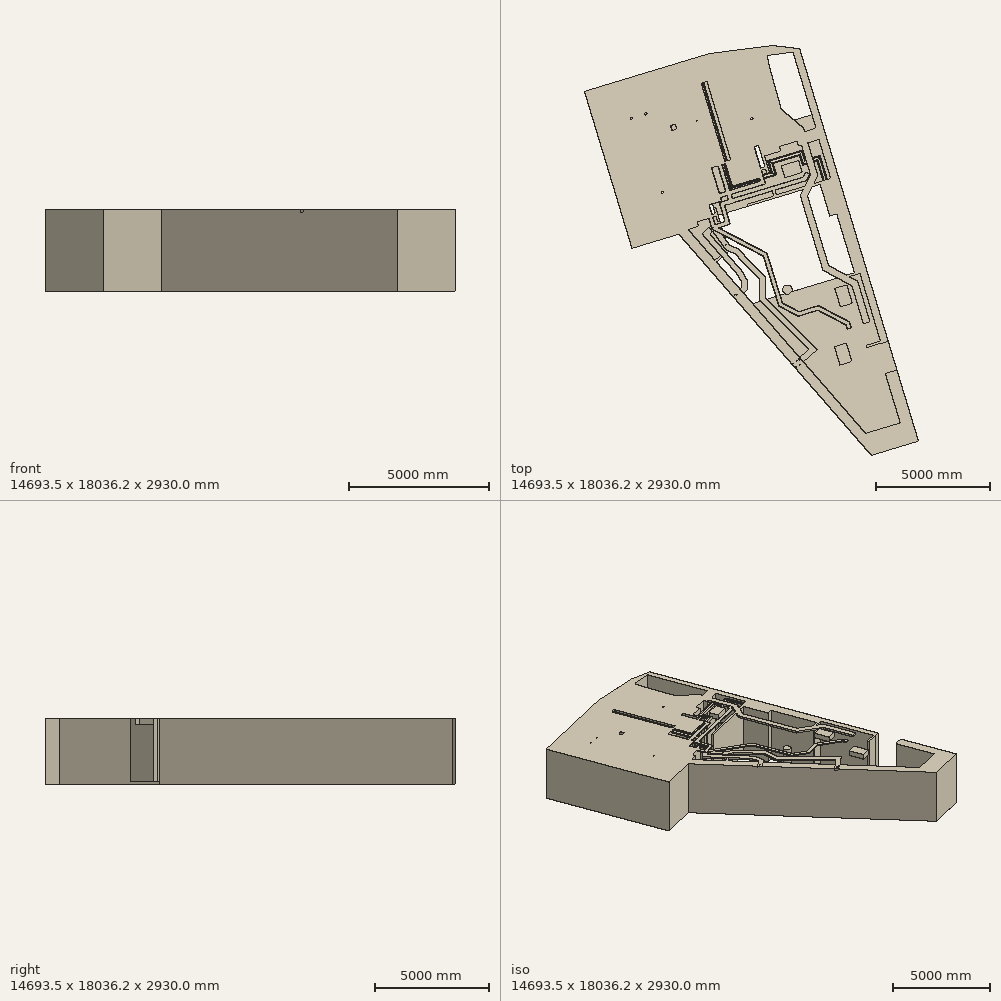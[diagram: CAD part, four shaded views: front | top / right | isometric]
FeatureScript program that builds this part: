
annotation { "Feature Type Name" : "Feature", "Feature Type Description" : "" }
export const myFeature = defineFeature(function(context is Context, id is Id, definition is map)
    precondition{}
    {
        {
            var Q0;
            Q0=qCreatedBy(makeId("Top.planeOp"),FACE);
            var sketch = newSketch(context, id + "F0", { "sketchPlane" : qUnion([Q0])});
            skLineSegment(sketch, "E0", {"start": v(688.47, 32038.93) * mm, "end": v(503.96, 32648.57) * mm});
            skLineSegment(sketch, "E1", {"start": v(503.96, 32648.57) * mm, "end": v(1685.98, 33006.34) * mm});
            skLineSegment(sketch, "E2", {"start": v(1685.98, 33006.34) * mm, "end": v(1870.5, 32396.71) * mm});
            skLineSegment(sketch, "E3", {"start": v(1870.5, 32396.71) * mm, "end": v(688.47, 32038.93) * mm});
            skLineSegment(sketch, "E4", {"start": v(975.28, 28670.43) * mm, "end": v(-209.3, 30031.2) * mm});
            skLineSegment(sketch, "E5", {"start": v(-209.3, 30031.2) * mm, "end": v(247, 30169.35) * mm});
            skLineSegment(sketch, "E6", {"start": v(247, 30169.35) * mm, "end": v(187.3, 30366.58) * mm});
            skLineSegment(sketch, "E7", {"start": v(187.3, 30366.58) * mm, "end": v(1017.23, 30617.78) * mm});
            skLineSegment(sketch, "E8", {"start": v(1017.23, 30617.78) * mm, "end": v(1474.96, 29105.4) * mm});
            skLineSegment(sketch, "E9", {"start": v(1474.96, 29105.4) * mm, "end": v(975.28, 28670.43) * mm});
            skLineSegment(sketch, "E10", {"start": v(2976.11, 33751) * mm, "end": v(2796.5, 34344.43) * mm});
            skLineSegment(sketch, "E11", {"start": v(2796.5, 34344.43) * mm, "end": v(5232.35, 35081.71) * mm});
            skLineSegment(sketch, "E12", {"start": v(5232.35, 35081.71) * mm, "end": v(5411.97, 34488.28) * mm});
            skLineSegment(sketch, "E13", {"start": v(5411.97, 34488.28) * mm, "end": v(2976.11, 33751) * mm});
            skLineSegment(sketch, "E14", {"start": v(1038.97, 28597.26) * mm, "end": v(1585.97, 29073.44) * mm});
            skLineSegment(sketch, "E15", {"start": v(1585.97, 29073.44) * mm, "end": v(1107.2, 30655.36) * mm});
            skLineSegment(sketch, "E16", {"start": v(1107.2, 30655.36) * mm, "end": v(5663.61, 32034.54) * mm});
            skLineSegment(sketch, "E17", {"start": v(5663.61, 32034.54) * mm, "end": v(6064.95, 30708.6) * mm});
            skLineSegment(sketch, "E18", {"start": v(6064.95, 30708.6) * mm, "end": v(6370.27, 30801.02) * mm});
            skLineSegment(sketch, "E19", {"start": v(6370.27, 30801.02) * mm, "end": v(7173.28, 28148.02) * mm});
            skLineSegment(sketch, "E20", {"start": v(7173.28, 28148.02) * mm, "end": v(2627.74, 26772.17) * mm});
            skLineSegment(sketch, "E21", {"start": v(2627.74, 26772.17) * mm, "end": v(1038.97, 28597.26) * mm});
            skLineSegment(sketch, "E22", {"start": v(7648.03, 21005.12) * mm, "end": v(9204.22, 21476.13) * mm});
            skLineSegment(sketch, "E23", {"start": v(9204.22, 21476.13) * mm, "end": v(8546.54, 23648.8) * mm});
            skLineSegment(sketch, "E24", {"start": v(8546.54, 23648.8) * mm, "end": v(8680.59, 23689.38) * mm});
            skLineSegment(sketch, "E25", {"start": v(8680.59, 23689.38) * mm, "end": v(8275.24, 25028.58) * mm});
            skLineSegment(sketch, "E26", {"start": v(8275.24, 25028.58) * mm, "end": v(7643.52, 24837.37) * mm});
            skLineSegment(sketch, "E27", {"start": v(7643.52, 24837.37) * mm, "end": v(7615.16, 24931.08) * mm});
            skLineSegment(sketch, "E28", {"start": v(7615.16, 24931.08) * mm, "end": v(8246.85, 25122.28) * mm});
            skLineSegment(sketch, "E29", {"start": v(8246.85, 25122.28) * mm, "end": v(7345.9, 28098.92) * mm});
            skLineSegment(sketch, "E30", {"start": v(7345.9, 28098.92) * mm, "end": v(6714.19, 27907.71) * mm});
            skLineSegment(sketch, "E31", {"start": v(6714.19, 27907.71) * mm, "end": v(6686.09, 28000.55) * mm});
            skLineSegment(sketch, "E32", {"start": v(6686.09, 28000.55) * mm, "end": v(2627.74, 26772.17) * mm});
            skLineSegment(sketch, "E33", {"start": v(2627.74, 26772.17) * mm, "end": v(7648.03, 21005.12) * mm});
            skLineSegment(sketch, "E34", {"start": v(1953.77, 32421.91) * mm, "end": v(484.9, 37274.77) * mm});
            skLineSegment(sketch, "E35", {"start": v(484.9, 37274.77) * mm, "end": v(817.35, 37375.45) * mm});
            skLineSegment(sketch, "E36", {"start": v(817.35, 37375.45) * mm, "end": v(4399.01, 37834.91) * mm});
            skLineSegment(sketch, "E37", {"start": v(4399.01, 37834.91) * mm, "end": v(5232.35, 35081.71) * mm});
            skLineSegment(sketch, "E38", {"start": v(5232.35, 35081.71) * mm, "end": v(2703.65, 34316.33) * mm});
            skLineSegment(sketch, "E39", {"start": v(2703.65, 34316.33) * mm, "end": v(3166, 32788.83) * mm});
            skLineSegment(sketch, "E40", {"start": v(3166, 32788.83) * mm, "end": v(1953.77, 32421.91) * mm});
            skLineSegment(sketch, "E41", {"start": v(-3492.5, 33275.5) * mm, "end": v(592.96, 34511.99) * mm});
            skLineSegment(sketch, "E42", {"start": v(592.96, 34511.99) * mm, "end": v(1074.07, 32922.48) * mm});
            skLineSegment(sketch, "E43", {"start": v(1074.07, 32922.48) * mm, "end": v(383.02, 32713.3) * mm});
            skLineSegment(sketch, "E44", {"start": v(383.02, 32713.3) * mm, "end": v(981.9, 30734.55) * mm});
            skLineSegment(sketch, "E45", {"start": v(981.9, 30734.55) * mm, "end": v(-2157.46, 29784.33) * mm});
            skLineSegment(sketch, "E46", {"start": v(-2157.46, 29784.33) * mm, "end": v(-2347.02, 30410.5) * mm});
            skLineSegment(sketch, "E47", {"start": v(-2347.02, 30410.5) * mm, "end": v(-2601.66, 30332.35) * mm});
            skLineSegment(sketch, "E48", {"start": v(-2601.66, 30332.35) * mm, "end": v(-3492.5, 33275.5) * mm});
            skLineSegment(sketch, "E49", {"start": v(-710, 34438.17) * mm, "end": v(-3559.9, 33575.84) * mm});
            skLineSegment(sketch, "E50", {"start": v(-3559.9, 33575.84) * mm, "end": v(-3973.74, 34943.1) * mm});
            skLineSegment(sketch, "E51", {"start": v(-3973.74, 34943.1) * mm, "end": v(-3685.65, 35030.3) * mm});
            skLineSegment(sketch, "E52", {"start": v(-3685.65, 35030.3) * mm, "end": v(-3957.95, 35930) * mm});
            skLineSegment(sketch, "E53", {"start": v(-3957.95, 35930) * mm, "end": v(-1009.44, 36822.46) * mm});
            skLineSegment(sketch, "E54", {"start": v(-1009.44, 36822.46) * mm, "end": v(-831.43, 36230.92) * mm});
            skLineSegment(sketch, "E55", {"start": v(-831.43, 36230.92) * mm, "end": v(-977.95, 36186.57) * mm});
            skLineSegment(sketch, "E56", {"start": v(-977.95, 36186.57) * mm, "end": v(-622.8, 35013.09) * mm});
            skLineSegment(sketch, "E57", {"start": v(-622.8, 35013.09) * mm, "end": v(-861.8, 34940.5) * mm});
            skLineSegment(sketch, "E58", {"start": v(-861.8, 34940.5) * mm, "end": v(-710, 34438.17) * mm});
            skLineSegment(sketch, "E59", {"start": v(1107.2, 30655.36) * mm, "end": v(2396.47, 31045.6) * mm});
            skLineSegment(sketch, "E60", {"start": v(2396.47, 31045.6) * mm, "end": v(2368.65, 31137.53) * mm});
            skLineSegment(sketch, "E61", {"start": v(2368.65, 31137.53) * mm, "end": v(3556.94, 31497.2) * mm});
            skLineSegment(sketch, "E62", {"start": v(3556.94, 31497.2) * mm, "end": v(3194.1, 32695.99) * mm});
            skLineSegment(sketch, "E63", {"start": v(3194.1, 32695.99) * mm, "end": v(716.57, 31946.1) * mm});
            skLineSegment(sketch, "E64", {"start": v(716.57, 31946.1) * mm, "end": v(1107.2, 30655.36) * mm});
            skLineSegment(sketch, "E65", {"start": v(-828.96, 36106.8) * mm, "end": v(-267.45, 34251.56) * mm});
            skLineSegment(sketch, "E66", {"start": v(-267.45, 34251.56) * mm, "end": v(583.39, 34509.09) * mm});
            skLineSegment(sketch, "E67", {"start": v(583.39, 34509.09) * mm, "end": v(1064.5, 32919.58) * mm});
            skLineSegment(sketch, "E68", {"start": v(1064.5, 32919.58) * mm, "end": v(1657.88, 33099.18) * mm});
            skLineSegment(sketch, "E69", {"start": v(1657.88, 33099.18) * mm, "end": v(615.22, 36543.93) * mm});
            skLineSegment(sketch, "E70", {"start": v(615.22, 36543.93) * mm, "end": v(-828.96, 36106.8) * mm});
            skLineSegment(sketch, "E71", {"start": v(2521, 36867.94) * mm, "end": v(2477.55, 37011.51) * mm});
            skLineSegment(sketch, "E72", {"start": v(2477.55, 37011.51) * mm, "end": v(2621.12, 37054.97) * mm});
            skLineSegment(sketch, "E73", {"start": v(2621.12, 37054.97) * mm, "end": v(2664.57, 36911.4) * mm});
            skLineSegment(sketch, "E74", {"start": v(2664.57, 36911.4) * mm, "end": v(2521, 36867.94) * mm});
            skCircle(sketch, "E75", {"center": v(2571.06, 36961.45) * mm, "radius": 75 * mm});
            skLineSegment(sketch, "E76", {"start": v(6682.01, 27897.97) * mm, "end": v(2720.36, 26698.86) * mm});
            skLineSegment(sketch, "E77", {"start": v(2845.75, 34181.7) * mm, "end": v(5281.61, 34918.98) * mm});
            skLineSegment(sketch, "E78", {"start": v(6128.04, 25871.52) * mm, "end": v(6340.42, 26268.26) * mm});
            skCircle(sketch, "E79", {"center": v(6234.23, 26069.9) * mm, "radius": 225 * mm});
            skCircle(sketch, "E80", {"center": v(-1847.03, 34397.83) * mm, "radius": 70 * mm});
            skCircle(sketch, "E81", {"center": v(-1031.48, 34644.68) * mm, "radius": 70 * mm});
            skCircle(sketch, "E82", {"center": v(-2662.4, 34151.03) * mm, "radius": 70 * mm});
            skCircle(sketch, "E83", {"center": v(-3282.71, 33963.28) * mm, "radius": 70 * mm});
            skCircle(sketch, "E84", {"center": v(1346.97, 36590.95) * mm, "radius": 70 * mm});
            skCircle(sketch, "E85", {"center": v(1919, 34705.78) * mm, "radius": 70 * mm});
            skCircle(sketch, "E86", {"center": v(4106.18, 35367.8) * mm, "radius": 70 * mm});
            skCircle(sketch, "E87", {"center": v(4291.3, 37482.1) * mm, "radius": 24.96 * mm});
            skCircle(sketch, "E88", {"center": v(4291.3, 37482.1) * mm, "radius": 89.6 * mm});
            skCircle(sketch, "E89", {"center": v(3702.85, 29215.68) * mm, "radius": 50 * mm});
            skLineSegment(sketch, "E90", {"start": v(3774.64, 29237.4) * mm, "end": v(3631.07, 29193.95) * mm});
            skLineSegment(sketch, "E91", {"start": v(3681.12, 29287.46) * mm, "end": v(3724.58, 29143.9) * mm});
            skLineSegment(sketch, "E92", {"start": v(4947.02, 28251.96) * mm, "end": v(4903.56, 28395.53) * mm});
            skLineSegment(sketch, "E93", {"start": v(4903.56, 28395.53) * mm, "end": v(5047.13, 28438.98) * mm});
            skLineSegment(sketch, "E94", {"start": v(5047.13, 28438.98) * mm, "end": v(5090.59, 28295.41) * mm});
            skLineSegment(sketch, "E95", {"start": v(5090.59, 28295.41) * mm, "end": v(4947.02, 28251.96) * mm});
            skCircle(sketch, "E96", {"center": v(4997.08, 28345.47) * mm, "radius": 75 * mm});
            skCircle(sketch, "E97", {"center": v(4647.16, 29501.5) * mm, "radius": 50 * mm});
            skCircle(sketch, "E98", {"center": v(4647.16, 29501.5) * mm, "radius": 185.02 * mm});
            skCircle(sketch, "E99", {"center": v(5731.95, 25917.86) * mm, "radius": 50 * mm});
            skCircle(sketch, "E100", {"center": v(5731.95, 25917.86) * mm, "radius": 185.02 * mm});
            skCircle(sketch, "E101", {"center": v(-1220.67, 35372.03) * mm, "radius": 23.22 * mm});
            skCircle(sketch, "E102", {"center": v(-3689, 35802.45) * mm, "radius": 52 * mm});
            skCircle(sketch, "E103", {"center": v(2856.43, 36018.65) * mm, "radius": 50 * mm});
            skLineSegment(sketch, "E104", {"start": v(2928.21, 36040.38) * mm, "end": v(2784.64, 35996.93) * mm});
            skLineSegment(sketch, "E105", {"start": v(2834.7, 36090.44) * mm, "end": v(2878.16, 35946.87) * mm});
            skCircle(sketch, "E106", {"center": v(2789.14, 31831.37) * mm, "radius": 70 * mm});
            skCircle(sketch, "E107", {"center": v(2325.79, 33360.78) * mm, "radius": 70 * mm});
            skCircle(sketch, "E108", {"center": v(-3089.6, 33189.85) * mm, "radius": 24.96 * mm});
            skCircle(sketch, "E109", {"center": v(-3089.61, 33189.85) * mm, "radius": 89.6 * mm});
            skCircle(sketch, "E110", {"center": v(-694.3, 33908.01) * mm, "radius": 24.96 * mm});
            skCircle(sketch, "E111", {"center": v(-694.3, 33908.01) * mm, "radius": 89.6 * mm});
            skCircle(sketch, "E112", {"center": v(5238.28, 31100.14) * mm, "radius": 70 * mm});
            skCircle(sketch, "E113", {"center": v(-2823.66, 32311.65) * mm, "radius": 70 * mm});
            skLineSegment(sketch, "E114", {"start": v(-1847.07, 31588.32) * mm, "end": v(-1803.62, 31444.75) * mm});
            skLineSegment(sketch, "E115", {"start": v(-1803.62, 31444.75) * mm, "end": v(-1947.18, 31401.3) * mm});
            skLineSegment(sketch, "E116", {"start": v(-1947.18, 31401.3) * mm, "end": v(-1990.64, 31544.87) * mm});
            skLineSegment(sketch, "E117", {"start": v(-1990.64, 31544.87) * mm, "end": v(-1847.07, 31588.32) * mm});
            skCircle(sketch, "E118", {"center": v(-1897.13, 31494.81) * mm, "radius": 75 * mm});
            skLineSegment(sketch, "E119", {"start": v(-798.77, 31748.9) * mm, "end": v(-842.22, 31892.47) * mm});
            skLineSegment(sketch, "E120", {"start": v(-842.22, 31892.47) * mm, "end": v(-698.66, 31935.92) * mm});
            skLineSegment(sketch, "E121", {"start": v(-698.66, 31935.92) * mm, "end": v(-655.2, 31792.36) * mm});
            skLineSegment(sketch, "E122", {"start": v(-655.2, 31792.36) * mm, "end": v(-798.77, 31748.9) * mm});
            skCircle(sketch, "E123", {"center": v(-748.71, 31842.41) * mm, "radius": 75 * mm});
            skCircle(sketch, "E124", {"center": v(-1322.96, 31668.6) * mm, "radius": 50 * mm});
            skLineSegment(sketch, "E125", {"start": v(-1251.18, 31690.33) * mm, "end": v(-1394.75, 31646.87) * mm});
            skLineSegment(sketch, "E126", {"start": v(-1344.7, 31740.38) * mm, "end": v(-1301.24, 31596.82) * mm});
            skCircle(sketch, "E127", {"center": v(1916.85, 30094.8) * mm, "radius": 70 * mm});
            skLineSegment(sketch, "E128", {"start": v(5408.3, 27246.02) * mm, "end": v(5451.75, 27102.45) * mm});
            skLineSegment(sketch, "E129", {"start": v(5451.75, 27102.45) * mm, "end": v(5308.19, 27059) * mm});
            skLineSegment(sketch, "E130", {"start": v(5308.19, 27059) * mm, "end": v(5264.73, 27202.57) * mm});
            skLineSegment(sketch, "E131", {"start": v(5264.73, 27202.57) * mm, "end": v(5408.3, 27246.02) * mm});
            skCircle(sketch, "E132", {"center": v(5358.24, 27152.51) * mm, "radius": 75 * mm});
            skCircle(sketch, "E133", {"center": v(7896.13, 22311.4) * mm, "radius": 50 * mm});
            skLineSegment(sketch, "E134", {"start": v(7967.91, 22333.12) * mm, "end": v(7824.34, 22289.67) * mm});
            skLineSegment(sketch, "E135", {"start": v(7874.4, 22383.18) * mm, "end": v(7917.86, 22239.6) * mm});
            skLineSegment(sketch, "E136", {"start": v(7346.13, 23869.61) * mm, "end": v(7302.67, 24013.18) * mm});
            skLineSegment(sketch, "E137", {"start": v(7302.67, 24013.18) * mm, "end": v(7446.24, 24056.63) * mm});
            skLineSegment(sketch, "E138", {"start": v(7446.24, 24056.63) * mm, "end": v(7489.7, 23913.07) * mm});
            skLineSegment(sketch, "E139", {"start": v(7489.7, 23913.07) * mm, "end": v(7346.13, 23869.61) * mm});
            skCircle(sketch, "E140", {"center": v(7396.18, 23963.12) * mm, "radius": 75 * mm});
            skCircle(sketch, "E141", {"center": v(7193.06, 26360.11) * mm, "radius": 50 * mm});
            skLineSegment(sketch, "E142", {"start": v(7240.92, 26374.6) * mm, "end": v(7514.25, 26457.33) * mm});
            skLineSegment(sketch, "E143", {"start": v(7365.6, 26307.86) * mm, "end": v(7240.92, 26374.6) * mm});
            skLineSegment(sketch, "E144", {"start": v(7240.92, 26374.6) * mm, "end": v(7307.66, 26499.27) * mm});
            skLineSegment(sketch, "E145", {"start": v(7307.66, 26499.27) * mm, "end": v(7365.6, 26307.86) * mm});
            skLineSegment(sketch, "E146", {"start": v(575.66, 33236.57) * mm, "end": v(546.8, 33331.8) * mm});
            skLineSegment(sketch, "E147", {"start": v(546.8, 33331.8) * mm, "end": v(655.88, 33364.87) * mm});
            skLineSegment(sketch, "E148", {"start": v(655.88, 33364.87) * mm, "end": v(684.75, 33269.65) * mm});
            skLineSegment(sketch, "E149", {"start": v(684.75, 33269.65) * mm, "end": v(575.66, 33236.57) * mm});
            skLineSegment(sketch, "E150", {"start": v(546.79, 33331.8) * mm, "end": v(517.92, 33427.01) * mm});
            skLineSegment(sketch, "E151", {"start": v(517.92, 33427.01) * mm, "end": v(627.01, 33460.09) * mm});
            skLineSegment(sketch, "E152", {"start": v(627.01, 33460.09) * mm, "end": v(655.88, 33364.87) * mm});
            skLineSegment(sketch, "E153", {"start": v(655.88, 33364.87) * mm, "end": v(546.79, 33331.8) * mm});
            skLineSegment(sketch, "E154", {"start": v(3585.52, 37346.87) * mm, "end": v(3628.97, 37203.3) * mm});
            skLineSegment(sketch, "E155", {"start": v(3628.97, 37203.3) * mm, "end": v(3485.4, 37159.85) * mm});
            skLineSegment(sketch, "E156", {"start": v(3485.4, 37159.85) * mm, "end": v(3441.95, 37303.42) * mm});
            skLineSegment(sketch, "E157", {"start": v(3441.95, 37303.42) * mm, "end": v(3585.52, 37346.87) * mm});
            skCircle(sketch, "E158", {"center": v(3535.46, 37253.36) * mm, "radius": 75 * mm});
            skLineSegment(sketch, "E159", {"start": v(-4301.45, 33405.9) * mm, "end": v(-4393.43, 33709.79) * mm});
            skEllipse(sketch, "E160", {"center": v(-4253.27, 33246.73) * mm, "majorRadius": 182.04 * mm, "minorRadius": 182.04 * mm, "majorAxis": v(0.7, 0.7)});
            skLineSegment(sketch, "E161", {"start": v(-4393.43, 33709.79) * mm, "end": v(-3952.33, 34533.82) * mm});
            skLineSegment(sketch, "E162", {"start": v(-4064.75, 34413.93) * mm, "end": v(-3952.33, 34533.82) * mm});
            skLineSegment(sketch, "E163", {"start": v(-3952.33, 34533.82) * mm, "end": v(-3989.74, 34373.78) * mm});
            skLineSegment(sketch, "E164", {"start": v(-3989.74, 34373.78) * mm, "end": v(-4064.75, 34413.93) * mm});
            skLineSegment(sketch, "E165", {"start": v(-3654.18, 34799.3) * mm, "end": v(-3257.44, 34586.93) * mm});
            skCircle(sketch, "E166", {"center": v(-3455.8, 34693.11) * mm, "radius": 225 * mm});
            skLineSegment(sketch, "E167", {"start": v(-2284.17, 37866.22) * mm, "end": v(-2192.19, 37562.34) * mm});
            skEllipse(sketch, "E168", {"center": v(-2332.35, 38025.4) * mm, "majorRadius": 182.04 * mm, "minorRadius": 182.04 * mm, "majorAxis": v(1, 0)});
            skLineSegment(sketch, "E169", {"start": v(-2192.19, 37562.34) * mm, "end": v(-2055.36, 37110.28) * mm});
            skLineSegment(sketch, "E170", {"start": v(-2060.64, 37274.55) * mm, "end": v(-2055.36, 37110.28) * mm});
            skLineSegment(sketch, "E171", {"start": v(-2055.36, 37110.28) * mm, "end": v(-2142.06, 37249.9) * mm});
            skLineSegment(sketch, "E172", {"start": v(-2142.06, 37249.9) * mm, "end": v(-2060.64, 37274.55) * mm});
            skLineSegment(sketch, "E173", {"start": v(6324.7, 31290.66) * mm, "end": v(6411.61, 31003.53) * mm});
            skLineSegment(sketch, "E174", {"start": v(6411.61, 31003.53) * mm, "end": v(6124.47, 30916.62) * mm});
            skLineSegment(sketch, "E175", {"start": v(6124.47, 30916.62) * mm, "end": v(6037.56, 31203.75) * mm});
            skLineSegment(sketch, "E176", {"start": v(6037.56, 31203.75) * mm, "end": v(6324.7, 31290.66) * mm});
            skLineSegment(sketch, "E177", {"start": v(6324.7, 31290.66) * mm, "end": v(6124.47, 30916.62) * mm});
            skCircle(sketch, "E178", {"center": v(-3095.59, 35982.06) * mm, "radius": 52 * mm});
            skCircle(sketch, "E179", {"center": v(-2502.17, 36161.68) * mm, "radius": 52 * mm});
            skCircle(sketch, "E180", {"center": v(-1908.76, 36341.3) * mm, "radius": 52 * mm});
            skCircle(sketch, "E181", {"center": v(-1315.35, 36520.9) * mm, "radius": 52 * mm});
            skCircle(sketch, "E182", {"center": v(2532.3, 27643.33) * mm, "radius": 70 * mm});
            skCircle(sketch, "E183", {"center": v(1875.7, 28397.58) * mm, "radius": 70 * mm});
            skLineSegment(sketch, "E184", {"start": v(1609.88, 32773.32) * mm, "end": v(1696.79, 32486.2) * mm});
            skLineSegment(sketch, "E185", {"start": v(1696.79, 32486.2) * mm, "end": v(1409.64, 32399.28) * mm});
            skLineSegment(sketch, "E186", {"start": v(1409.64, 32399.28) * mm, "end": v(1322.74, 32686.4) * mm});
            skLineSegment(sketch, "E187", {"start": v(1322.74, 32686.4) * mm, "end": v(1609.88, 32773.32) * mm});
            skLineSegment(sketch, "E188", {"start": v(1609.88, 32773.32) * mm, "end": v(1409.64, 32399.28) * mm});
            skCircle(sketch, "E189", {"center": v(6011.32, 23646.8) * mm, "radius": 70 * mm});
            skCircle(sketch, "E190", {"center": v(3459.78, 26577.88) * mm, "radius": 70 * mm});
            skCircle(sketch, "E191", {"center": v(8590.03, 22521.42) * mm, "radius": 70 * mm});
            skCircle(sketch, "E192", {"center": v(6714.5, 26215.26) * mm, "radius": 70 * mm});
            skCircle(sketch, "E193", {"center": v(7043.04, 25129.83) * mm, "radius": 70 * mm});
            skCircle(sketch, "E194", {"center": v(4413.86, 26866.66) * mm, "radius": 50 * mm});
            skLineSegment(sketch, "E195", {"start": v(4485.64, 26888.4) * mm, "end": v(4342.07, 26844.94) * mm});
            skLineSegment(sketch, "E196", {"start": v(4392.13, 26938.45) * mm, "end": v(4435.58, 26794.88) * mm});
            skCircle(sketch, "E197", {"center": v(5979.71, 28642.9) * mm, "radius": 70 * mm});
            skLineSegment(sketch, "E198", {"start": v(1029.24, 34682.5) * mm, "end": v(1116.14, 34395.38) * mm});
            skLineSegment(sketch, "E199", {"start": v(1116.14, 34395.38) * mm, "end": v(829, 34308.46) * mm});
            skLineSegment(sketch, "E200", {"start": v(829, 34308.46) * mm, "end": v(742.1, 34595.59) * mm});
            skLineSegment(sketch, "E201", {"start": v(742.1, 34595.59) * mm, "end": v(1029.24, 34682.5) * mm});
            skLineSegment(sketch, "E202", {"start": v(1029.24, 34682.5) * mm, "end": v(829, 34308.46) * mm});
            skLineSegment(sketch, "E203", {"start": v(3855.94, 24986.4) * mm, "end": v(3968.37, 25106.3) * mm});
            skLineSegment(sketch, "E204", {"start": v(3968.37, 25106.3) * mm, "end": v(3930.95, 24946.26) * mm});
            skLineSegment(sketch, "E205", {"start": v(3930.95, 24946.26) * mm, "end": v(3855.94, 24986.4) * mm});
            skLineSegment(sketch, "E206", {"start": v(6167.02, 21051.64) * mm, "end": v(6075.04, 21355.52) * mm});
            skEllipse(sketch, "E207", {"center": v(6215.2, 20892.46) * mm, "majorRadius": 182.04 * mm, "minorRadius": 182.04 * mm, "majorAxis": v(0.7, 0.7)});
            skLineSegment(sketch, "E208", {"start": v(6075.04, 21355.52) * mm, "end": v(6516.14, 22179.55) * mm});
            skLineSegment(sketch, "E209", {"start": v(6403.72, 22059.66) * mm, "end": v(6516.14, 22179.55) * mm});
            skLineSegment(sketch, "E210", {"start": v(6516.14, 22179.55) * mm, "end": v(6478.72, 22019.51) * mm});
            skLineSegment(sketch, "E211", {"start": v(6478.72, 22019.51) * mm, "end": v(6403.72, 22059.66) * mm});
            skLineSegment(sketch, "E212", {"start": v(-3715.4, 37697.94) * mm, "end": v(-2680.13, 36361.95) * mm});
            skLineSegment(sketch, "E213", {"start": v(-2743.75, 36513.49) * mm, "end": v(-2680.13, 36361.95) * mm});
            skLineSegment(sketch, "E214", {"start": v(-2680.13, 36361.95) * mm, "end": v(-2811, 36461.38) * mm});
            skLineSegment(sketch, "E215", {"start": v(-2811, 36461.38) * mm, "end": v(-2743.75, 36513.49) * mm});
            skLineSegment(sketch, "E216", {"start": v(6668.7, 25183.66) * mm, "end": v(6456.33, 24786.93) * mm});
            skCircle(sketch, "E217", {"center": v(6562.52, 24985.3) * mm, "radius": 225 * mm});
            skCircle(sketch, "E218", {"center": v(860.2, 30103.67) * mm, "radius": 50 * mm});
            skLineSegment(sketch, "E219", {"start": v(908.05, 30118.16) * mm, "end": v(1181.38, 30200.89) * mm});
            skLineSegment(sketch, "E220", {"start": v(1032.72, 30051.42) * mm, "end": v(908.05, 30118.16) * mm});
            skLineSegment(sketch, "E221", {"start": v(908.05, 30118.16) * mm, "end": v(974.79, 30242.83) * mm});
            skLineSegment(sketch, "E222", {"start": v(974.79, 30242.83) * mm, "end": v(1032.72, 30051.42) * mm});
            skLineSegment(sketch, "E223", {"start": v(3665, 31553.41) * mm, "end": v(3146.69, 33265.8) * mm});
            skLineSegment(sketch, "E224", {"start": v(3146.69, 33265.8) * mm, "end": v(3864.66, 33483.1) * mm});
            skLineSegment(sketch, "E225", {"start": v(3864.66, 33483.1) * mm, "end": v(3803.84, 33684.03) * mm});
            skLineSegment(sketch, "E226", {"start": v(3803.84, 33684.03) * mm, "end": v(4569.53, 33915.8) * mm});
            skLineSegment(sketch, "E227", {"start": v(4569.53, 33915.8) * mm, "end": v(4630.34, 33714.9) * mm});
            skLineSegment(sketch, "E228", {"start": v(4630.34, 33714.9) * mm, "end": v(5539.28, 33990.02) * mm});
            skLineSegment(sketch, "E229", {"start": v(5539.28, 33990.02) * mm, "end": v(6057.79, 32277.66) * mm});
            skLineSegment(sketch, "E230", {"start": v(6057.79, 32277.66) * mm, "end": v(3665, 31553.41) * mm});
            skCircle(sketch, "E231", {"center": v(3988.93, 33314.17) * mm, "radius": 70 * mm});
            skCircle(sketch, "E232", {"center": v(5732.52, 32722.3) * mm, "radius": 52 * mm});
            skCircle(sketch, "E233", {"center": v(5479.1, 33559.56) * mm, "radius": 52 * mm});
            skCircle(sketch, "E234", {"center": v(3586.94, 33192.5) * mm, "radius": 70 * mm});
            skCircle(sketch, "E235", {"center": v(5058.95, 32518.43) * mm, "radius": 50 * mm});
            skLineSegment(sketch, "E236", {"start": v(5035.58, 32474.22) * mm, "end": v(4902.1, 32221.76) * mm});
            skLineSegment(sketch, "E237", {"start": v(4900.44, 32432.56) * mm, "end": v(5035.58, 32474.22) * mm});
            skLineSegment(sketch, "E238", {"start": v(5035.58, 32474.22) * mm, "end": v(5077.24, 32339.09) * mm});
            skLineSegment(sketch, "E239", {"start": v(5077.24, 32339.09) * mm, "end": v(4900.44, 32432.56) * mm});
            skCircle(sketch, "E240", {"center": v(3482.78, 32663.76) * mm, "radius": 23.22 * mm});
            skLineSegment(sketch, "E241", {"start": v(1963.34, 32424.81) * mm, "end": v(494.48, 37277.66) * mm});
            skLineSegment(sketch, "E242", {"start": v(494.48, 37277.66) * mm, "end": v(561.48, 37297.94) * mm});
            skLineSegment(sketch, "E243", {"start": v(561.48, 37297.94) * mm, "end": v(2030.34, 32445.09) * mm});
            skLineSegment(sketch, "E244", {"start": v(2030.34, 32445.09) * mm, "end": v(1963.34, 32424.81) * mm});
            skLineSegment(sketch, "E245", {"start": v(-3492.5, 33275.5) * mm, "end": v(-3425.5, 33295.77) * mm});
            skLineSegment(sketch, "E246", {"start": v(-3425.5, 33295.77) * mm, "end": v(-2534.67, 30352.63) * mm});
            skLineSegment(sketch, "E247", {"start": v(-2534.67, 30352.63) * mm, "end": v(-2601.66, 30332.35) * mm});
            skLineSegment(sketch, "E248", {"start": v(7627.75, 21072.12) * mm, "end": v(9116.94, 21522.85) * mm});
            skLineSegment(sketch, "E249", {"start": v(9116.94, 21522.85) * mm, "end": v(8459.27, 23695.52) * mm});
            skLineSegment(sketch, "E250", {"start": v(8459.27, 23695.52) * mm, "end": v(8660.3, 23756.37) * mm});
            skLineSegment(sketch, "E251", {"start": v(8660.3, 23756.37) * mm, "end": v(8680.59, 23689.38) * mm});
            skLineSegment(sketch, "E252", {"start": v(8680.59, 23689.38) * mm, "end": v(8546.54, 23648.8) * mm});
            skLineSegment(sketch, "E253", {"start": v(8546.54, 23648.8) * mm, "end": v(9204.22, 21476.13) * mm});
            skLineSegment(sketch, "E254", {"start": v(9204.22, 21476.13) * mm, "end": v(7648.03, 21005.12) * mm});
            skLineSegment(sketch, "E255", {"start": v(7648.03, 21005.12) * mm, "end": v(7627.75, 21072.12) * mm});
            skLineSegment(sketch, "E256", {"start": v(7173.28, 28148.02) * mm, "end": v(7106.28, 28127.74) * mm});
            skLineSegment(sketch, "E257", {"start": v(7106.28, 28127.74) * mm, "end": v(6323.55, 30713.74) * mm});
            skLineSegment(sketch, "E258", {"start": v(6323.55, 30713.74) * mm, "end": v(6018.23, 30621.33) * mm});
            skLineSegment(sketch, "E259", {"start": v(6018.23, 30621.33) * mm, "end": v(5596.86, 32013.45) * mm});
            skLineSegment(sketch, "E260", {"start": v(5596.86, 32013.45) * mm, "end": v(5663.86, 32033.73) * mm});
            skLineSegment(sketch, "E261", {"start": v(5663.86, 32033.73) * mm, "end": v(6064.95, 30708.6) * mm});
            skLineSegment(sketch, "E262", {"start": v(-6.74, 35160.65) * mm, "end": v(-35.61, 35255.87) * mm});
            skLineSegment(sketch, "E263", {"start": v(-35.61, 35255.87) * mm, "end": v(73.48, 35288.95) * mm});
            skLineSegment(sketch, "E264", {"start": v(73.48, 35288.95) * mm, "end": v(102.35, 35193.73) * mm});
            skLineSegment(sketch, "E265", {"start": v(102.35, 35193.73) * mm, "end": v(-6.74, 35160.65) * mm});
            skLineSegment(sketch, "E266", {"start": v(-35.61, 35255.87) * mm, "end": v(-64.48, 35351.09) * mm});
            skLineSegment(sketch, "E267", {"start": v(-64.48, 35351.09) * mm, "end": v(44.6, 35384.16) * mm});
            skLineSegment(sketch, "E268", {"start": v(44.6, 35384.16) * mm, "end": v(73.48, 35288.95) * mm});
            skLineSegment(sketch, "E269", {"start": v(73.48, 35288.95) * mm, "end": v(-35.61, 35255.87) * mm});
            skLineSegment(sketch, "E270", {"start": v(-281.93, 34299.42) * mm, "end": v(578.47, 34559.84) * mm});
            skLineSegment(sketch, "E271", {"start": v(8380.43, 21227.85) * mm, "end": v(8462.74, 21252.76) * mm});
            skArc(sketch, "E272", {"start": v(8462.74, 21252.76) * mm, "mid": v(8409.13, 21281.46) * mm, "end": v(8380.43, 21227.85) * mm});
            skLineSegment(sketch, "E273", {"start": v(8421.58, 21240.3) * mm, "end": v(8392.62, 21336.02) * mm});
            skLineSegment(sketch, "E274", {"start": v(8462.74, 21252.76) * mm, "end": v(8380.43, 21227.85) * mm});
            skLineSegment(sketch, "E275", {"start": v(8380.43, 21227.85) * mm, "end": v(8377.53, 21237.42) * mm});
            skLineSegment(sketch, "E276", {"start": v(8377.53, 21237.42) * mm, "end": v(8459.84, 21262.33) * mm});
            skLineSegment(sketch, "E277", {"start": v(8459.84, 21262.33) * mm, "end": v(8462.74, 21252.76) * mm});
            skCircle(sketch, "E278", {"center": v(6340.55, 27450.74) * mm, "radius": 70 * mm});
            skCircle(sketch, "E279", {"center": v(8090.05, 24173.16) * mm, "radius": 70 * mm});
            skCircle(sketch, "E280", {"center": v(4698.2, 25155.24) * mm, "radius": 70 * mm});
            skLineSegment(sketch, "E281", {"start": v(1306.25, 28829.94) * mm, "end": v(1241.38, 28773.47) * mm});
            skArc(sketch, "E282", {"start": v(1241.38, 28773.47) * mm, "mid": v(1302.05, 28769.27) * mm, "end": v(1306.25, 28829.94) * mm});
            skLineSegment(sketch, "E283", {"start": v(1273.82, 28801.7) * mm, "end": v(1339.47, 28726.28) * mm});
            skLineSegment(sketch, "E284", {"start": v(1241.38, 28773.47) * mm, "end": v(1306.25, 28829.94) * mm});
            skLineSegment(sketch, "E285", {"start": v(1306.25, 28829.94) * mm, "end": v(1312.81, 28822.4) * mm});
            skLineSegment(sketch, "E286", {"start": v(1312.81, 28822.4) * mm, "end": v(1247.95, 28765.93) * mm});
            skLineSegment(sketch, "E287", {"start": v(1247.95, 28765.93) * mm, "end": v(1241.38, 28773.47) * mm});
            skCircle(sketch, "E288", {"center": v(5629.8, 29798.92) * mm, "radius": 70 * mm});
            skLineSegment(sketch, "E289", {"start": v(6948.35, 28891.15) * mm, "end": v(6923.43, 28973.47) * mm});
            skArc(sketch, "E290", {"start": v(6923.43, 28973.47) * mm, "mid": v(6894.73, 28919.85) * mm, "end": v(6948.35, 28891.15) * mm});
            skLineSegment(sketch, "E291", {"start": v(6935.9, 28932.31) * mm, "end": v(6840.18, 28903.34) * mm});
            skLineSegment(sketch, "E292", {"start": v(6923.43, 28973.47) * mm, "end": v(6948.35, 28891.15) * mm});
            skLineSegment(sketch, "E293", {"start": v(6948.35, 28891.15) * mm, "end": v(6938.78, 28888.26) * mm});
            skLineSegment(sketch, "E294", {"start": v(6938.78, 28888.26) * mm, "end": v(6913.86, 28970.57) * mm});
            skLineSegment(sketch, "E295", {"start": v(6913.86, 28970.57) * mm, "end": v(6923.43, 28973.47) * mm});
            skCircle(sketch, "E296", {"center": v(1508.54, 31443.79) * mm, "radius": 70 * mm});
            skLineSegment(sketch, "E297", {"start": v(-746.1, 30211.52) * mm, "end": v(-663.8, 30236.44) * mm});
            skArc(sketch, "E298", {"start": v(-663.8, 30236.44) * mm, "mid": v(-717.4, 30265.14) * mm, "end": v(-746.1, 30211.52) * mm});
            skLineSegment(sketch, "E299", {"start": v(-704.95, 30223.98) * mm, "end": v(-733.92, 30319.7) * mm});
            skLineSegment(sketch, "E300", {"start": v(-663.8, 30236.44) * mm, "end": v(-746.1, 30211.52) * mm});
            skLineSegment(sketch, "E301", {"start": v(-746.1, 30211.52) * mm, "end": v(-749, 30221.1) * mm});
            skLineSegment(sketch, "E302", {"start": v(-749, 30221.1) * mm, "end": v(-666.69, 30246) * mm});
            skLineSegment(sketch, "E303", {"start": v(-666.69, 30246) * mm, "end": v(-663.8, 30236.44) * mm});
            skLineSegment(sketch, "E304", {"start": v(-2321.17, 30329.54) * mm, "end": v(-2296.26, 30247.23) * mm});
            skArc(sketch, "E305", {"start": v(-2296.26, 30247.23) * mm, "mid": v(-2267.56, 30300.84) * mm, "end": v(-2321.17, 30329.54) * mm});
            skLineSegment(sketch, "E306", {"start": v(-2308.72, 30288.38) * mm, "end": v(-2213, 30317.35) * mm});
            skLineSegment(sketch, "E307", {"start": v(-2296.26, 30247.23) * mm, "end": v(-2321.17, 30329.54) * mm});
            skLineSegment(sketch, "E308", {"start": v(-2321.17, 30329.54) * mm, "end": v(-2311.6, 30332.44) * mm});
            skLineSegment(sketch, "E309", {"start": v(-2311.6, 30332.44) * mm, "end": v(-2286.69, 30250.12) * mm});
            skLineSegment(sketch, "E310", {"start": v(-2286.69, 30250.12) * mm, "end": v(-2296.26, 30247.23) * mm});
            skCircle(sketch, "E311", {"center": v(-2520.05, 31308.13) * mm, "radius": 70 * mm});
            skCircle(sketch, "E312", {"center": v(174.15, 31038.83) * mm, "radius": 70 * mm});
            skLineSegment(sketch, "E313", {"start": v(-3106, 33392.47) * mm, "end": v(-3188.32, 33367.55) * mm});
            skArc(sketch, "E314", {"start": v(-3188.32, 33367.55) * mm, "mid": v(-3134.7, 33338.85) * mm, "end": v(-3106, 33392.47) * mm});
            skLineSegment(sketch, "E315", {"start": v(-3147.16, 33380) * mm, "end": v(-3118.2, 33284.3) * mm});
            skLineSegment(sketch, "E316", {"start": v(-3188.32, 33367.55) * mm, "end": v(-3106, 33392.47) * mm});
            skLineSegment(sketch, "E317", {"start": v(-3106, 33392.47) * mm, "end": v(-3103.11, 33382.9) * mm});
            skLineSegment(sketch, "E318", {"start": v(-3103.11, 33382.9) * mm, "end": v(-3185.42, 33357.98) * mm});
            skLineSegment(sketch, "E319", {"start": v(-3185.42, 33357.98) * mm, "end": v(-3188.32, 33367.55) * mm});
            skLineSegment(sketch, "E320", {"start": v(-712.6, 34116.9) * mm, "end": v(-794.9, 34092) * mm});
            skArc(sketch, "E321", {"start": v(-794.9, 34092) * mm, "mid": v(-741.29, 34063.3) * mm, "end": v(-712.6, 34116.9) * mm});
            skLineSegment(sketch, "E322", {"start": v(-753.75, 34104.45) * mm, "end": v(-724.78, 34008.74) * mm});
            skLineSegment(sketch, "E323", {"start": v(-794.9, 34092) * mm, "end": v(-712.6, 34116.9) * mm});
            skLineSegment(sketch, "E324", {"start": v(-712.6, 34116.9) * mm, "end": v(-709.7, 34107.33) * mm});
            skLineSegment(sketch, "E325", {"start": v(-709.7, 34107.33) * mm, "end": v(-792, 34082.42) * mm});
            skLineSegment(sketch, "E326", {"start": v(-792, 34082.42) * mm, "end": v(-794.9, 34092) * mm});
            skLineSegment(sketch, "E327", {"start": v(4535.84, 37382.88) * mm, "end": v(4510.92, 37465.2) * mm});
            skArc(sketch, "E328", {"start": v(4510.92, 37465.2) * mm, "mid": v(4482.23, 37411.58) * mm, "end": v(4535.84, 37382.88) * mm});
            skLineSegment(sketch, "E329", {"start": v(4523.38, 37424.04) * mm, "end": v(4427.67, 37395.06) * mm});
            skLineSegment(sketch, "E330", {"start": v(4510.92, 37465.2) * mm, "end": v(4535.84, 37382.88) * mm});
            skLineSegment(sketch, "E331", {"start": v(4535.84, 37382.88) * mm, "end": v(4526.27, 37379.99) * mm});
            skLineSegment(sketch, "E332", {"start": v(4526.27, 37379.99) * mm, "end": v(4501.35, 37462.3) * mm});
            skLineSegment(sketch, "E333", {"start": v(4501.35, 37462.3) * mm, "end": v(4510.92, 37465.2) * mm});
            skLineSegment(sketch, "E334", {"start": v(5039.15, 35719.61) * mm, "end": v(5014.23, 35801.92) * mm});
            skArc(sketch, "E335", {"start": v(5014.23, 35801.92) * mm, "mid": v(4985.53, 35748.3) * mm, "end": v(5039.15, 35719.61) * mm});
            skLineSegment(sketch, "E336", {"start": v(5026.69, 35760.77) * mm, "end": v(4930.98, 35731.8) * mm});
            skLineSegment(sketch, "E337", {"start": v(5014.23, 35801.92) * mm, "end": v(5039.15, 35719.61) * mm});
            skLineSegment(sketch, "E338", {"start": v(5039.15, 35719.61) * mm, "end": v(5029.58, 35716.72) * mm});
            skLineSegment(sketch, "E339", {"start": v(5029.58, 35716.72) * mm, "end": v(5004.66, 35799.03) * mm});
            skLineSegment(sketch, "E340", {"start": v(5004.66, 35799.03) * mm, "end": v(5014.23, 35801.92) * mm});
            skCircle(sketch, "E341", {"center": v(4857.02, 35595.06) * mm, "radius": 24.96 * mm});
            skCircle(sketch, "E342", {"center": v(4857.02, 35595.06) * mm, "radius": 89.6 * mm});
            skLineSegment(sketch, "E343", {"start": v(578.84, 36955.8) * mm, "end": v(603.76, 36873.5) * mm});
            skArc(sketch, "E344", {"start": v(603.76, 36873.5) * mm, "mid": v(632.45, 36927.1) * mm, "end": v(578.84, 36955.8) * mm});
            skLineSegment(sketch, "E345", {"start": v(591.3, 36914.65) * mm, "end": v(687, 36943.62) * mm});
            skLineSegment(sketch, "E346", {"start": v(603.76, 36873.5) * mm, "end": v(578.84, 36955.8) * mm});
            skLineSegment(sketch, "E347", {"start": v(578.84, 36955.8) * mm, "end": v(588.41, 36958.7) * mm});
            skLineSegment(sketch, "E348", {"start": v(588.41, 36958.7) * mm, "end": v(613.33, 36876.4) * mm});
            skLineSegment(sketch, "E349", {"start": v(613.33, 36876.4) * mm, "end": v(603.76, 36873.5) * mm});
            skCircle(sketch, "E350", {"center": v(4620.62, 33505.38) * mm, "radius": 70 * mm});
            skArc(sketch, "E351", {"start": v(4956.81, 34398.56) * mm, "mid": v(4763.36, 34417.74) * mm, "end": v(4640.12, 34568.09) * mm});
            skArc(sketch, "E352", {"start": v(4640.12, 34568.09) * mm, "mid": v(4659.3, 34761.54) * mm, "end": v(4809.65, 34884.78) * mm});
            skArc(sketch, "E353", {"start": v(4809.65, 34884.78) * mm, "mid": v(5003.1, 34865.6) * mm, "end": v(5126.34, 34715.25) * mm});
            skArc(sketch, "E354", {"start": v(5126.34, 34715.25) * mm, "mid": v(5107.16, 34521.8) * mm, "end": v(4956.81, 34398.56) * mm});
            skLineSegment(sketch, "E355", {"start": v(4956.81, 34398.56) * mm, "end": v(4809.65, 34884.78) * mm});
            skArc(sketch, "E356", {"start": v(-1994.08, 35626.89) * mm, "mid": v(-1974.9, 35820.34) * mm, "end": v(-1824.55, 35943.58) * mm});
            skArc(sketch, "E357", {"start": v(4471.25, 25817.53) * mm, "mid": v(4277.8, 25836.7) * mm, "end": v(4154.56, 25987.06) * mm});
            skArc(sketch, "E358", {"start": v(4154.56, 25987.06) * mm, "mid": v(4173.74, 26180.51) * mm, "end": v(4324.09, 26303.75) * mm});
            skArc(sketch, "E359", {"start": v(4324.09, 26303.75) * mm, "mid": v(4517.54, 26284.58) * mm, "end": v(4640.78, 26134.23) * mm});
            skArc(sketch, "E360", {"start": v(4640.78, 26134.23) * mm, "mid": v(4621.6, 25940.77) * mm, "end": v(4471.25, 25817.53) * mm});
            skLineSegment(sketch, "E361", {"start": v(4471.25, 25817.53) * mm, "end": v(4324.09, 26303.75) * mm});
            skArc(sketch, "E362", {"start": v(273.35, 36589.26) * mm, "mid": v(79.9, 36608.44) * mm, "end": v(-43.34, 36758.79) * mm});
            skCircle(sketch, "E363", {"center": v(3141.78, 35075.9) * mm, "radius": 70 * mm});
            skCircle(sketch, "E364", {"center": v(-35072.5, -36736.78) * mm, "radius": 1927.6 * mm});
            skLineSegment(sketch, "E365", {"start": v(-35072.5, -31736.78) * mm, "end": v(-35072.5, -41736.78) * mm});
            skLineSegment(sketch, "E366", {"start": v(-30072.5, -36736.78) * mm, "end": v(-40072.5, -36736.78) * mm});
            skLineSegment(sketch, "E367", {"start": v(9242.48, 21401.51) * mm, "end": v(8565.25, 23638.8) * mm});
            skLineSegment(sketch, "E368", {"start": v(9228.12, 21397.17) * mm, "end": v(8546.54, 23648.8) * mm});
            skLineSegment(sketch, "E369", {"start": v(9256.83, 21405.86) * mm, "end": v(8583.95, 23628.78) * mm});
            skLineSegment(sketch, "E370", {"start": v(9271.19, 21410.2) * mm, "end": v(8602.65, 23618.77) * mm});
            skLineSegment(sketch, "E371", {"start": v(9357.33, 21436.28) * mm, "end": v(8714.87, 23558.7) * mm});
            skLineSegment(sketch, "E372", {"start": v(9288.42, 21415.42) * mm, "end": v(8625.1, 23606.76) * mm});
            skLineSegment(sketch, "E373", {"start": v(9386.04, 21444.97) * mm, "end": v(8752.27, 23538.68) * mm});
            skLineSegment(sketch, "E374", {"start": v(-555.06, 29916.66) * mm, "end": v(7885.74, 20220.31) * mm});
            skLineSegment(sketch, "E375", {"start": v(7885.74, 20220.31) * mm, "end": v(7849.46, 20094.46) * mm});
            skLineSegment(sketch, "E376", {"start": v(7849.46, 20094.46) * mm, "end": v(-620.1, 29823.84) * mm});
            skLineSegment(sketch, "E377", {"start": v(-620.1, 29823.84) * mm, "end": v(-555.06, 29916.66) * mm});
            skLineSegment(sketch, "E378", {"start": v(7849.46, 20094.46) * mm, "end": v(7885.66, 20220.35) * mm});
            skLineSegment(sketch, "E379", {"start": v(-2682.94, 29199.46) * mm, "end": v(-2636.22, 29286.74) * mm});
            skLineSegment(sketch, "E380", {"start": v(-555.06, 29916.66) * mm, "end": v(-620.1, 29823.84) * mm});
            skLineSegment(sketch, "E381", {"start": v(-620.1, 29823.84) * mm, "end": v(-2682.94, 29199.46) * mm});
            skLineSegment(sketch, "E382", {"start": v(3515.53, 38130.64) * mm, "end": v(3524.41, 38061.2) * mm});
            skLineSegment(sketch, "E383", {"start": v(3524.41, 38061.2) * mm, "end": v(743.5, 37705.2) * mm});
            skLineSegment(sketch, "E384", {"start": v(743.5, 37705.2) * mm, "end": v(743.46, 37705.55) * mm});
            skLineSegment(sketch, "E385", {"start": v(743.46, 37705.55) * mm, "end": v(-4686.9, 36060.36) * mm});
            skLineSegment(sketch, "E386", {"start": v(-4686.9, 36060.36) * mm, "end": v(-2636.07, 29286.24) * mm});
            skLineSegment(sketch, "E387", {"start": v(-2636.07, 29286.24) * mm, "end": v(-2682.94, 29199.46) * mm});
            skLineSegment(sketch, "E388", {"start": v(-2682.94, 29199.46) * mm, "end": v(-4757.89, 36053.23) * mm});
            skLineSegment(sketch, "E389", {"start": v(-4757.89, 36053.23) * mm, "end": v(-4774.2, 36107.06) * mm});
            skLineSegment(sketch, "E390", {"start": v(-4774.2, 36107.06) * mm, "end": v(-4774.18, 36107.06) * mm});
            skLineSegment(sketch, "E391", {"start": v(-4774.18, 36107.06) * mm, "end": v(-4774.19, 36107.07) * mm});
            skLineSegment(sketch, "E392", {"start": v(-4774.19, 36107.07) * mm, "end": v(-4750.75, 36114.16) * mm});
            skLineSegment(sketch, "E393", {"start": v(-4750.75, 36114.16) * mm, "end": v(734.23, 37775.9) * mm});
            skLineSegment(sketch, "E394", {"start": v(734.23, 37775.9) * mm, "end": v(734.61, 37774.63) * mm});
            skLineSegment(sketch, "E395", {"start": v(734.61, 37774.63) * mm, "end": v(3515.53, 38130.64) * mm});
            skLineSegment(sketch, "E396", {"start": v(3768.72, 38142.6) * mm, "end": v(3798.48, 38146.42) * mm});
            skLineSegment(sketch, "E397", {"start": v(3606.47, 38071.38) * mm, "end": v(3600.1, 38120.97) * mm});
            skLineSegment(sketch, "E398", {"start": v(3768.72, 38142.6) * mm, "end": v(3741.51, 38118.95) * mm});
            skLineSegment(sketch, "E399", {"start": v(3741.51, 38118.95) * mm, "end": v(3602.65, 38101.14) * mm});
            skLineSegment(sketch, "E400", {"start": v(3804.84, 38096.83) * mm, "end": v(3798.48, 38146.42) * mm});
            skLineSegment(sketch, "E401", {"start": v(3408.1, 38045.93) * mm, "end": v(3404.28, 38075.69) * mm});
            skLineSegment(sketch, "E402", {"start": v(3543.14, 38093.5) * mm, "end": v(3404.28, 38075.69) * mm});
            skLineSegment(sketch, "E403", {"start": v(3570.35, 38117.16) * mm, "end": v(3543.14, 38093.5) * mm});
            skLineSegment(sketch, "E404", {"start": v(3600.1, 38120.97) * mm, "end": v(3570.35, 38117.16) * mm});
            skLineSegment(sketch, "E405", {"start": v(3408.1, 38045.93) * mm, "end": v(4737.2, 38216.43) * mm});
            skLineSegment(sketch, "E406", {"start": v(3801.03, 38126.58) * mm, "end": v(3939.89, 38144.4) * mm});
            skLineSegment(sketch, "E407", {"start": v(3967.1, 38168.05) * mm, "end": v(3939.89, 38144.4) * mm});
            skLineSegment(sketch, "E408", {"start": v(3996.85, 38171.87) * mm, "end": v(3967.1, 38168.05) * mm});
            skLineSegment(sketch, "E409", {"start": v(4003.22, 38122.28) * mm, "end": v(3996.85, 38171.87) * mm});
            skLineSegment(sketch, "E410", {"start": v(4201.6, 38147.72) * mm, "end": v(4195.23, 38197.32) * mm});
            skLineSegment(sketch, "E411", {"start": v(4733.39, 38246.19) * mm, "end": v(4197.77, 38177.48) * mm});
            skLineSegment(sketch, "E412", {"start": v(3348.58, 38038.33) * mm, "end": v(3342.21, 38087.92) * mm});
            skLineSegment(sketch, "E413", {"start": v(3371.97, 38091.74) * mm, "end": v(3342.21, 38087.92) * mm});
            skLineSegment(sketch, "E414", {"start": v(3348.58, 38038.33) * mm, "end": v(3408.1, 38045.93) * mm});
            skLineSegment(sketch, "E415", {"start": v(3404.28, 38075.69) * mm, "end": v(3371.97, 38091.74) * mm});
            skLineSegment(sketch, "E416", {"start": v(4165.47, 38193.5) * mm, "end": v(4138.26, 38169.84) * mm});
            skLineSegment(sketch, "E417", {"start": v(4195.23, 38197.32) * mm, "end": v(4165.47, 38193.5) * mm});
            skLineSegment(sketch, "E418", {"start": v(4138.26, 38169.84) * mm, "end": v(3999.4, 38152.03) * mm});
            skLineSegment(sketch, "E419", {"start": v(4790.35, 38273.7) * mm, "end": v(4796.71, 38224.1) * mm});
            skLineSegment(sketch, "E420", {"start": v(4733.39, 38246.19) * mm, "end": v(4737.2, 38216.43) * mm});
            skLineSegment(sketch, "E421", {"start": v(4760.6, 38269.87) * mm, "end": v(4733.39, 38246.19) * mm});
            skLineSegment(sketch, "E422", {"start": v(4790.35, 38273.7) * mm, "end": v(4760.6, 38269.87) * mm});
            skLineSegment(sketch, "E423", {"start": v(4737.2, 38216.43) * mm, "end": v(4796.71, 38224.1) * mm});
            skLineSegment(sketch, "E424", {"start": v(2753.45, 37961.99) * mm, "end": v(2747.1, 38011.58) * mm});
            skLineSegment(sketch, "E425", {"start": v(2812.97, 37969.6) * mm, "end": v(2753.45, 37961.99) * mm});
            skLineSegment(sketch, "E426", {"start": v(2809.15, 37999.35) * mm, "end": v(2776.85, 38015.4) * mm});
            skLineSegment(sketch, "E427", {"start": v(2776.85, 38015.4) * mm, "end": v(2747.1, 38011.58) * mm});
            skLineSegment(sketch, "E428", {"start": v(2812.97, 37969.6) * mm, "end": v(3348.58, 38038.3) * mm});
            skLineSegment(sketch, "E429", {"start": v(2809.15, 37999.35) * mm, "end": v(2812.97, 37969.6) * mm});
            skLineSegment(sketch, "E430", {"start": v(3344.76, 38068.05) * mm, "end": v(2809.15, 37999.35) * mm});
            skLineSegment(sketch, "E431", {"start": v(3348.58, 38038.3) * mm, "end": v(3344.76, 38068.05) * mm});
            skLineSegment(sketch, "E432", {"start": v(2471.88, 26438.95) * mm, "end": v(2603.24, 26288.13) * mm});
            skLineSegment(sketch, "E433", {"start": v(2603.24, 26288.13) * mm, "end": v(2580.61, 26268.42) * mm});
            skLineSegment(sketch, "E434", {"start": v(2580.61, 26268.42) * mm, "end": v(2488.67, 26374) * mm});
            skLineSegment(sketch, "E435", {"start": v(2488.67, 26374) * mm, "end": v(2423.72, 26357.21) * mm});
            skLineSegment(sketch, "E436", {"start": v(2423.72, 26357.21) * mm, "end": v(2404.02, 26379.84) * mm});
            skLineSegment(sketch, "E437", {"start": v(2404.02, 26379.84) * mm, "end": v(2471.88, 26438.95) * mm});
            skLineSegment(sketch, "E438", {"start": v(2603.24, 26288.13) * mm, "end": v(2734.6, 26137.3) * mm});
            skLineSegment(sketch, "E439", {"start": v(2734.6, 26137.3) * mm, "end": v(2711.97, 26117.6) * mm});
            skLineSegment(sketch, "E440", {"start": v(2711.97, 26117.6) * mm, "end": v(2620.02, 26223.18) * mm});
            skLineSegment(sketch, "E441", {"start": v(2620.02, 26223.18) * mm, "end": v(2555.07, 26206.4) * mm});
            skLineSegment(sketch, "E442", {"start": v(2555.07, 26206.4) * mm, "end": v(2535.37, 26229.02) * mm});
            skLineSegment(sketch, "E443", {"start": v(2535.37, 26229.02) * mm, "end": v(2603.24, 26288.13) * mm});
            skLineSegment(sketch, "E444", {"start": v(2734.6, 26137.3) * mm, "end": v(2865.94, 25986.49) * mm});
            skLineSegment(sketch, "E445", {"start": v(2865.94, 25986.49) * mm, "end": v(2843.32, 25966.79) * mm});
            skLineSegment(sketch, "E446", {"start": v(2843.32, 25966.79) * mm, "end": v(2751.37, 26072.36) * mm});
            skLineSegment(sketch, "E447", {"start": v(2751.37, 26072.36) * mm, "end": v(2686.43, 26055.58) * mm});
            skLineSegment(sketch, "E448", {"start": v(2686.43, 26055.58) * mm, "end": v(2666.72, 26078.2) * mm});
            skLineSegment(sketch, "E449", {"start": v(2666.72, 26078.2) * mm, "end": v(2734.6, 26137.3) * mm});
            skLineSegment(sketch, "E450", {"start": v(2865.94, 25986.49) * mm, "end": v(2997.3, 25835.67) * mm});
            skLineSegment(sketch, "E451", {"start": v(2997.3, 25835.67) * mm, "end": v(2974.67, 25815.97) * mm});
            skLineSegment(sketch, "E452", {"start": v(2974.67, 25815.97) * mm, "end": v(2882.73, 25921.54) * mm});
            skLineSegment(sketch, "E453", {"start": v(2882.73, 25921.54) * mm, "end": v(2817.78, 25904.76) * mm});
            skLineSegment(sketch, "E454", {"start": v(2817.78, 25904.76) * mm, "end": v(2798.08, 25927.38) * mm});
            skLineSegment(sketch, "E455", {"start": v(2798.08, 25927.38) * mm, "end": v(2865.94, 25986.49) * mm});
            skLineSegment(sketch, "E456", {"start": v(2077.55, 26891.72) * mm, "end": v(2116.95, 26846.47) * mm});
            skLineSegment(sketch, "E457", {"start": v(2116.95, 26846.47) * mm, "end": v(2094.33, 26826.77) * mm});
            skLineSegment(sketch, "E458", {"start": v(2094.33, 26826.77) * mm, "end": v(2029.38, 26809.99) * mm});
            skLineSegment(sketch, "E459", {"start": v(2029.38, 26809.99) * mm, "end": v(2009.68, 26832.6) * mm});
            skLineSegment(sketch, "E460", {"start": v(2009.68, 26832.6) * mm, "end": v(2077.55, 26891.72) * mm});
            skLineSegment(sketch, "E461", {"start": v(2471.6, 26439.26) * mm, "end": v(2116.95, 26846.47) * mm});
            skLineSegment(sketch, "E462", {"start": v(2094.33, 26826.77) * mm, "end": v(2448.99, 26419.56) * mm});
            skLineSegment(sketch, "E463", {"start": v(2448.99, 26419.56) * mm, "end": v(2471.6, 26439.26) * mm});
            skLineSegment(sketch, "E464", {"start": v(3036.7, 25790.42) * mm, "end": v(2997.3, 25835.67) * mm});
            skLineSegment(sketch, "E465", {"start": v(2974.67, 25815.97) * mm, "end": v(2949.13, 25753.94) * mm});
            skLineSegment(sketch, "E466", {"start": v(2949.13, 25753.94) * mm, "end": v(2968.83, 25731.32) * mm});
            skLineSegment(sketch, "E467", {"start": v(2968.83, 25731.32) * mm, "end": v(3036.7, 25790.42) * mm});
            skLineSegment(sketch, "E468", {"start": v(3430.76, 25337.97) * mm, "end": v(3391.36, 25383.21) * mm});
            skLineSegment(sketch, "E469", {"start": v(3391.36, 25383.21) * mm, "end": v(3368.73, 25363.51) * mm});
            skLineSegment(sketch, "E470", {"start": v(3368.73, 25363.51) * mm, "end": v(3343.2, 25301.48) * mm});
            skLineSegment(sketch, "E471", {"start": v(3343.2, 25301.48) * mm, "end": v(3362.9, 25278.86) * mm});
            skLineSegment(sketch, "E472", {"start": v(3362.9, 25278.86) * mm, "end": v(3430.76, 25337.97) * mm});
            skLineSegment(sketch, "E473", {"start": v(3014.08, 25770.72) * mm, "end": v(3368.73, 25363.51) * mm});
            skLineSegment(sketch, "E474", {"start": v(3368.73, 25363.51) * mm, "end": v(3391.36, 25383.21) * mm});
            skLineSegment(sketch, "E475", {"start": v(3391.36, 25383.21) * mm, "end": v(3036.7, 25790.42) * mm});
            skLineSegment(sketch, "E476", {"start": v(3036.7, 25790.42) * mm, "end": v(3014.08, 25770.72) * mm});
            skLineSegment(sketch, "E477", {"start": v(-2910.05, 30088.31) * mm, "end": v(-2881.33, 30097) * mm});
            skLineSegment(sketch, "E478", {"start": v(-2881.33, 30097) * mm, "end": v(-2636.22, 29286.74) * mm});
            skLineSegment(sketch, "E479", {"start": v(-2636.22, 29286.74) * mm, "end": v(-2656.24, 29249.34) * mm});
            skLineSegment(sketch, "E480", {"start": v(-2656.24, 29249.34) * mm, "end": v(-2910.05, 30088.31) * mm});
            skLineSegment(sketch, "E481", {"start": v(-2088.4, 29452.6) * mm, "end": v(-2079.7, 29423.88) * mm});
            skLineSegment(sketch, "E482", {"start": v(-2079.7, 29423.88) * mm, "end": v(-2656.24, 29249.34) * mm});
            skLineSegment(sketch, "E483", {"start": v(-2656.24, 29249.34) * mm, "end": v(-2636.22, 29286.74) * mm});
            skLineSegment(sketch, "E484", {"start": v(-2636.22, 29286.74) * mm, "end": v(-2088.4, 29452.6) * mm});
            skLineSegment(sketch, "E485", {"start": v(-2030.96, 29469.96) * mm, "end": v(-2016.46, 29422.11) * mm});
            skLineSegment(sketch, "E486", {"start": v(-2016.46, 29422.11) * mm, "end": v(-2045.17, 29413.41) * mm});
            skLineSegment(sketch, "E487", {"start": v(-2045.17, 29413.41) * mm, "end": v(-2079.7, 29423.88) * mm});
            skLineSegment(sketch, "E488", {"start": v(-2079.7, 29423.88) * mm, "end": v(-2088.4, 29452.6) * mm});
            skLineSegment(sketch, "E489", {"start": v(-2088.4, 29452.6) * mm, "end": v(-2030.96, 29469.96) * mm});
            skLineSegment(sketch, "E490", {"start": v(-2898.85, 30154.38) * mm, "end": v(-2946.71, 30139.92) * mm});
            skLineSegment(sketch, "E491", {"start": v(-2946.71, 30139.92) * mm, "end": v(-2938.04, 30111.2) * mm});
            skLineSegment(sketch, "E492", {"start": v(-2938.04, 30111.2) * mm, "end": v(-2910.18, 30088.28) * mm});
            skLineSegment(sketch, "E493", {"start": v(-2910.18, 30088.28) * mm, "end": v(-2881.47, 30096.96) * mm});
            skLineSegment(sketch, "E494", {"start": v(-2881.47, 30096.96) * mm, "end": v(-2898.85, 30154.38) * mm});
            skLineSegment(sketch, "E495", {"start": v(-4686.52, 36060.6) * mm, "end": v(-4635.85, 35893.73) * mm});
            skLineSegment(sketch, "E496", {"start": v(-4635.85, 35893.73) * mm, "end": v(-4664.56, 35885.04) * mm});
            skLineSegment(sketch, "E497", {"start": v(-4664.56, 35885.04) * mm, "end": v(-4723.92, 36080.62) * mm});
            skLineSegment(sketch, "E498", {"start": v(-4723.92, 36080.62) * mm, "end": v(-4399.26, 36178.88) * mm});
            skLineSegment(sketch, "E499", {"start": v(-4399.26, 36178.88) * mm, "end": v(-4390.57, 36150.17) * mm});
            skLineSegment(sketch, "E500", {"start": v(-4390.57, 36150.17) * mm, "end": v(-4686.52, 36060.6) * mm});
            skLineSegment(sketch, "E501", {"start": v(-3950.3, 36283.42) * mm, "end": v(-4141.72, 36225.48) * mm});
            skLineSegment(sketch, "E502", {"start": v(-4141.72, 36225.48) * mm, "end": v(-4150.4, 36254.2) * mm});
            skLineSegment(sketch, "E503", {"start": v(-4150.4, 36254.2) * mm, "end": v(-4016.41, 36294.75) * mm});
            skLineSegment(sketch, "E504", {"start": v(-4016.41, 36294.75) * mm, "end": v(-3993.49, 36322.58) * mm});
            skLineSegment(sketch, "E505", {"start": v(-3993.49, 36322.58) * mm, "end": v(-3964.78, 36331.27) * mm});
            skLineSegment(sketch, "E506", {"start": v(-3964.78, 36331.27) * mm, "end": v(-3950.3, 36283.42) * mm});
            skLineSegment(sketch, "E507", {"start": v(-4141.72, 36225.48) * mm, "end": v(-4333.14, 36167.55) * mm});
            skLineSegment(sketch, "E508", {"start": v(-4333.14, 36167.55) * mm, "end": v(-4341.83, 36196.26) * mm});
            skLineSegment(sketch, "E509", {"start": v(-4341.83, 36196.26) * mm, "end": v(-4207.84, 36236.81) * mm});
            skLineSegment(sketch, "E510", {"start": v(-4207.84, 36236.81) * mm, "end": v(-4184.91, 36264.65) * mm});
            skLineSegment(sketch, "E511", {"start": v(-4184.91, 36264.65) * mm, "end": v(-4156.2, 36273.34) * mm});
            skLineSegment(sketch, "E512", {"start": v(-4156.2, 36273.34) * mm, "end": v(-4141.72, 36225.48) * mm});
            skLineSegment(sketch, "E513", {"start": v(-3758.87, 36341.35) * mm, "end": v(-3950.3, 36283.42) * mm});
            skLineSegment(sketch, "E514", {"start": v(-3950.3, 36283.42) * mm, "end": v(-3958.98, 36312.13) * mm});
            skLineSegment(sketch, "E515", {"start": v(-3958.98, 36312.13) * mm, "end": v(-3824.98, 36352.68) * mm});
            skLineSegment(sketch, "E516", {"start": v(-3824.98, 36352.68) * mm, "end": v(-3802.06, 36380.52) * mm});
            skLineSegment(sketch, "E517", {"start": v(-3802.06, 36380.52) * mm, "end": v(-3773.35, 36389.2) * mm});
            skLineSegment(sketch, "E518", {"start": v(-3773.35, 36389.2) * mm, "end": v(-3758.87, 36341.35) * mm});
            skLineSegment(sketch, "E519", {"start": v(-3050.6, 36555.7) * mm, "end": v(-3567.44, 36399.28) * mm});
            skLineSegment(sketch, "E520", {"start": v(-3567.44, 36399.28) * mm, "end": v(-3576.13, 36428) * mm});
            skLineSegment(sketch, "E521", {"start": v(-3576.13, 36428) * mm, "end": v(-3059.28, 36584.42) * mm});
            skLineSegment(sketch, "E522", {"start": v(-3059.28, 36584.42) * mm, "end": v(-3050.6, 36555.7) * mm});
            skLineSegment(sketch, "E523", {"start": v(-4405.06, 36198.05) * mm, "end": v(-4376.35, 36206.74) * mm});
            skLineSegment(sketch, "E524", {"start": v(-4376.35, 36206.74) * mm, "end": v(-4341.83, 36196.26) * mm});
            skLineSegment(sketch, "E525", {"start": v(-4341.83, 36196.26) * mm, "end": v(-4333.14, 36167.55) * mm});
            skLineSegment(sketch, "E526", {"start": v(-4333.14, 36167.55) * mm, "end": v(-4390.58, 36150.2) * mm});
            skLineSegment(sketch, "E527", {"start": v(-4390.58, 36150.2) * mm, "end": v(-4405.06, 36198.05) * mm});
            skLineSegment(sketch, "E528", {"start": v(-3567.44, 36399.28) * mm, "end": v(-3758.87, 36341.35) * mm});
            skLineSegment(sketch, "E529", {"start": v(-3758.87, 36341.35) * mm, "end": v(-3767.56, 36370.06) * mm});
            skLineSegment(sketch, "E530", {"start": v(-3767.56, 36370.06) * mm, "end": v(-3633.56, 36410.62) * mm});
            skLineSegment(sketch, "E531", {"start": v(-3633.56, 36410.62) * mm, "end": v(-3610.64, 36438.45) * mm});
            skLineSegment(sketch, "E532", {"start": v(-3610.64, 36438.45) * mm, "end": v(-3581.93, 36447.14) * mm});
            skLineSegment(sketch, "E533", {"start": v(-3581.93, 36447.14) * mm, "end": v(-3567.44, 36399.28) * mm});
            skLineSegment(sketch, "E534", {"start": v(-2993.18, 36573.12) * mm, "end": v(-3050.6, 36555.7) * mm});
            skLineSegment(sketch, "E535", {"start": v(-3050.6, 36555.7) * mm, "end": v(-3059.28, 36584.42) * mm});
            skLineSegment(sketch, "E536", {"start": v(-3059.28, 36584.42) * mm, "end": v(-3036.37, 36612.28) * mm});
            skLineSegment(sketch, "E537", {"start": v(-3036.37, 36612.28) * mm, "end": v(-3007.66, 36620.97) * mm});
            skLineSegment(sketch, "E538", {"start": v(-3007.66, 36620.97) * mm, "end": v(-2993.18, 36573.12) * mm});
            skLineSegment(sketch, "E539", {"start": v(-4619.02, 35836.13) * mm, "end": v(-4636.37, 35893.57) * mm});
            skLineSegment(sketch, "E540", {"start": v(-4636.37, 35893.57) * mm, "end": v(-4665.08, 35884.88) * mm});
            skLineSegment(sketch, "E541", {"start": v(-4665.08, 35884.88) * mm, "end": v(-4675.57, 35850.36) * mm});
            skLineSegment(sketch, "E542", {"start": v(-4675.57, 35850.36) * mm, "end": v(-4666.88, 35821.65) * mm});
            skLineSegment(sketch, "E543", {"start": v(-4666.88, 35821.65) * mm, "end": v(-4619.02, 35836.13) * mm});
            skLineSegment(sketch, "E544", {"start": v(-1686.93, 37020.72) * mm, "end": v(-1666.83, 37026.8) * mm});
            skLineSegment(sketch, "E545", {"start": v(-1718.45, 36990.25) * mm, "end": v(-1686.93, 37020.72) * mm});
            skLineSegment(sketch, "E546", {"start": v(-1709.76, 36961.54) * mm, "end": v(-1718.45, 36990.25) * mm});
            skLineSegment(sketch, "E547", {"start": v(-1652.34, 36978.95) * mm, "end": v(-1709.76, 36961.54) * mm});
            skLineSegment(sketch, "E548", {"start": v(-1666.83, 37026.8) * mm, "end": v(-1652.34, 36978.95) * mm});
            skLineSegment(sketch, "E549", {"start": v(-2452.62, 36788.96) * mm, "end": v(-2432.52, 36795.05) * mm});
            skLineSegment(sketch, "E550", {"start": v(-2484.15, 36758.5) * mm, "end": v(-2452.62, 36788.96) * mm});
            skLineSegment(sketch, "E551", {"start": v(-2475.46, 36729.78) * mm, "end": v(-2484.15, 36758.5) * mm});
            skLineSegment(sketch, "E552", {"start": v(-2418.04, 36747.2) * mm, "end": v(-2475.46, 36729.78) * mm});
            skLineSegment(sketch, "E553", {"start": v(-2432.52, 36795.05) * mm, "end": v(-2418.04, 36747.2) * mm});
            skLineSegment(sketch, "E554", {"start": v(6158.14, 38449.15) * mm, "end": v(6178.97, 38451.82) * mm});
            skLineSegment(sketch, "E555", {"start": v(6122, 38424.32) * mm, "end": v(6158.14, 38449.15) * mm});
            skLineSegment(sketch, "E556", {"start": v(6125.82, 38394.56) * mm, "end": v(6122, 38424.32) * mm});
            skLineSegment(sketch, "E557", {"start": v(6185.33, 38402.23) * mm, "end": v(6125.82, 38394.56) * mm});
            skLineSegment(sketch, "E558", {"start": v(6178.97, 38451.82) * mm, "end": v(6185.33, 38402.23) * mm});
            skLineSegment(sketch, "E559", {"start": v(5364.64, 38347.36) * mm, "end": v(5385.47, 38350.03) * mm});
            skLineSegment(sketch, "E560", {"start": v(5328.5, 38322.53) * mm, "end": v(5364.64, 38347.36) * mm});
            skLineSegment(sketch, "E561", {"start": v(5332.33, 38292.77) * mm, "end": v(5328.5, 38322.53) * mm});
            skLineSegment(sketch, "E562", {"start": v(5391.83, 38300.44) * mm, "end": v(5332.33, 38292.77) * mm});
            skLineSegment(sketch, "E563", {"start": v(5385.47, 38350.03) * mm, "end": v(5391.83, 38300.44) * mm});
            skLineSegment(sketch, "E564", {"start": v(2190.65, 37940.2) * mm, "end": v(2211.48, 37942.87) * mm});
            skLineSegment(sketch, "E565", {"start": v(2154.52, 37915.37) * mm, "end": v(2190.65, 37940.2) * mm});
            skLineSegment(sketch, "E566", {"start": v(2158.33, 37885.61) * mm, "end": v(2154.52, 37915.37) * mm});
            skLineSegment(sketch, "E567", {"start": v(2217.84, 37893.28) * mm, "end": v(2158.33, 37885.61) * mm});
            skLineSegment(sketch, "E568", {"start": v(2211.48, 37942.87) * mm, "end": v(2217.84, 37893.28) * mm});
            skLineSegment(sketch, "E569", {"start": v(1397.15, 37838.41) * mm, "end": v(1417.98, 37841.08) * mm});
            skLineSegment(sketch, "E570", {"start": v(1361.02, 37813.58) * mm, "end": v(1397.15, 37838.41) * mm});
            skLineSegment(sketch, "E571", {"start": v(1364.84, 37783.82) * mm, "end": v(1361.02, 37813.58) * mm});
            skLineSegment(sketch, "E572", {"start": v(1424.35, 37791.49) * mm, "end": v(1364.84, 37783.82) * mm});
            skLineSegment(sketch, "E573", {"start": v(1417.98, 37841.08) * mm, "end": v(1424.35, 37791.49) * mm});
            skLineSegment(sketch, "E574", {"start": v(-3807.12, 32982.54) * mm, "end": v(-3815.8, 33011.25) * mm});
            skLineSegment(sketch, "E575", {"start": v(-3710.01, 32834.31) * mm, "end": v(-3757.87, 32819.83) * mm});
            skLineSegment(sketch, "E576", {"start": v(-3807.12, 32982.54) * mm, "end": v(-3779.28, 32959.62) * mm});
            skLineSegment(sketch, "E577", {"start": v(-3779.28, 32959.62) * mm, "end": v(-3738.72, 32825.62) * mm});
            skLineSegment(sketch, "E578", {"start": v(-3767.95, 33025.74) * mm, "end": v(-3815.8, 33011.25) * mm});
            skLineSegment(sketch, "E579", {"start": v(-3652.07, 32642.9) * mm, "end": v(-3680.78, 32634.2) * mm});
            skLineSegment(sketch, "E580", {"start": v(-3721.34, 32768.2) * mm, "end": v(-3680.78, 32634.2) * mm});
            skLineSegment(sketch, "E581", {"start": v(-3749.18, 32791.12) * mm, "end": v(-3721.34, 32768.2) * mm});
            skLineSegment(sketch, "E582", {"start": v(-3757.87, 32819.83) * mm, "end": v(-3749.18, 32791.12) * mm});
            skLineSegment(sketch, "E583", {"start": v(-3652.07, 32642.9) * mm, "end": v(-4040.27, 33925.43) * mm});
            skLineSegment(sketch, "E584", {"start": v(-3796.66, 33017.05) * mm, "end": v(-3837.22, 33151.04) * mm});
            skLineSegment(sketch, "E585", {"start": v(-3865.06, 33173.96) * mm, "end": v(-3837.22, 33151.04) * mm});
            skLineSegment(sketch, "E586", {"start": v(-3873.75, 33202.68) * mm, "end": v(-3865.06, 33173.96) * mm});
            skLineSegment(sketch, "E587", {"start": v(-3825.9, 33217.16) * mm, "end": v(-3873.75, 33202.68) * mm});
            skLineSegment(sketch, "E588", {"start": v(-3883.83, 33408.58) * mm, "end": v(-3931.69, 33394.1) * mm});
            skLineSegment(sketch, "E589", {"start": v(-4068.98, 33916.74) * mm, "end": v(-3912.54, 33399.9) * mm});
            skLineSegment(sketch, "E590", {"start": v(-3634.72, 32585.45) * mm, "end": v(-3682.58, 32570.97) * mm});
            skLineSegment(sketch, "E591", {"start": v(-3691.27, 32599.68) * mm, "end": v(-3682.58, 32570.97) * mm});
            skLineSegment(sketch, "E592", {"start": v(-3634.72, 32585.45) * mm, "end": v(-3652.07, 32642.9) * mm});
            skLineSegment(sketch, "E593", {"start": v(-3680.78, 32634.2) * mm, "end": v(-3691.27, 32599.68) * mm});
            skLineSegment(sketch, "E594", {"start": v(-3923, 33365.39) * mm, "end": v(-3895.16, 33342.47) * mm});
            skLineSegment(sketch, "E595", {"start": v(-3931.69, 33394.1) * mm, "end": v(-3923, 33365.39) * mm});
            skLineSegment(sketch, "E596", {"start": v(-3895.16, 33342.47) * mm, "end": v(-3854.6, 33208.47) * mm});
            skLineSegment(sketch, "E597", {"start": v(-4105.54, 33968.36) * mm, "end": v(-4057.68, 33982.85) * mm});
            skLineSegment(sketch, "E598", {"start": v(-4068.98, 33916.74) * mm, "end": v(-4040.27, 33925.43) * mm});
            skLineSegment(sketch, "E599", {"start": v(-4096.85, 33939.65) * mm, "end": v(-4068.98, 33916.74) * mm});
            skLineSegment(sketch, "E600", {"start": v(-4105.54, 33968.36) * mm, "end": v(-4096.85, 33939.65) * mm});
            skLineSegment(sketch, "E601", {"start": v(-4040.27, 33925.43) * mm, "end": v(-4057.68, 33982.85) * mm});
            skLineSegment(sketch, "E602", {"start": v(-3460.9, 32011.18) * mm, "end": v(-3508.76, 31996.7) * mm});
            skLineSegment(sketch, "E603", {"start": v(-3478.25, 32068.62) * mm, "end": v(-3460.9, 32011.18) * mm});
            skLineSegment(sketch, "E604", {"start": v(-3506.96, 32059.93) * mm, "end": v(-3517.45, 32025.41) * mm});
            skLineSegment(sketch, "E605", {"start": v(-3517.45, 32025.41) * mm, "end": v(-3508.76, 31996.7) * mm});
            skLineSegment(sketch, "E606", {"start": v(-3478.25, 32068.62) * mm, "end": v(-3634.69, 32585.46) * mm});
            skLineSegment(sketch, "E607", {"start": v(-3506.96, 32059.93) * mm, "end": v(-3478.25, 32068.62) * mm});
            skLineSegment(sketch, "E608", {"start": v(-3663.4, 32576.77) * mm, "end": v(-3506.96, 32059.93) * mm});
            skLineSegment(sketch, "E609", {"start": v(-3634.69, 32585.46) * mm, "end": v(-3663.4, 32576.77) * mm});
            skLineSegment(sketch, "E610", {"start": v(-3460.87, 32011.2) * mm, "end": v(-3304.43, 31494.35) * mm});
            skLineSegment(sketch, "E611", {"start": v(-3304.43, 31494.35) * mm, "end": v(-3333.14, 31485.66) * mm});
            skLineSegment(sketch, "E612", {"start": v(-3333.14, 31485.66) * mm, "end": v(-3489.58, 32002.5) * mm});
            skLineSegment(sketch, "E613", {"start": v(-3489.58, 32002.5) * mm, "end": v(-3460.87, 32011.2) * mm});
            skLineSegment(sketch, "E614", {"start": v(-3120.56, 30714.16) * mm, "end": v(-3114.47, 30694.06) * mm});
            skLineSegment(sketch, "E615", {"start": v(-3114.47, 30694.06) * mm, "end": v(-3084, 30662.54) * mm});
            skLineSegment(sketch, "E616", {"start": v(-3084, 30662.54) * mm, "end": v(-3055.29, 30671.23) * mm});
            skLineSegment(sketch, "E617", {"start": v(-3055.29, 30671.23) * mm, "end": v(-3072.7, 30728.65) * mm});
            skLineSegment(sketch, "E618", {"start": v(-3072.7, 30728.65) * mm, "end": v(-3120.56, 30714.16) * mm});
            skLineSegment(sketch, "E619", {"start": v(-3055.29, 30671.23) * mm, "end": v(-2898.85, 30154.38) * mm});
            skLineSegment(sketch, "E620", {"start": v(-2898.85, 30154.38) * mm, "end": v(-2927.56, 30145.7) * mm});
            skLineSegment(sketch, "E621", {"start": v(-2927.56, 30145.7) * mm, "end": v(-3084, 30662.54) * mm});
            skLineSegment(sketch, "E622", {"start": v(-3334.94, 31422.43) * mm, "end": v(-3341.02, 31442.53) * mm});
            skLineSegment(sketch, "E623", {"start": v(-3341.02, 31442.53) * mm, "end": v(-3333.14, 31485.66) * mm});
            skLineSegment(sketch, "E624", {"start": v(-3333.14, 31485.66) * mm, "end": v(-3304.43, 31494.35) * mm});
            skLineSegment(sketch, "E625", {"start": v(-3304.43, 31494.35) * mm, "end": v(-3287.08, 31436.91) * mm});
            skLineSegment(sketch, "E626", {"start": v(-3287.08, 31436.91) * mm, "end": v(-3334.94, 31422.43) * mm});
            skLineSegment(sketch, "E627", {"start": v(-3287.05, 31436.92) * mm, "end": v(-3072.67, 30728.66) * mm});
            skLineSegment(sketch, "E628", {"start": v(-3072.67, 30728.66) * mm, "end": v(-3101.38, 30719.96) * mm});
            skLineSegment(sketch, "E629", {"start": v(-3101.38, 30719.96) * mm, "end": v(-3315.76, 31428.23) * mm});
            skLineSegment(sketch, "E630", {"start": v(-3315.76, 31428.23) * mm, "end": v(-3287.05, 31436.92) * mm});
            skLineSegment(sketch, "E631", {"start": v(-4619.67, 35839.66) * mm, "end": v(-4463.23, 35322.82) * mm});
            skLineSegment(sketch, "E632", {"start": v(-4463.23, 35322.82) * mm, "end": v(-4491.94, 35314.13) * mm});
            skLineSegment(sketch, "E633", {"start": v(-4491.94, 35314.13) * mm, "end": v(-4648.38, 35830.97) * mm});
            skLineSegment(sketch, "E634", {"start": v(-4648.38, 35830.97) * mm, "end": v(-4619.67, 35839.66) * mm});
            skLineSegment(sketch, "E635", {"start": v(-4279.36, 34542.63) * mm, "end": v(-4273.27, 34522.53) * mm});
            skLineSegment(sketch, "E636", {"start": v(-4273.27, 34522.53) * mm, "end": v(-4242.8, 34491) * mm});
            skLineSegment(sketch, "E637", {"start": v(-4242.8, 34491) * mm, "end": v(-4214.09, 34499.7) * mm});
            skLineSegment(sketch, "E638", {"start": v(-4214.09, 34499.7) * mm, "end": v(-4231.5, 34557.12) * mm});
            skLineSegment(sketch, "E639", {"start": v(-4231.5, 34557.12) * mm, "end": v(-4279.36, 34542.63) * mm});
            skLineSegment(sketch, "E640", {"start": v(-4214.09, 34499.7) * mm, "end": v(-4057.65, 33982.85) * mm});
            skLineSegment(sketch, "E641", {"start": v(-4057.65, 33982.85) * mm, "end": v(-4086.36, 33974.16) * mm});
            skLineSegment(sketch, "E642", {"start": v(-4086.36, 33974.16) * mm, "end": v(-4242.8, 34491) * mm});
            skLineSegment(sketch, "E643", {"start": v(-4493.74, 35250.9) * mm, "end": v(-4499.82, 35271) * mm});
            skLineSegment(sketch, "E644", {"start": v(-4499.82, 35271) * mm, "end": v(-4491.94, 35314.13) * mm});
            skLineSegment(sketch, "E645", {"start": v(-4491.94, 35314.13) * mm, "end": v(-4463.23, 35322.82) * mm});
            skLineSegment(sketch, "E646", {"start": v(-4463.23, 35322.82) * mm, "end": v(-4445.88, 35265.38) * mm});
            skLineSegment(sketch, "E647", {"start": v(-4445.88, 35265.38) * mm, "end": v(-4493.74, 35250.9) * mm});
            skLineSegment(sketch, "E648", {"start": v(-4445.85, 35265.4) * mm, "end": v(-4231.47, 34557.13) * mm});
            skLineSegment(sketch, "E649", {"start": v(-4231.47, 34557.13) * mm, "end": v(-4260.18, 34548.43) * mm});
            skLineSegment(sketch, "E650", {"start": v(-4260.18, 34548.43) * mm, "end": v(-4474.56, 35256.7) * mm});
            skLineSegment(sketch, "E651", {"start": v(-4474.56, 35256.7) * mm, "end": v(-4445.85, 35265.4) * mm});
            skLineSegment(sketch, "E652", {"start": v(-153.2, 29455.34) * mm, "end": v(-21.85, 29304.52) * mm});
            skLineSegment(sketch, "E653", {"start": v(-21.85, 29304.52) * mm, "end": v(-44.47, 29284.82) * mm});
            skLineSegment(sketch, "E654", {"start": v(-44.47, 29284.82) * mm, "end": v(-136.42, 29390.4) * mm});
            skLineSegment(sketch, "E655", {"start": v(-136.42, 29390.4) * mm, "end": v(-201.37, 29373.61) * mm});
            skLineSegment(sketch, "E656", {"start": v(-201.37, 29373.61) * mm, "end": v(-221.07, 29396.23) * mm});
            skLineSegment(sketch, "E657", {"start": v(-221.07, 29396.23) * mm, "end": v(-153.2, 29455.34) * mm});
            skLineSegment(sketch, "E658", {"start": v(-21.85, 29304.52) * mm, "end": v(109.5, 29153.7) * mm});
            skLineSegment(sketch, "E659", {"start": v(109.5, 29153.7) * mm, "end": v(86.88, 29134) * mm});
            skLineSegment(sketch, "E660", {"start": v(86.88, 29134) * mm, "end": v(-5.06, 29239.58) * mm});
            skLineSegment(sketch, "E661", {"start": v(-5.06, 29239.58) * mm, "end": v(-70.01, 29222.8) * mm});
            skLineSegment(sketch, "E662", {"start": v(-70.01, 29222.8) * mm, "end": v(-89.72, 29245.41) * mm});
            skLineSegment(sketch, "E663", {"start": v(-89.72, 29245.41) * mm, "end": v(-21.85, 29304.52) * mm});
            skLineSegment(sketch, "E664", {"start": v(109.5, 29153.7) * mm, "end": v(240.86, 29002.89) * mm});
            skLineSegment(sketch, "E665", {"start": v(240.86, 29002.89) * mm, "end": v(218.24, 28983.18) * mm});
            skLineSegment(sketch, "E666", {"start": v(218.24, 28983.18) * mm, "end": v(126.29, 29088.76) * mm});
            skLineSegment(sketch, "E667", {"start": v(126.29, 29088.76) * mm, "end": v(61.34, 29071.97) * mm});
            skLineSegment(sketch, "E668", {"start": v(61.34, 29071.97) * mm, "end": v(41.64, 29094.6) * mm});
            skLineSegment(sketch, "E669", {"start": v(41.64, 29094.6) * mm, "end": v(109.5, 29153.7) * mm});
            skLineSegment(sketch, "E670", {"start": v(240.86, 29002.89) * mm, "end": v(372.21, 28852.07) * mm});
            skLineSegment(sketch, "E671", {"start": v(372.21, 28852.07) * mm, "end": v(349.6, 28832.36) * mm});
            skLineSegment(sketch, "E672", {"start": v(349.6, 28832.36) * mm, "end": v(257.64, 28937.94) * mm});
            skLineSegment(sketch, "E673", {"start": v(257.64, 28937.94) * mm, "end": v(192.7, 28921.15) * mm});
            skLineSegment(sketch, "E674", {"start": v(192.7, 28921.15) * mm, "end": v(173, 28943.78) * mm});
            skLineSegment(sketch, "E675", {"start": v(173, 28943.78) * mm, "end": v(240.86, 29002.89) * mm});
            skLineSegment(sketch, "E676", {"start": v(805.68, 28354.37) * mm, "end": v(766.27, 28399.61) * mm});
            skLineSegment(sketch, "E677", {"start": v(766.27, 28399.61) * mm, "end": v(743.65, 28379.9) * mm});
            skLineSegment(sketch, "E678", {"start": v(743.65, 28379.9) * mm, "end": v(718.1, 28317.88) * mm});
            skLineSegment(sketch, "E679", {"start": v(718.1, 28317.88) * mm, "end": v(737.81, 28295.26) * mm});
            skLineSegment(sketch, "E680", {"start": v(737.81, 28295.26) * mm, "end": v(805.68, 28354.37) * mm});
            skLineSegment(sketch, "E681", {"start": v(-746.88, 29857.19) * mm, "end": v(-689.47, 29874.62) * mm});
            skLineSegment(sketch, "E682", {"start": v(-689.47, 29874.62) * mm, "end": v(-680.75, 29845.92) * mm});
            skLineSegment(sketch, "E683", {"start": v(-680.75, 29845.92) * mm, "end": v(-703.64, 29818.06) * mm});
            skLineSegment(sketch, "E684", {"start": v(-703.64, 29818.06) * mm, "end": v(-732.35, 29809.35) * mm});
            skLineSegment(sketch, "E685", {"start": v(-732.35, 29809.35) * mm, "end": v(-746.88, 29857.19) * mm});
            skLineSegment(sketch, "E686", {"start": v(-553.53, 29915.74) * mm, "end": v(-153.14, 29455.4) * mm});
            skLineSegment(sketch, "E687", {"start": v(-153.14, 29455.4) * mm, "end": v(-175.77, 29435.7) * mm});
            skLineSegment(sketch, "E688", {"start": v(-175.77, 29435.7) * mm, "end": v(-563.4, 29881.4) * mm});
            skLineSegment(sketch, "E689", {"start": v(-563.4, 29881.4) * mm, "end": v(-553.53, 29915.74) * mm});
            skLineSegment(sketch, "E690", {"start": v(411.62, 28806.82) * mm, "end": v(766.27, 28399.61) * mm});
            skLineSegment(sketch, "E691", {"start": v(743.65, 28379.9) * mm, "end": v(389, 28787.12) * mm});
            skLineSegment(sketch, "E692", {"start": v(389, 28787.12) * mm, "end": v(411.62, 28806.82) * mm});
            skLineSegment(sketch, "E693", {"start": v(411.62, 28806.82) * mm, "end": v(372.21, 28852.07) * mm});
            skLineSegment(sketch, "E694", {"start": v(349.6, 28832.36) * mm, "end": v(324.05, 28770.34) * mm});
            skLineSegment(sketch, "E695", {"start": v(324.05, 28770.34) * mm, "end": v(343.75, 28747.71) * mm});
            skLineSegment(sketch, "E696", {"start": v(343.75, 28747.71) * mm, "end": v(411.62, 28806.82) * mm});
            skLineSegment(sketch, "E697", {"start": v(-563.49, 29881.36) * mm, "end": v(-680.75, 29845.92) * mm});
            skLineSegment(sketch, "E698", {"start": v(-680.75, 29845.92) * mm, "end": v(-689.47, 29874.62) * mm});
            skLineSegment(sketch, "E699", {"start": v(-689.47, 29874.62) * mm, "end": v(-553.62, 29915.71) * mm});
            skLineSegment(sketch, "E700", {"start": v(-553.62, 29915.71) * mm, "end": v(-563.49, 29881.36) * mm});
            skLineSegment(sketch, "E701", {"start": v(-1512.57, 29625.43) * mm, "end": v(-1455.16, 29642.86) * mm});
            skLineSegment(sketch, "E702", {"start": v(-1455.16, 29642.86) * mm, "end": v(-1446.44, 29614.16) * mm});
            skLineSegment(sketch, "E703", {"start": v(-1446.44, 29614.16) * mm, "end": v(-1469.34, 29586.3) * mm});
            skLineSegment(sketch, "E704", {"start": v(-1469.34, 29586.3) * mm, "end": v(-1498.04, 29577.59) * mm});
            skLineSegment(sketch, "E705", {"start": v(-1498.04, 29577.59) * mm, "end": v(-1512.57, 29625.43) * mm});
            skLineSegment(sketch, "E706", {"start": v(7764.12, 20360.02) * mm, "end": v(7885.67, 20220.4) * mm});
            skLineSegment(sketch, "E707", {"start": v(7885.67, 20220.4) * mm, "end": v(7875.8, 20186.04) * mm});
            skLineSegment(sketch, "E708", {"start": v(7875.8, 20186.04) * mm, "end": v(7741.5, 20340.33) * mm});
            skLineSegment(sketch, "E709", {"start": v(7741.5, 20340.33) * mm, "end": v(7764.12, 20360.02) * mm});
            skLineSegment(sketch, "E710", {"start": v(8010.52, 20226.75) * mm, "end": v(7875.85, 20185.9) * mm});
            skLineSegment(sketch, "E711", {"start": v(7875.85, 20185.9) * mm, "end": v(7885.74, 20220.31) * mm});
            skLineSegment(sketch, "E712", {"start": v(7885.74, 20220.31) * mm, "end": v(8001.8, 20255.46) * mm});
            skLineSegment(sketch, "E713", {"start": v(8001.8, 20255.46) * mm, "end": v(8010.52, 20226.75) * mm});
            skLineSegment(sketch, "E714", {"start": v(7330.78, 20857.83) * mm, "end": v(7370.16, 20812.57) * mm});
            skLineSegment(sketch, "E715", {"start": v(7370.16, 20812.57) * mm, "end": v(7347.53, 20792.88) * mm});
            skLineSegment(sketch, "E716", {"start": v(7347.53, 20792.88) * mm, "end": v(7282.58, 20776.12) * mm});
            skLineSegment(sketch, "E717", {"start": v(7282.58, 20776.12) * mm, "end": v(7262.88, 20798.76) * mm});
            skLineSegment(sketch, "E718", {"start": v(7262.88, 20798.76) * mm, "end": v(7330.78, 20857.83) * mm});
            skLineSegment(sketch, "E719", {"start": v(7702, 20385.5) * mm, "end": v(7347.53, 20792.88) * mm});
            skLineSegment(sketch, "E720", {"start": v(7347.53, 20792.88) * mm, "end": v(7370.16, 20812.57) * mm});
            skLineSegment(sketch, "E721", {"start": v(7370.16, 20812.57) * mm, "end": v(7724.62, 20405.19) * mm});
            skLineSegment(sketch, "E722", {"start": v(7724.62, 20405.19) * mm, "end": v(7702, 20385.5) * mm});
            skLineSegment(sketch, "E723", {"start": v(7724.62, 20405.19) * mm, "end": v(7764, 20359.92) * mm});
            skLineSegment(sketch, "E724", {"start": v(7764, 20359.92) * mm, "end": v(7741.38, 20340.23) * mm});
            skLineSegment(sketch, "E725", {"start": v(7741.38, 20340.23) * mm, "end": v(7676.42, 20323.48) * mm});
            skLineSegment(sketch, "E726", {"start": v(7676.42, 20323.48) * mm, "end": v(7656.73, 20346.11) * mm});
            skLineSegment(sketch, "E727", {"start": v(7656.73, 20346.11) * mm, "end": v(7724.62, 20405.19) * mm});
            skLineSegment(sketch, "E728", {"start": v(9002.11, 20506.02) * mm, "end": v(8973.4, 20497.33) * mm});
            skLineSegment(sketch, "E729", {"start": v(9150.34, 20603.13) * mm, "end": v(9164.82, 20555.27) * mm});
            skLineSegment(sketch, "E730", {"start": v(9002.11, 20506.02) * mm, "end": v(9025.03, 20533.86) * mm});
            skLineSegment(sketch, "E731", {"start": v(9025.03, 20533.86) * mm, "end": v(9159.03, 20574.42) * mm});
            skLineSegment(sketch, "E732", {"start": v(8958.91, 20545.19) * mm, "end": v(8973.4, 20497.33) * mm});
            skLineSegment(sketch, "E733", {"start": v(9341.76, 20661.07) * mm, "end": v(9350.45, 20632.36) * mm});
            skLineSegment(sketch, "E734", {"start": v(9216.45, 20591.8) * mm, "end": v(9350.45, 20632.36) * mm});
            skLineSegment(sketch, "E735", {"start": v(9193.54, 20563.96) * mm, "end": v(9216.45, 20591.8) * mm});
            skLineSegment(sketch, "E736", {"start": v(9164.82, 20555.27) * mm, "end": v(9193.54, 20563.96) * mm});
            skLineSegment(sketch, "E737", {"start": v(9341.76, 20661.07) * mm, "end": v(8059.22, 20272.87) * mm});
            skLineSegment(sketch, "E738", {"start": v(8967.6, 20516.48) * mm, "end": v(8833.6, 20475.92) * mm});
            skLineSegment(sketch, "E739", {"start": v(8810.69, 20448.08) * mm, "end": v(8833.6, 20475.92) * mm});
            skLineSegment(sketch, "E740", {"start": v(8781.97, 20439.4) * mm, "end": v(8810.69, 20448.08) * mm});
            skLineSegment(sketch, "E741", {"start": v(8767.49, 20487.25) * mm, "end": v(8781.97, 20439.4) * mm});
            skLineSegment(sketch, "E742", {"start": v(8576.07, 20429.3) * mm, "end": v(8590.55, 20381.45) * mm});
            skLineSegment(sketch, "E743", {"start": v(8067.91, 20244.16) * mm, "end": v(8584.76, 20400.6) * mm});
            skLineSegment(sketch, "E744", {"start": v(9399.2, 20678.42) * mm, "end": v(9413.68, 20630.56) * mm});
            skLineSegment(sketch, "E745", {"start": v(9384.97, 20621.87) * mm, "end": v(9413.68, 20630.56) * mm});
            skLineSegment(sketch, "E746", {"start": v(9399.2, 20678.42) * mm, "end": v(9341.76, 20661.07) * mm});
            skLineSegment(sketch, "E747", {"start": v(9350.45, 20632.36) * mm, "end": v(9384.97, 20621.87) * mm});
            skLineSegment(sketch, "E748", {"start": v(8619.26, 20390.14) * mm, "end": v(8642.18, 20417.98) * mm});
            skLineSegment(sketch, "E749", {"start": v(8590.55, 20381.45) * mm, "end": v(8619.26, 20390.14) * mm});
            skLineSegment(sketch, "E750", {"start": v(8642.18, 20417.98) * mm, "end": v(8776.18, 20458.54) * mm});
            skLineSegment(sketch, "E751", {"start": v(8016.29, 20207.6) * mm, "end": v(8001.8, 20255.46) * mm});
            skLineSegment(sketch, "E752", {"start": v(8067.91, 20244.16) * mm, "end": v(8059.22, 20272.87) * mm});
            skLineSegment(sketch, "E753", {"start": v(8045, 20216.3) * mm, "end": v(8067.91, 20244.16) * mm});
            skLineSegment(sketch, "E754", {"start": v(8016.29, 20207.6) * mm, "end": v(8045, 20216.3) * mm});
            skLineSegment(sketch, "E755", {"start": v(8059.22, 20272.87) * mm, "end": v(8001.8, 20255.46) * mm});
            skLineSegment(sketch, "E756", {"start": v(9973.47, 20852.24) * mm, "end": v(9987.95, 20804.38) * mm});
            skLineSegment(sketch, "E757", {"start": v(9916.03, 20834.89) * mm, "end": v(9973.47, 20852.24) * mm});
            skLineSegment(sketch, "E758", {"start": v(9924.72, 20806.18) * mm, "end": v(9959.24, 20795.7) * mm});
            skLineSegment(sketch, "E759", {"start": v(9959.24, 20795.7) * mm, "end": v(9987.95, 20804.38) * mm});
            skLineSegment(sketch, "E760", {"start": v(9916.03, 20834.89) * mm, "end": v(9399.19, 20678.45) * mm});
            skLineSegment(sketch, "E761", {"start": v(9924.72, 20806.18) * mm, "end": v(9916.03, 20834.89) * mm});
            skLineSegment(sketch, "E762", {"start": v(9407.88, 20649.74) * mm, "end": v(9924.72, 20806.18) * mm});
            skLineSegment(sketch, "E763", {"start": v(9399.19, 20678.45) * mm, "end": v(9407.88, 20649.74) * mm});
            skLineSegment(sketch, "E764", {"start": v(943.88, 28134.12) * mm, "end": v(907.34, 27823.05) * mm});
            skArc(sketch, "E765", {"start": v(907.34, 27823.05) * mm, "mid": v(891.7, 27809.1) * mm, "end": v(877.38, 27824.4) * mm});
            skLineSegment(sketch, "E766", {"start": v(877.38, 27824.4) * mm, "end": v(884.1, 28138.26) * mm});
            skArc(sketch, "E767", {"start": v(884.1, 28138.26) * mm, "mid": v(916.16, 28167.55) * mm, "end": v(943.88, 28134.12) * mm});
            skLineSegment(sketch, "E768", {"start": v(1318.13, 27704.2) * mm, "end": v(1281.6, 27393.13) * mm});
            skArc(sketch, "E769", {"start": v(1281.6, 27393.13) * mm, "mid": v(1265.96, 27379.18) * mm, "end": v(1251.64, 27394.49) * mm});
            skLineSegment(sketch, "E770", {"start": v(1251.64, 27394.49) * mm, "end": v(1258.34, 27708.34) * mm});
            skArc(sketch, "E771", {"start": v(1258.34, 27708.34) * mm, "mid": v(1290.41, 27737.62) * mm, "end": v(1318.13, 27704.2) * mm});
            skLineSegment(sketch, "E772", {"start": v(1692.39, 27274.27) * mm, "end": v(1655.85, 26963.2) * mm});
            skArc(sketch, "E773", {"start": v(1655.85, 26963.2) * mm, "mid": v(1640.2, 26949.26) * mm, "end": v(1625.9, 26964.56) * mm});
            skLineSegment(sketch, "E774", {"start": v(1625.9, 26964.56) * mm, "end": v(1632.6, 27278.41) * mm});
            skArc(sketch, "E775", {"start": v(1632.6, 27278.41) * mm, "mid": v(1664.66, 27307.7) * mm, "end": v(1692.39, 27274.27) * mm});
            skLineSegment(sketch, "E776", {"start": v(3570.31, 25115.21) * mm, "end": v(3533.78, 24804.15) * mm});
            skArc(sketch, "E777", {"start": v(3533.78, 24804.15) * mm, "mid": v(3518.13, 24790.2) * mm, "end": v(3503.82, 24805.5) * mm});
            skLineSegment(sketch, "E778", {"start": v(3503.82, 24805.5) * mm, "end": v(3510.52, 25119.35) * mm});
            skArc(sketch, "E779", {"start": v(3510.52, 25119.35) * mm, "mid": v(3542.59, 25148.64) * mm, "end": v(3570.31, 25115.21) * mm});
            skLineSegment(sketch, "E780", {"start": v(3944.57, 24685.3) * mm, "end": v(3908.03, 24374.23) * mm});
            skArc(sketch, "E781", {"start": v(3908.03, 24374.23) * mm, "mid": v(3892.39, 24360.28) * mm, "end": v(3878.07, 24375.58) * mm});
            skLineSegment(sketch, "E782", {"start": v(3878.07, 24375.58) * mm, "end": v(3884.78, 24689.43) * mm});
            skArc(sketch, "E783", {"start": v(3884.78, 24689.43) * mm, "mid": v(3916.84, 24718.72) * mm, "end": v(3944.57, 24685.3) * mm});
            skLineSegment(sketch, "E784", {"start": v(4318.82, 24255.37) * mm, "end": v(4282.28, 23944.3) * mm});
            skArc(sketch, "E785", {"start": v(4282.28, 23944.3) * mm, "mid": v(4266.64, 23930.35) * mm, "end": v(4252.32, 23945.66) * mm});
            skLineSegment(sketch, "E786", {"start": v(4252.32, 23945.66) * mm, "end": v(4259.03, 24259.5) * mm});
            skArc(sketch, "E787", {"start": v(4259.03, 24259.5) * mm, "mid": v(4291.1, 24288.8) * mm, "end": v(4318.82, 24255.37) * mm});
            skLineSegment(sketch, "E788", {"start": v(6197.68, 22098.83) * mm, "end": v(6161.14, 21787.76) * mm});
            skArc(sketch, "E789", {"start": v(6161.14, 21787.76) * mm, "mid": v(6145.5, 21773.81) * mm, "end": v(6131.18, 21789.12) * mm});
            skLineSegment(sketch, "E790", {"start": v(6131.18, 21789.12) * mm, "end": v(6137.9, 22102.97) * mm});
            skArc(sketch, "E791", {"start": v(6137.9, 22102.97) * mm, "mid": v(6169.96, 22132.25) * mm, "end": v(6197.68, 22098.83) * mm});
            skLineSegment(sketch, "E792", {"start": v(6571.93, 21668.9) * mm, "end": v(6535.4, 21357.84) * mm});
            skArc(sketch, "E793", {"start": v(6535.4, 21357.84) * mm, "mid": v(6519.76, 21343.89) * mm, "end": v(6505.44, 21359.2) * mm});
            skLineSegment(sketch, "E794", {"start": v(6505.44, 21359.2) * mm, "end": v(6512.15, 21673.04) * mm});
            skArc(sketch, "E795", {"start": v(6512.15, 21673.04) * mm, "mid": v(6544.21, 21702.33) * mm, "end": v(6571.93, 21668.9) * mm});
            skLineSegment(sketch, "E796", {"start": v(6946.19, 21238.98) * mm, "end": v(6909.65, 20927.92) * mm});
            skArc(sketch, "E797", {"start": v(6909.65, 20927.92) * mm, "mid": v(6894.01, 20913.97) * mm, "end": v(6879.7, 20929.27) * mm});
            skLineSegment(sketch, "E798", {"start": v(6879.7, 20929.27) * mm, "end": v(6886.4, 21243.12) * mm});
            skArc(sketch, "E799", {"start": v(6886.4, 21243.12) * mm, "mid": v(6918.47, 21272.4) * mm, "end": v(6946.19, 21238.98) * mm});
            skLineSegment(sketch, "E800", {"start": v(-1121.68, 37191.78) * mm, "end": v(-1087.16, 37181.3) * mm});
            skLineSegment(sketch, "E801", {"start": v(-1121.68, 37191.78) * mm, "end": v(-1150.4, 37183.08) * mm});
            skLineSegment(sketch, "E802", {"start": v(-1135.9, 37135.23) * mm, "end": v(-1078.47, 37152.58) * mm});
            skLineSegment(sketch, "E803", {"start": v(-1150.4, 37183.08) * mm, "end": v(-1135.9, 37135.23) * mm});
            skLineSegment(sketch, "E804", {"start": v(195.39, 37569.46) * mm, "end": v(61.39, 37528.9) * mm});
            skLineSegment(sketch, "E805", {"start": v(218.3, 37597.29) * mm, "end": v(195.39, 37569.46) * mm});
            skLineSegment(sketch, "E806", {"start": v(247.02, 37605.98) * mm, "end": v(218.3, 37597.29) * mm});
            skLineSegment(sketch, "E807", {"start": v(61.39, 37528.9) * mm, "end": v(70.08, 37500.19) * mm});
            skLineSegment(sketch, "E808", {"start": v(-512.89, 37355.1) * mm, "end": v(-504.2, 37326.38) * mm});
            skLineSegment(sketch, "E809", {"start": v(-378.89, 37395.65) * mm, "end": v(-512.89, 37355.1) * mm});
            skLineSegment(sketch, "E810", {"start": v(-355.97, 37423.48) * mm, "end": v(-378.89, 37395.65) * mm});
            skLineSegment(sketch, "E811", {"start": v(-327.25, 37432.17) * mm, "end": v(-355.97, 37423.48) * mm});
            skLineSegment(sketch, "E812", {"start": v(-312.77, 37384.32) * mm, "end": v(-327.25, 37432.17) * mm});
            skLineSegment(sketch, "E813", {"start": v(-187.46, 37453.58) * mm, "end": v(-164.54, 37481.42) * mm});
            skLineSegment(sketch, "E814", {"start": v(-187.46, 37453.58) * mm, "end": v(-321.46, 37413.03) * mm});
            skLineSegment(sketch, "E815", {"start": v(-135.83, 37490.1) * mm, "end": v(-164.54, 37481.42) * mm});
            skLineSegment(sketch, "E816", {"start": v(-121.35, 37442.25) * mm, "end": v(-135.83, 37490.1) * mm});
            skLineSegment(sketch, "E817", {"start": v(-504.2, 37326.38) * mm, "end": v(70.08, 37500.19) * mm});
            skLineSegment(sketch, "E818", {"start": v(3.96, 37511.52) * mm, "end": v(-130.04, 37470.96) * mm});
            skLineSegment(sketch, "E819", {"start": v(26.88, 37539.35) * mm, "end": v(3.96, 37511.52) * mm});
            skLineSegment(sketch, "E820", {"start": v(55.6, 37548.04) * mm, "end": v(26.88, 37539.35) * mm});
            skLineSegment(sketch, "E821", {"start": v(70.08, 37500.19) * mm, "end": v(55.6, 37548.04) * mm});
            skLineSegment(sketch, "E822", {"start": v(70.08, 37500.19) * mm, "end": v(778.35, 37714.56) * mm});
            skLineSegment(sketch, "E823", {"start": v(247.02, 37605.98) * mm, "end": v(261.5, 37558.13) * mm});
            skLineSegment(sketch, "E824", {"start": v(769.66, 37743.28) * mm, "end": v(252.81, 37586.84) * mm});
            skLineSegment(sketch, "E825", {"start": v(778.35, 37714.56) * mm, "end": v(769.66, 37743.28) * mm});
            skLineSegment(sketch, "E826", {"start": v(-512.89, 37355.1) * mm, "end": v(-547.4, 37365.58) * mm});
            skLineSegment(sketch, "E827", {"start": v(-547.4, 37365.58) * mm, "end": v(-576.12, 37356.89) * mm});
            skLineSegment(sketch, "E828", {"start": v(-561.63, 37309.03) * mm, "end": v(-504.2, 37326.38) * mm});
            skLineSegment(sketch, "E829", {"start": v(-576.12, 37356.89) * mm, "end": v(-561.62, 37309) * mm});
            skLineSegment(sketch, "E830", {"start": v(822.42, 37764.68) * mm, "end": v(828.78, 37715.1) * mm});
            skLineSegment(sketch, "E831", {"start": v(769.27, 37707.42) * mm, "end": v(765.45, 37737.18) * mm});
            skLineSegment(sketch, "E832", {"start": v(792.66, 37760.87) * mm, "end": v(765.45, 37737.18) * mm});
            skLineSegment(sketch, "E833", {"start": v(822.42, 37764.68) * mm, "end": v(792.66, 37760.87) * mm});
            skLineSegment(sketch, "E834", {"start": v(769.27, 37707.42) * mm, "end": v(828.78, 37715.1) * mm});
            skLineSegment(sketch, "E835", {"start": v(-561.62, 37309) * mm, "end": v(-1078.47, 37152.58) * mm});
            skLineSegment(sketch, "E836", {"start": v(-570.31, 37337.72) * mm, "end": v(-1087.16, 37181.3) * mm});
            skLineSegment(sketch, "E837", {"start": v(-1087.16, 37181.3) * mm, "end": v(-1078.47, 37152.58) * mm});
            skLineSegment(sketch, "E838", {"start": v(5098.23, 23421.94) * mm, "end": v(5229.58, 23271.12) * mm});
            skLineSegment(sketch, "E839", {"start": v(5229.58, 23271.12) * mm, "end": v(5206.96, 23251.42) * mm});
            skLineSegment(sketch, "E840", {"start": v(5206.96, 23251.42) * mm, "end": v(5115, 23357) * mm});
            skLineSegment(sketch, "E841", {"start": v(5115, 23357) * mm, "end": v(5050.06, 23340.2) * mm});
            skLineSegment(sketch, "E842", {"start": v(5050.06, 23340.2) * mm, "end": v(5030.36, 23362.83) * mm});
            skLineSegment(sketch, "E843", {"start": v(5030.36, 23362.83) * mm, "end": v(5098.23, 23421.94) * mm});
            skLineSegment(sketch, "E844", {"start": v(5229.58, 23271.12) * mm, "end": v(5360.93, 23120.3) * mm});
            skLineSegment(sketch, "E845", {"start": v(5360.93, 23120.3) * mm, "end": v(5338.31, 23100.6) * mm});
            skLineSegment(sketch, "E846", {"start": v(5338.31, 23100.6) * mm, "end": v(5246.36, 23206.17) * mm});
            skLineSegment(sketch, "E847", {"start": v(5246.36, 23206.17) * mm, "end": v(5181.41, 23189.39) * mm});
            skLineSegment(sketch, "E848", {"start": v(5181.41, 23189.39) * mm, "end": v(5161.71, 23212.01) * mm});
            skLineSegment(sketch, "E849", {"start": v(5161.71, 23212.01) * mm, "end": v(5229.58, 23271.12) * mm});
            skLineSegment(sketch, "E850", {"start": v(5360.93, 23120.3) * mm, "end": v(5492.29, 22969.48) * mm});
            skLineSegment(sketch, "E851", {"start": v(5492.29, 22969.48) * mm, "end": v(5469.66, 22949.78) * mm});
            skLineSegment(sketch, "E852", {"start": v(5469.66, 22949.78) * mm, "end": v(5377.72, 23055.35) * mm});
            skLineSegment(sketch, "E853", {"start": v(5377.72, 23055.35) * mm, "end": v(5312.77, 23038.57) * mm});
            skLineSegment(sketch, "E854", {"start": v(5312.77, 23038.57) * mm, "end": v(5293.07, 23061.2) * mm});
            skLineSegment(sketch, "E855", {"start": v(5293.07, 23061.2) * mm, "end": v(5360.93, 23120.3) * mm});
            skLineSegment(sketch, "E856", {"start": v(5492.29, 22969.48) * mm, "end": v(5623.64, 22818.66) * mm});
            skLineSegment(sketch, "E857", {"start": v(5623.64, 22818.66) * mm, "end": v(5601.02, 22798.96) * mm});
            skLineSegment(sketch, "E858", {"start": v(5601.02, 22798.96) * mm, "end": v(5509.07, 22904.53) * mm});
            skLineSegment(sketch, "E859", {"start": v(5509.07, 22904.53) * mm, "end": v(5444.12, 22887.75) * mm});
            skLineSegment(sketch, "E860", {"start": v(5444.12, 22887.75) * mm, "end": v(5424.42, 22910.37) * mm});
            skLineSegment(sketch, "E861", {"start": v(5424.42, 22910.37) * mm, "end": v(5492.29, 22969.48) * mm});
            skLineSegment(sketch, "E862", {"start": v(4703.9, 23874.71) * mm, "end": v(4743.3, 23829.47) * mm});
            skLineSegment(sketch, "E863", {"start": v(4743.3, 23829.47) * mm, "end": v(4720.67, 23809.76) * mm});
            skLineSegment(sketch, "E864", {"start": v(4720.67, 23809.76) * mm, "end": v(4655.73, 23792.98) * mm});
            skLineSegment(sketch, "E865", {"start": v(4655.73, 23792.98) * mm, "end": v(4636.02, 23815.6) * mm});
            skLineSegment(sketch, "E866", {"start": v(4636.02, 23815.6) * mm, "end": v(4703.9, 23874.71) * mm});
            skLineSegment(sketch, "E867", {"start": v(5097.95, 23422.26) * mm, "end": v(4743.3, 23829.47) * mm});
            skLineSegment(sketch, "E868", {"start": v(4720.67, 23809.76) * mm, "end": v(5075.33, 23402.55) * mm});
            skLineSegment(sketch, "E869", {"start": v(5075.33, 23402.55) * mm, "end": v(5097.95, 23422.26) * mm});
            skLineSegment(sketch, "E870", {"start": v(5663.05, 22773.42) * mm, "end": v(5623.64, 22818.66) * mm});
            skLineSegment(sketch, "E871", {"start": v(5601.02, 22798.96) * mm, "end": v(5575.48, 22736.93) * mm});
            skLineSegment(sketch, "E872", {"start": v(5575.48, 22736.93) * mm, "end": v(5595.18, 22714.31) * mm});
            skLineSegment(sketch, "E873", {"start": v(5595.18, 22714.31) * mm, "end": v(5663.05, 22773.42) * mm});
            skLineSegment(sketch, "E874", {"start": v(6057.1, 22320.96) * mm, "end": v(6017.7, 22366.2) * mm});
            skLineSegment(sketch, "E875", {"start": v(6017.7, 22366.2) * mm, "end": v(5995.08, 22346.5) * mm});
            skLineSegment(sketch, "E876", {"start": v(5995.08, 22346.5) * mm, "end": v(5969.54, 22284.48) * mm});
            skLineSegment(sketch, "E877", {"start": v(5969.54, 22284.48) * mm, "end": v(5989.24, 22261.85) * mm});
            skLineSegment(sketch, "E878", {"start": v(5989.24, 22261.85) * mm, "end": v(6057.1, 22320.96) * mm});
            skLineSegment(sketch, "E879", {"start": v(5640.42, 22753.72) * mm, "end": v(5995.08, 22346.5) * mm});
            skLineSegment(sketch, "E880", {"start": v(5995.08, 22346.5) * mm, "end": v(6017.7, 22366.2) * mm});
            skLineSegment(sketch, "E881", {"start": v(6017.7, 22366.2) * mm, "end": v(5663.05, 22773.42) * mm});
            skLineSegment(sketch, "E882", {"start": v(5663.05, 22773.42) * mm, "end": v(5640.42, 22753.72) * mm});
            skLineSegment(sketch, "E883", {"start": v(734.23, 37775.9) * mm, "end": v(-5053.62, 37031.65) * mm});
            skLineSegment(sketch, "E884", {"start": v(-5053.62, 37031.65) * mm, "end": v(-4774.2, 36107.06) * mm});
            skLineSegment(sketch, "E885", {"start": v(7601.46, 21020.54) * mm, "end": v(7988.18, 20576.3) * mm});
            skLineSegment(sketch, "E886", {"start": v(7610.89, 21028.75) * mm, "end": v(7992.3, 20590.6) * mm});
            skLineSegment(sketch, "E887", {"start": v(7588.64, 21009.38) * mm, "end": v(7982.58, 20556.84) * mm});
            skLineSegment(sketch, "E888", {"start": v(7513.21, 20943.72) * mm, "end": v(7949.63, 20442.39) * mm});
            skLineSegment(sketch, "E889", {"start": v(7501.9, 20933.87) * mm, "end": v(7944.69, 20425.22) * mm});
            skLineSegment(sketch, "E890", {"start": v(7426.47, 20868.21) * mm, "end": v(7911.74, 20310.77) * mm});
            skLineSegment(sketch, "E891", {"start": v(7366.89, 20816.34) * mm, "end": v(7885.71, 20220.35) * mm});
            skLineSegment(sketch, "E892", {"start": v(7620.32, 21036.96) * mm, "end": v(7996.42, 20604.91) * mm});
            skLineSegment(sketch, "E893", {"start": v(4984.65, 24045.64) * mm, "end": v(6264.89, 22574.96) * mm});
            skLineSegment(sketch, "E894", {"start": v(4994.07, 24053.84) * mm, "end": v(6274.31, 22583.17) * mm});
            skLineSegment(sketch, "E895", {"start": v(4975.22, 24037.43) * mm, "end": v(6255.46, 22566.76) * mm});
            skLineSegment(sketch, "E896", {"start": v(4962.4, 24026.27) * mm, "end": v(6242.64, 22555.6) * mm});
            skLineSegment(sketch, "E897", {"start": v(4886.97, 23960.6) * mm, "end": v(6167.21, 22489.94) * mm});
            skLineSegment(sketch, "E898", {"start": v(4875.66, 23950.76) * mm, "end": v(6155.9, 22480.09) * mm});
            skLineSegment(sketch, "E899", {"start": v(4800.23, 23885.1) * mm, "end": v(6080.47, 22414.43) * mm});
            skLineSegment(sketch, "E900", {"start": v(4740.65, 23833.23) * mm, "end": v(6020.89, 22362.56) * mm});
            skLineSegment(sketch, "E901", {"start": v(6020.89, 22362.56) * mm, "end": v(6274.31, 22583.17) * mm});
            skLineSegment(sketch, "E902", {"start": v(7366.89, 20816.34) * mm, "end": v(7620.32, 21036.96) * mm});
            skLineSegment(sketch, "E903", {"start": v(2359.12, 27061.7) * mm, "end": v(3638.65, 25591.85) * mm});
            skLineSegment(sketch, "E904", {"start": v(2368.55, 27069.9) * mm, "end": v(3648.07, 25600.06) * mm});
            skLineSegment(sketch, "E905", {"start": v(2349.7, 27053.5) * mm, "end": v(3629.22, 25583.65) * mm});
            skLineSegment(sketch, "E906", {"start": v(2336.87, 27042.33) * mm, "end": v(3616.4, 25572.48) * mm});
            skLineSegment(sketch, "E907", {"start": v(2261.45, 26976.67) * mm, "end": v(3540.97, 25506.83) * mm});
            skLineSegment(sketch, "E908", {"start": v(2250.14, 26966.82) * mm, "end": v(3529.66, 25496.98) * mm});
            skLineSegment(sketch, "E909", {"start": v(2174.71, 26901.16) * mm, "end": v(3454.23, 25431.32) * mm});
            skLineSegment(sketch, "E910", {"start": v(2115.12, 26849.3) * mm, "end": v(3394.65, 25379.45) * mm});
            skLineSegment(sketch, "E911", {"start": v(3394.65, 25379.45) * mm, "end": v(3648.07, 25600.06) * mm});
            skLineSegment(sketch, "E912", {"start": v(4740.65, 23833.23) * mm, "end": v(4994.07, 24053.84) * mm});
            skLineSegment(sketch, "E913", {"start": v(-448.47, 30286.92) * mm, "end": v(1013.12, 28607.92) * mm});
            skLineSegment(sketch, "E914", {"start": v(-444.35, 30301.23) * mm, "end": v(1022.55, 28616.12) * mm});
            skLineSegment(sketch, "E915", {"start": v(-452.6, 30272.61) * mm, "end": v(1003.7, 28599.7) * mm});
            skLineSegment(sketch, "E916", {"start": v(-458.2, 30253.16) * mm, "end": v(990.87, 28588.55) * mm});
            skLineSegment(sketch, "E917", {"start": v(-491.14, 30138.7) * mm, "end": v(915.45, 28522.89) * mm});
            skLineSegment(sketch, "E918", {"start": v(-496.08, 30121.54) * mm, "end": v(904.13, 28513.04) * mm});
            skLineSegment(sketch, "E919", {"start": v(-529.03, 30007.08) * mm, "end": v(828.7, 28447.38) * mm});
            skLineSegment(sketch, "E920", {"start": v(-555.06, 29916.66) * mm, "end": v(769.12, 28395.5) * mm});
            skLineSegment(sketch, "E921", {"start": v(769.12, 28395.5) * mm, "end": v(1022.55, 28616.12) * mm});
            skLineSegment(sketch, "E922", {"start": v(2115.12, 26849.3) * mm, "end": v(2368.55, 27069.9) * mm});
            skLineSegment(sketch, "E923", {"start": v(7083.78, 21255.34) * mm, "end": v(7335.9, 20965.7) * mm});
            skLineSegment(sketch, "E924", {"start": v(7335.9, 20965.7) * mm, "end": v(7313.28, 20946) * mm});
            skLineSegment(sketch, "E925", {"start": v(7313.28, 20946) * mm, "end": v(7061.15, 21235.64) * mm});
            skLineSegment(sketch, "E926", {"start": v(7061.15, 21235.64) * mm, "end": v(7083.78, 21255.34) * mm});
            skLineSegment(sketch, "E927", {"start": v(6100.48, 22365.56) * mm, "end": v(6986.87, 21347.32) * mm});
            skLineSegment(sketch, "E928", {"start": v(6986.87, 21347.32) * mm, "end": v(6964.24, 21327.62) * mm});
            skLineSegment(sketch, "E929", {"start": v(6964.24, 21327.62) * mm, "end": v(6077.85, 22345.86) * mm});
            skLineSegment(sketch, "E930", {"start": v(6077.85, 22345.86) * mm, "end": v(6100.48, 22365.56) * mm});
            skLineSegment(sketch, "E931", {"start": v(7402.9, 20957.74) * mm, "end": v(7236.23, 21424.78) * mm});
            skLineSegment(sketch, "E932", {"start": v(7116.22, 21459.92) * mm, "end": v(7149.05, 21422.2) * mm});
            skLineSegment(sketch, "E933", {"start": v(7149.05, 21422.2) * mm, "end": v(6997.07, 21289.9) * mm});
            skLineSegment(sketch, "E934", {"start": v(6997.07, 21289.9) * mm, "end": v(6964.24, 21327.62) * mm});
            skLineSegment(sketch, "E935", {"start": v(6964.24, 21327.62) * mm, "end": v(7116.22, 21459.92) * mm});
            skLineSegment(sketch, "E936", {"start": v(7083.8, 21324.3) * mm, "end": v(7079.27, 21320.36) * mm});
            skLineSegment(sketch, "E937", {"start": v(7079.27, 21320.36) * mm, "end": v(7058.92, 21343.75) * mm});
            skLineSegment(sketch, "E938", {"start": v(7058.92, 21343.75) * mm, "end": v(6997.07, 21289.9) * mm});
            skLineSegment(sketch, "E939", {"start": v(6997.07, 21289.9) * mm, "end": v(7051.57, 21227.3) * mm});
            skLineSegment(sketch, "E940", {"start": v(7051.57, 21227.3) * mm, "end": v(7117.94, 21285.08) * mm});
            skLineSegment(sketch, "E941", {"start": v(7117.94, 21285.08) * mm, "end": v(7083.8, 21324.3) * mm});
            skLineSegment(sketch, "E942", {"start": v(6964.24, 21327.62) * mm, "end": v(6997.07, 21289.9) * mm});
            skLineSegment(sketch, "E943", {"start": v(6997.07, 21289.9) * mm, "end": v(6972.94, 21268.9) * mm});
            skLineSegment(sketch, "E944", {"start": v(6972.94, 21268.9) * mm, "end": v(6940.1, 21306.6) * mm});
            skLineSegment(sketch, "E945", {"start": v(6940.1, 21306.6) * mm, "end": v(6964.24, 21327.62) * mm});
            skLineSegment(sketch, "E946", {"start": v(7420.04, 20928.9) * mm, "end": v(7398.38, 20953.8) * mm});
            skLineSegment(sketch, "E947", {"start": v(7398.38, 20953.8) * mm, "end": v(7402.9, 20957.74) * mm});
            skLineSegment(sketch, "E948", {"start": v(7402.9, 20957.74) * mm, "end": v(7370.07, 20995.45) * mm});
            skLineSegment(sketch, "E949", {"start": v(7370.07, 20995.45) * mm, "end": v(7303.7, 20937.67) * mm});
            skLineSegment(sketch, "E950", {"start": v(7303.7, 20937.67) * mm, "end": v(7358.2, 20875.07) * mm});
            skLineSegment(sketch, "E951", {"start": v(7358.2, 20875.07) * mm, "end": v(7420.04, 20928.9) * mm});
            skLineSegment(sketch, "E952", {"start": v(7510.18, 21007.37) * mm, "end": v(7543, 20969.66) * mm});
            skLineSegment(sketch, "E953", {"start": v(7543, 20969.66) * mm, "end": v(7391.02, 20837.35) * mm});
            skLineSegment(sketch, "E954", {"start": v(7391.02, 20837.35) * mm, "end": v(7358.2, 20875.07) * mm});
            skLineSegment(sketch, "E955", {"start": v(7358.2, 20875.07) * mm, "end": v(7510.18, 21007.37) * mm});
            skLineSegment(sketch, "E956", {"start": v(7358.2, 20875.07) * mm, "end": v(7391.02, 20837.35) * mm});
            skLineSegment(sketch, "E957", {"start": v(7391.02, 20837.35) * mm, "end": v(7366.89, 20816.34) * mm});
            skLineSegment(sketch, "E958", {"start": v(7366.89, 20816.34) * mm, "end": v(7334.06, 20854.06) * mm});
            skLineSegment(sketch, "E959", {"start": v(7334.06, 20854.06) * mm, "end": v(7358.2, 20875.07) * mm});
            skLineSegment(sketch, "E960", {"start": v(6197, 22515.87) * mm, "end": v(6229.83, 22478.16) * mm});
            skLineSegment(sketch, "E961", {"start": v(6229.83, 22478.16) * mm, "end": v(6077.85, 22345.86) * mm});
            skLineSegment(sketch, "E962", {"start": v(6077.85, 22345.86) * mm, "end": v(6045.02, 22383.57) * mm});
            skLineSegment(sketch, "E963", {"start": v(6045.02, 22383.57) * mm, "end": v(6197, 22515.87) * mm});
            skLineSegment(sketch, "E964", {"start": v(6045.02, 22383.57) * mm, "end": v(6077.85, 22345.86) * mm});
            skLineSegment(sketch, "E965", {"start": v(6077.85, 22345.86) * mm, "end": v(6053.72, 22324.85) * mm});
            skLineSegment(sketch, "E966", {"start": v(6053.72, 22324.85) * mm, "end": v(6020.89, 22362.56) * mm});
            skLineSegment(sketch, "E967", {"start": v(6020.89, 22362.56) * mm, "end": v(6045.02, 22383.57) * mm});
            skArc(sketch, "E968", {"start": v(7236.23, 21424.78) * mm, "mid": v(7156.66, 21379.64) * mm, "end": v(7083.8, 21324.3) * mm});
            skLineSegment(sketch, "E969", {"start": v(6273.1, 22565.54) * mm, "end": v(6205.21, 22506.44) * mm});
            skLineSegment(sketch, "E970", {"start": v(6290.73, 22564.32) * mm, "end": v(6213.42, 22497.02) * mm});
            skLineSegment(sketch, "E971", {"start": v(6274.31, 22583.17) * mm, "end": v(6197, 22515.87) * mm});
            skLineSegment(sketch, "E972", {"start": v(6273.1, 22565.54) * mm, "end": v(6264.89, 22574.96) * mm});
            skLineSegment(sketch, "E973", {"start": v(6274.31, 22583.17) * mm, "end": v(6290.73, 22564.32) * mm});
            skLineSegment(sketch, "E974", {"start": v(7534.8, 20979.09) * mm, "end": v(7602.68, 21038.18) * mm});
            skLineSegment(sketch, "E975", {"start": v(7526.6, 20988.51) * mm, "end": v(7603.9, 21055.81) * mm});
            skLineSegment(sketch, "E976", {"start": v(7543, 20969.66) * mm, "end": v(7620.32, 21036.96) * mm});
            skLineSegment(sketch, "E977", {"start": v(7602.68, 21038.18) * mm, "end": v(7610.89, 21028.75) * mm});
            skLineSegment(sketch, "E978", {"start": v(7620.32, 21036.96) * mm, "end": v(7603.9, 21055.81) * mm});
            skLineSegment(sketch, "E979", {"start": v(6229.83, 22478.16) * mm, "end": v(7510.18, 21007.37) * mm});
            skLineSegment(sketch, "E980", {"start": v(7334.17, 20854.15) * mm, "end": v(6053.82, 22324.94) * mm});
            skLineSegment(sketch, "E981", {"start": v(4457.53, 24272.23) * mm, "end": v(4709.66, 23982.6) * mm});
            skLineSegment(sketch, "E982", {"start": v(4709.66, 23982.6) * mm, "end": v(4687.04, 23962.9) * mm});
            skLineSegment(sketch, "E983", {"start": v(4687.04, 23962.9) * mm, "end": v(4434.9, 24252.53) * mm});
            skLineSegment(sketch, "E984", {"start": v(4434.9, 24252.53) * mm, "end": v(4457.53, 24272.23) * mm});
            skLineSegment(sketch, "E985", {"start": v(3474.24, 25382.44) * mm, "end": v(4360.63, 24364.2) * mm});
            skLineSegment(sketch, "E986", {"start": v(4360.63, 24364.2) * mm, "end": v(4338, 24344.5) * mm});
            skLineSegment(sketch, "E987", {"start": v(4338, 24344.5) * mm, "end": v(3451.61, 25362.75) * mm});
            skLineSegment(sketch, "E988", {"start": v(3451.61, 25362.75) * mm, "end": v(3474.24, 25382.44) * mm});
            skLineSegment(sketch, "E989", {"start": v(4776.66, 23974.63) * mm, "end": v(4609.98, 24441.67) * mm});
            skLineSegment(sketch, "E990", {"start": v(4489.98, 24476.8) * mm, "end": v(4522.81, 24439.1) * mm});
            skLineSegment(sketch, "E991", {"start": v(4522.81, 24439.1) * mm, "end": v(4370.83, 24306.8) * mm});
            skLineSegment(sketch, "E992", {"start": v(4370.83, 24306.8) * mm, "end": v(4338, 24344.5) * mm});
            skLineSegment(sketch, "E993", {"start": v(4338, 24344.5) * mm, "end": v(4489.98, 24476.8) * mm});
            skLineSegment(sketch, "E994", {"start": v(4457.56, 24341.2) * mm, "end": v(4453.03, 24337.25) * mm});
            skLineSegment(sketch, "E995", {"start": v(4453.03, 24337.25) * mm, "end": v(4432.68, 24360.63) * mm});
            skLineSegment(sketch, "E996", {"start": v(4432.68, 24360.63) * mm, "end": v(4370.83, 24306.8) * mm});
            skLineSegment(sketch, "E997", {"start": v(4370.83, 24306.8) * mm, "end": v(4425.33, 24244.2) * mm});
            skLineSegment(sketch, "E998", {"start": v(4425.33, 24244.2) * mm, "end": v(4491.7, 24301.97) * mm});
            skLineSegment(sketch, "E999", {"start": v(4491.7, 24301.97) * mm, "end": v(4457.56, 24341.2) * mm});
            skLineSegment(sketch, "E1000", {"start": v(4338, 24344.5) * mm, "end": v(4370.83, 24306.8) * mm});
            skLineSegment(sketch, "E1001", {"start": v(4370.83, 24306.8) * mm, "end": v(4346.7, 24285.78) * mm});
            skLineSegment(sketch, "E1002", {"start": v(4346.7, 24285.78) * mm, "end": v(4313.87, 24323.5) * mm});
            skLineSegment(sketch, "E1003", {"start": v(4313.87, 24323.5) * mm, "end": v(4338, 24344.5) * mm});
            skLineSegment(sketch, "E1004", {"start": v(4793.8, 23945.8) * mm, "end": v(4772.13, 23970.69) * mm});
            skLineSegment(sketch, "E1005", {"start": v(4772.13, 23970.69) * mm, "end": v(4776.66, 23974.63) * mm});
            skLineSegment(sketch, "E1006", {"start": v(4776.66, 23974.63) * mm, "end": v(4743.83, 24012.34) * mm});
            skLineSegment(sketch, "E1007", {"start": v(4743.83, 24012.34) * mm, "end": v(4677.46, 23954.56) * mm});
            skLineSegment(sketch, "E1008", {"start": v(4677.46, 23954.56) * mm, "end": v(4731.95, 23891.96) * mm});
            skLineSegment(sketch, "E1009", {"start": v(4731.95, 23891.96) * mm, "end": v(4793.8, 23945.8) * mm});
            skLineSegment(sketch, "E1010", {"start": v(4883.94, 24024.26) * mm, "end": v(4916.76, 23986.55) * mm});
            skLineSegment(sketch, "E1011", {"start": v(4916.76, 23986.55) * mm, "end": v(4764.78, 23854.24) * mm});
            skLineSegment(sketch, "E1012", {"start": v(4764.78, 23854.24) * mm, "end": v(4731.95, 23891.96) * mm});
            skLineSegment(sketch, "E1013", {"start": v(4731.95, 23891.96) * mm, "end": v(4883.94, 24024.26) * mm});
            skLineSegment(sketch, "E1014", {"start": v(4731.95, 23891.96) * mm, "end": v(4764.78, 23854.24) * mm});
            skLineSegment(sketch, "E1015", {"start": v(4764.78, 23854.24) * mm, "end": v(4740.65, 23833.23) * mm});
            skLineSegment(sketch, "E1016", {"start": v(4740.65, 23833.23) * mm, "end": v(4707.82, 23870.94) * mm});
            skLineSegment(sketch, "E1017", {"start": v(4707.82, 23870.94) * mm, "end": v(4731.95, 23891.96) * mm});
            skLineSegment(sketch, "E1018", {"start": v(3570.76, 25532.76) * mm, "end": v(3603.6, 25495.05) * mm});
            skLineSegment(sketch, "E1019", {"start": v(3603.6, 25495.05) * mm, "end": v(3451.61, 25362.75) * mm});
            skLineSegment(sketch, "E1020", {"start": v(3451.61, 25362.75) * mm, "end": v(3418.78, 25400.46) * mm});
            skLineSegment(sketch, "E1021", {"start": v(3418.78, 25400.46) * mm, "end": v(3570.76, 25532.76) * mm});
            skLineSegment(sketch, "E1022", {"start": v(3418.78, 25400.46) * mm, "end": v(3451.61, 25362.75) * mm});
            skLineSegment(sketch, "E1023", {"start": v(3451.61, 25362.75) * mm, "end": v(3427.47, 25341.73) * mm});
            skLineSegment(sketch, "E1024", {"start": v(3427.47, 25341.73) * mm, "end": v(3394.65, 25379.45) * mm});
            skLineSegment(sketch, "E1025", {"start": v(3394.65, 25379.45) * mm, "end": v(3418.78, 25400.46) * mm});
            skArc(sketch, "E1026", {"start": v(4609.98, 24441.67) * mm, "mid": v(4530.41, 24396.52) * mm, "end": v(4457.56, 24341.2) * mm});
            skLineSegment(sketch, "E1027", {"start": v(3646.85, 25582.42) * mm, "end": v(3578.97, 25523.33) * mm});
            skLineSegment(sketch, "E1028", {"start": v(3664.49, 25581.2) * mm, "end": v(3587.18, 25513.9) * mm});
            skLineSegment(sketch, "E1029", {"start": v(3648.07, 25600.06) * mm, "end": v(3570.76, 25532.76) * mm});
            skLineSegment(sketch, "E1030", {"start": v(3646.85, 25582.42) * mm, "end": v(3638.65, 25591.85) * mm});
            skLineSegment(sketch, "E1031", {"start": v(3648.07, 25600.06) * mm, "end": v(3664.49, 25581.2) * mm});
            skLineSegment(sketch, "E1032", {"start": v(4908.56, 23995.97) * mm, "end": v(4976.44, 24055.07) * mm});
            skLineSegment(sketch, "E1033", {"start": v(4900.35, 24005.4) * mm, "end": v(4977.66, 24072.7) * mm});
            skLineSegment(sketch, "E1034", {"start": v(4916.76, 23986.55) * mm, "end": v(4994.08, 24053.85) * mm});
            skLineSegment(sketch, "E1035", {"start": v(4976.44, 24055.07) * mm, "end": v(4984.65, 24045.64) * mm});
            skLineSegment(sketch, "E1036", {"start": v(4994.08, 24053.85) * mm, "end": v(4977.66, 24072.7) * mm});
            skLineSegment(sketch, "E1037", {"start": v(3603.6, 25495.05) * mm, "end": v(4883.94, 24024.26) * mm});
            skLineSegment(sketch, "E1038", {"start": v(4707.93, 23871.04) * mm, "end": v(3427.58, 25341.83) * mm});
            skLineSegment(sketch, "E1039", {"start": v(1832.01, 27288.29) * mm, "end": v(2084.14, 26998.66) * mm});
            skLineSegment(sketch, "E1040", {"start": v(2084.14, 26998.66) * mm, "end": v(2061.51, 26978.96) * mm});
            skLineSegment(sketch, "E1041", {"start": v(2061.51, 26978.96) * mm, "end": v(1809.38, 27268.6) * mm});
            skLineSegment(sketch, "E1042", {"start": v(1809.38, 27268.6) * mm, "end": v(1832.01, 27288.29) * mm});
            skLineSegment(sketch, "E1043", {"start": v(848.72, 28398.5) * mm, "end": v(1735.1, 27380.27) * mm});
            skLineSegment(sketch, "E1044", {"start": v(1735.1, 27380.27) * mm, "end": v(1712.48, 27360.57) * mm});
            skLineSegment(sketch, "E1045", {"start": v(1712.48, 27360.57) * mm, "end": v(826.09, 28378.8) * mm});
            skLineSegment(sketch, "E1046", {"start": v(826.09, 28378.8) * mm, "end": v(848.72, 28398.5) * mm});
            skLineSegment(sketch, "E1047", {"start": v(2151.14, 26990.69) * mm, "end": v(1984.46, 27457.73) * mm});
            skLineSegment(sketch, "E1048", {"start": v(1864.46, 27492.87) * mm, "end": v(1897.3, 27455.16) * mm});
            skLineSegment(sketch, "E1049", {"start": v(1897.3, 27455.16) * mm, "end": v(1745.3, 27322.86) * mm});
            skLineSegment(sketch, "E1050", {"start": v(1745.3, 27322.86) * mm, "end": v(1712.48, 27360.57) * mm});
            skLineSegment(sketch, "E1051", {"start": v(1712.48, 27360.57) * mm, "end": v(1864.46, 27492.87) * mm});
            skLineSegment(sketch, "E1052", {"start": v(1832.04, 27357.25) * mm, "end": v(1827.51, 27353.31) * mm});
            skLineSegment(sketch, "E1053", {"start": v(1827.51, 27353.31) * mm, "end": v(1807.16, 27376.7) * mm});
            skLineSegment(sketch, "E1054", {"start": v(1807.16, 27376.7) * mm, "end": v(1745.3, 27322.86) * mm});
            skLineSegment(sketch, "E1055", {"start": v(1745.3, 27322.86) * mm, "end": v(1799.8, 27260.25) * mm});
            skLineSegment(sketch, "E1056", {"start": v(1799.8, 27260.25) * mm, "end": v(1866.18, 27318.03) * mm});
            skLineSegment(sketch, "E1057", {"start": v(1866.18, 27318.03) * mm, "end": v(1832.04, 27357.25) * mm});
            skLineSegment(sketch, "E1058", {"start": v(1712.48, 27360.57) * mm, "end": v(1745.3, 27322.86) * mm});
            skLineSegment(sketch, "E1059", {"start": v(1745.3, 27322.86) * mm, "end": v(1721.17, 27301.85) * mm});
            skLineSegment(sketch, "E1060", {"start": v(1721.17, 27301.85) * mm, "end": v(1688.34, 27339.56) * mm});
            skLineSegment(sketch, "E1061", {"start": v(1688.34, 27339.56) * mm, "end": v(1712.48, 27360.57) * mm});
            skLineSegment(sketch, "E1062", {"start": v(2168.28, 26961.86) * mm, "end": v(2146.61, 26986.75) * mm});
            skLineSegment(sketch, "E1063", {"start": v(2146.61, 26986.75) * mm, "end": v(2151.14, 26990.69) * mm});
            skLineSegment(sketch, "E1064", {"start": v(2151.14, 26990.69) * mm, "end": v(2118.3, 27028.4) * mm});
            skLineSegment(sketch, "E1065", {"start": v(2118.3, 27028.4) * mm, "end": v(2051.93, 26970.62) * mm});
            skLineSegment(sketch, "E1066", {"start": v(2051.93, 26970.62) * mm, "end": v(2106.43, 26908.02) * mm});
            skLineSegment(sketch, "E1067", {"start": v(2106.43, 26908.02) * mm, "end": v(2168.28, 26961.86) * mm});
            skLineSegment(sketch, "E1068", {"start": v(2258.41, 27040.32) * mm, "end": v(2291.24, 27002.6) * mm});
            skLineSegment(sketch, "E1069", {"start": v(2291.24, 27002.6) * mm, "end": v(2139.26, 26870.3) * mm});
            skLineSegment(sketch, "E1070", {"start": v(2139.26, 26870.3) * mm, "end": v(2106.43, 26908.02) * mm});
            skLineSegment(sketch, "E1071", {"start": v(2106.43, 26908.02) * mm, "end": v(2258.41, 27040.32) * mm});
            skLineSegment(sketch, "E1072", {"start": v(2106.43, 26908.02) * mm, "end": v(2139.26, 26870.3) * mm});
            skLineSegment(sketch, "E1073", {"start": v(2139.26, 26870.3) * mm, "end": v(2115.12, 26849.3) * mm});
            skLineSegment(sketch, "E1074", {"start": v(2115.12, 26849.3) * mm, "end": v(2082.3, 26887) * mm});
            skLineSegment(sketch, "E1075", {"start": v(2082.3, 26887) * mm, "end": v(2106.43, 26908.02) * mm});
            skLineSegment(sketch, "E1076", {"start": v(945.24, 28548.82) * mm, "end": v(978.07, 28511.1) * mm});
            skLineSegment(sketch, "E1077", {"start": v(978.07, 28511.1) * mm, "end": v(826.09, 28378.8) * mm});
            skLineSegment(sketch, "E1078", {"start": v(826.09, 28378.8) * mm, "end": v(793.26, 28416.52) * mm});
            skLineSegment(sketch, "E1079", {"start": v(793.26, 28416.52) * mm, "end": v(945.24, 28548.82) * mm});
            skLineSegment(sketch, "E1080", {"start": v(793.26, 28416.52) * mm, "end": v(826.09, 28378.8) * mm});
            skLineSegment(sketch, "E1081", {"start": v(826.09, 28378.8) * mm, "end": v(801.95, 28357.8) * mm});
            skLineSegment(sketch, "E1082", {"start": v(801.95, 28357.8) * mm, "end": v(769.12, 28395.5) * mm});
            skLineSegment(sketch, "E1083", {"start": v(769.12, 28395.5) * mm, "end": v(793.26, 28416.52) * mm});
            skArc(sketch, "E1084", {"start": v(1984.46, 27457.73) * mm, "mid": v(1904.9, 27412.59) * mm, "end": v(1832.04, 27357.25) * mm});
            skLineSegment(sketch, "E1085", {"start": v(1021.33, 28598.49) * mm, "end": v(953.45, 28539.4) * mm});
            skLineSegment(sketch, "E1086", {"start": v(1038.97, 28597.27) * mm, "end": v(961.66, 28529.97) * mm});
            skLineSegment(sketch, "E1087", {"start": v(1022.55, 28616.12) * mm, "end": v(945.24, 28548.82) * mm});
            skLineSegment(sketch, "E1088", {"start": v(1021.33, 28598.49) * mm, "end": v(1013.12, 28607.92) * mm});
            skLineSegment(sketch, "E1089", {"start": v(1022.55, 28616.12) * mm, "end": v(1038.97, 28597.27) * mm});
            skLineSegment(sketch, "E1090", {"start": v(2283.04, 27012.04) * mm, "end": v(2350.92, 27071.13) * mm});
            skLineSegment(sketch, "E1091", {"start": v(2274.83, 27021.46) * mm, "end": v(2352.14, 27088.76) * mm});
            skLineSegment(sketch, "E1092", {"start": v(2291.24, 27002.6) * mm, "end": v(2368.55, 27069.9) * mm});
            skLineSegment(sketch, "E1093", {"start": v(2350.92, 27071.13) * mm, "end": v(2359.13, 27061.7) * mm});
            skLineSegment(sketch, "E1094", {"start": v(2368.55, 27069.9) * mm, "end": v(2352.14, 27088.76) * mm});
            skLineSegment(sketch, "E1095", {"start": v(978.07, 28511.1) * mm, "end": v(2258.41, 27040.32) * mm});
            skLineSegment(sketch, "E1096", {"start": v(2082.4, 26887.1) * mm, "end": v(802.06, 28357.9) * mm});
            skLineSegment(sketch, "E1097", {"start": v(815.83, 37387.25) * mm, "end": v(811.55, 37386.7) * mm});
            skLineSegment(sketch, "E1098", {"start": v(814.24, 37399.64) * mm, "end": v(808.92, 37398.96) * mm});
            skLineSegment(sketch, "E1099", {"start": v(812.08, 37416.5) * mm, "end": v(805.35, 37415.64) * mm});
            skLineSegment(sketch, "E1100", {"start": v(799.36, 37515.7) * mm, "end": v(784.36, 37513.77) * mm});
            skLineSegment(sketch, "E1101", {"start": v(797.45, 37530.57) * mm, "end": v(781.21, 37528.49) * mm});
            skLineSegment(sketch, "E1102", {"start": v(784.72, 37629.76) * mm, "end": v(760.22, 37626.62) * mm});
            skLineSegment(sketch, "E1103", {"start": v(774.67, 37708.12) * mm, "end": v(743.64, 37704.14) * mm});
            skLineSegment(sketch, "E1104", {"start": v(4783.32, 37896.2) * mm, "end": v(2849.17, 37648.08) * mm});
            skLineSegment(sketch, "E1105", {"start": v(4784.91, 37883.8) * mm, "end": v(2850.76, 37635.68) * mm});
            skLineSegment(sketch, "E1106", {"start": v(4781.73, 37908.6) * mm, "end": v(2847.58, 37660.48) * mm});
            skLineSegment(sketch, "E1107", {"start": v(4779.57, 37925.46) * mm, "end": v(2845.42, 37677.34) * mm});
            skLineSegment(sketch, "E1108", {"start": v(4766.85, 38024.64) * mm, "end": v(2832.7, 37776.53) * mm});
            skLineSegment(sketch, "E1109", {"start": v(4764.94, 38039.52) * mm, "end": v(2830.79, 37791.4) * mm});
            skLineSegment(sketch, "E1110", {"start": v(4752.21, 38138.7) * mm, "end": v(2818.06, 37890.6) * mm});
            skLineSegment(sketch, "E1111", {"start": v(4742.16, 38217.07) * mm, "end": v(2808.01, 37968.95) * mm});
            skLineSegment(sketch, "E1112", {"start": v(2808.01, 37968.95) * mm, "end": v(2850.76, 37635.68) * mm});
            skLineSegment(sketch, "E1113", {"start": v(774.67, 37708.12) * mm, "end": v(817.42, 37374.85) * mm});
            skLineSegment(sketch, "E1114", {"start": v(4742.16, 38217.07) * mm, "end": v(4784.91, 37883.8) * mm});
            skLineSegment(sketch, "E1115", {"start": v(2767.58, 37891.18) * mm, "end": v(2222.05, 37821.2) * mm});
            skLineSegment(sketch, "E1116", {"start": v(2222.05, 37821.2) * mm, "end": v(2216.96, 37860.87) * mm});
            skLineSegment(sketch, "E1117", {"start": v(2216.96, 37860.87) * mm, "end": v(2762.49, 37930.85) * mm});
            skLineSegment(sketch, "E1118", {"start": v(2762.49, 37930.85) * mm, "end": v(2767.58, 37891.18) * mm});
            skLineSegment(sketch, "E1119", {"start": v(1467.39, 37676) * mm, "end": v(2132.75, 37509) * mm});
            skLineSegment(sketch, "E1120", {"start": v(2091.75, 37791.68) * mm, "end": v(1512.5, 37717.37) * mm});
            skLineSegment(sketch, "E1121", {"start": v(1512.5, 37717.37) * mm, "end": v(1507.4, 37757.05) * mm});
            skLineSegment(sketch, "E1122", {"start": v(1507.4, 37757.05) * mm, "end": v(2086.66, 37831.35) * mm});
            skLineSegment(sketch, "E1123", {"start": v(2086.66, 37831.35) * mm, "end": v(2091.75, 37791.68) * mm});
            skLineSegment(sketch, "E1124", {"start": v(1378.96, 37713.04) * mm, "end": v(833.43, 37643.06) * mm});
            skLineSegment(sketch, "E1125", {"start": v(833.43, 37643.06) * mm, "end": v(828.34, 37682.74) * mm});
            skLineSegment(sketch, "E1126", {"start": v(828.34, 37682.74) * mm, "end": v(1373.87, 37752.72) * mm});
            skLineSegment(sketch, "E1127", {"start": v(1373.87, 37752.72) * mm, "end": v(1378.96, 37713.04) * mm});
            skLineSegment(sketch, "E1128", {"start": v(2242.6, 37661) * mm, "end": v(2193, 37654.65) * mm});
            skLineSegment(sketch, "E1129", {"start": v(2193, 37654.65) * mm, "end": v(2167.37, 37854.5) * mm});
            skLineSegment(sketch, "E1130", {"start": v(2167.37, 37854.5) * mm, "end": v(2216.96, 37860.87) * mm});
            skLineSegment(sketch, "E1131", {"start": v(2216.96, 37860.87) * mm, "end": v(2242.6, 37661) * mm});
            skLineSegment(sketch, "E1132", {"start": v(853.98, 37482.88) * mm, "end": v(804.38, 37476.51) * mm});
            skLineSegment(sketch, "E1133", {"start": v(804.38, 37476.51) * mm, "end": v(778.74, 37676.38) * mm});
            skLineSegment(sketch, "E1134", {"start": v(778.74, 37676.38) * mm, "end": v(828.34, 37682.74) * mm});
            skLineSegment(sketch, "E1135", {"start": v(828.34, 37682.74) * mm, "end": v(853.98, 37482.88) * mm});
            skLineSegment(sketch, "E1136", {"start": v(2788.13, 37730.99) * mm, "end": v(853.98, 37482.88) * mm});
            skLineSegment(sketch, "E1137", {"start": v(2808.01, 37968.95) * mm, "end": v(774.67, 37708.12) * mm});
            skLineSegment(sketch, "E1138", {"start": v(2147.81, 37763.28) * mm, "end": v(2147.05, 37769.23) * mm});
            skLineSegment(sketch, "E1139", {"start": v(2147.05, 37769.23) * mm, "end": v(2177.8, 37773.18) * mm});
            skLineSegment(sketch, "E1140", {"start": v(2177.8, 37773.18) * mm, "end": v(2167.37, 37854.5) * mm});
            skLineSegment(sketch, "E1141", {"start": v(2167.37, 37854.5) * mm, "end": v(2085.04, 37843.95) * mm});
            skLineSegment(sketch, "E1142", {"start": v(2085.04, 37843.95) * mm, "end": v(2096.24, 37756.66) * mm});
            skLineSegment(sketch, "E1143", {"start": v(2096.24, 37756.66) * mm, "end": v(2147.81, 37763.28) * mm});
            skLineSegment(sketch, "E1144", {"start": v(2216.96, 37860.87) * mm, "end": v(2167.37, 37854.5) * mm});
            skLineSegment(sketch, "E1145", {"start": v(2167.37, 37854.5) * mm, "end": v(2163.3, 37886.25) * mm});
            skLineSegment(sketch, "E1146", {"start": v(2163.3, 37886.25) * mm, "end": v(2212.89, 37892.61) * mm});
            skLineSegment(sketch, "E1147", {"start": v(2212.89, 37892.61) * mm, "end": v(2216.96, 37860.87) * mm});
            skLineSegment(sketch, "E1148", {"start": v(1433.9, 37677.75) * mm, "end": v(1466.63, 37681.95) * mm});
            skLineSegment(sketch, "E1149", {"start": v(1466.63, 37681.95) * mm, "end": v(1467.39, 37676) * mm});
            skLineSegment(sketch, "E1150", {"start": v(1467.39, 37676) * mm, "end": v(1516.98, 37682.36) * mm});
            skLineSegment(sketch, "E1151", {"start": v(1516.98, 37682.36) * mm, "end": v(1505.79, 37769.64) * mm});
            skLineSegment(sketch, "E1152", {"start": v(1505.79, 37769.64) * mm, "end": v(1423.46, 37759.08) * mm});
            skLineSegment(sketch, "E1153", {"start": v(1423.46, 37759.08) * mm, "end": v(1433.9, 37677.75) * mm});
            skLineSegment(sketch, "E1154", {"start": v(1449.1, 37559.22) * mm, "end": v(1399.5, 37552.86) * mm});
            skLineSegment(sketch, "E1155", {"start": v(1399.5, 37552.86) * mm, "end": v(1373.87, 37752.72) * mm});
            skLineSegment(sketch, "E1156", {"start": v(1373.87, 37752.72) * mm, "end": v(1423.46, 37759.08) * mm});
            skLineSegment(sketch, "E1157", {"start": v(1423.46, 37759.08) * mm, "end": v(1449.1, 37559.22) * mm});
            skLineSegment(sketch, "E1158", {"start": v(1423.46, 37759.08) * mm, "end": v(1373.87, 37752.72) * mm});
            skLineSegment(sketch, "E1159", {"start": v(1373.87, 37752.72) * mm, "end": v(1369.8, 37784.46) * mm});
            skLineSegment(sketch, "E1160", {"start": v(1369.8, 37784.46) * mm, "end": v(1419.39, 37790.82) * mm});
            skLineSegment(sketch, "E1161", {"start": v(1419.39, 37790.82) * mm, "end": v(1423.46, 37759.08) * mm});
            skLineSegment(sketch, "E1162", {"start": v(2837.72, 37737.35) * mm, "end": v(2788.13, 37730.99) * mm});
            skLineSegment(sketch, "E1163", {"start": v(2788.13, 37730.99) * mm, "end": v(2762.49, 37930.85) * mm});
            skLineSegment(sketch, "E1164", {"start": v(2762.49, 37930.85) * mm, "end": v(2812.08, 37937.21) * mm});
            skLineSegment(sketch, "E1165", {"start": v(2812.08, 37937.21) * mm, "end": v(2837.72, 37737.35) * mm});
            skLineSegment(sketch, "E1166", {"start": v(828.34, 37682.74) * mm, "end": v(778.74, 37676.38) * mm});
            skLineSegment(sketch, "E1167", {"start": v(778.74, 37676.38) * mm, "end": v(774.67, 37708.12) * mm});
            skLineSegment(sketch, "E1168", {"start": v(774.67, 37708.12) * mm, "end": v(824.27, 37714.48) * mm});
            skLineSegment(sketch, "E1169", {"start": v(824.27, 37714.48) * mm, "end": v(828.34, 37682.74) * mm});
            skLineSegment(sketch, "E1170", {"start": v(2812.08, 37937.21) * mm, "end": v(2762.49, 37930.85) * mm});
            skLineSegment(sketch, "E1171", {"start": v(2762.49, 37930.85) * mm, "end": v(2758.42, 37962.6) * mm});
            skLineSegment(sketch, "E1172", {"start": v(2758.42, 37962.6) * mm, "end": v(2808.01, 37968.95) * mm});
            skLineSegment(sketch, "E1173", {"start": v(2808.01, 37968.95) * mm, "end": v(2812.08, 37937.21) * mm});
            skArc(sketch, "E1174", {"start": v(2132.75, 37509) * mm, "mid": v(2152.19, 37635.43) * mm, "end": v(2147.81, 37763.28) * mm});
            skLineSegment(sketch, "E1175", {"start": v(2836.77, 37646.5) * mm, "end": v(2825.32, 37735.76) * mm});
            skLineSegment(sketch, "E1176", {"start": v(2824.38, 37644.9) * mm, "end": v(2812.92, 37734.17) * mm});
            skLineSegment(sketch, "E1177", {"start": v(2849.17, 37648.08) * mm, "end": v(2837.72, 37737.35) * mm});
            skLineSegment(sketch, "E1178", {"start": v(2836.77, 37646.5) * mm, "end": v(2849.17, 37648.08) * mm});
            skLineSegment(sketch, "E1179", {"start": v(2849.17, 37648.08) * mm, "end": v(2850.76, 37635.68) * mm});
            skLineSegment(sketch, "E1180", {"start": v(2850.76, 37635.68) * mm, "end": v(2825.97, 37632.5) * mm});
            skLineSegment(sketch, "E1181", {"start": v(2825.97, 37632.5) * mm, "end": v(2824.38, 37644.9) * mm});
            skLineSegment(sketch, "E1182", {"start": v(816.78, 37478.1) * mm, "end": v(828.23, 37388.84) * mm});
            skLineSegment(sketch, "E1183", {"start": v(829.18, 37479.7) * mm, "end": v(840.63, 37390.43) * mm});
            skLineSegment(sketch, "E1184", {"start": v(804.38, 37476.51) * mm, "end": v(815.83, 37387.25) * mm});
            skLineSegment(sketch, "E1185", {"start": v(828.23, 37388.84) * mm, "end": v(815.83, 37387.25) * mm});
            skLineSegment(sketch, "E1186", {"start": v(815.83, 37387.25) * mm, "end": v(817.42, 37374.85) * mm});
            skLineSegment(sketch, "E1187", {"start": v(817.42, 37374.85) * mm, "end": v(842.22, 37378.03) * mm});
            skLineSegment(sketch, "E1188", {"start": v(842.22, 37378.03) * mm, "end": v(840.63, 37390.43) * mm});
            skLineSegment(sketch, "E1189", {"start": v(-4283.18, 35844.63) * mm, "end": v(-2420.32, 29690.08) * mm});
            skLineSegment(sketch, "E1190", {"start": v(-4267.6, 35836.28) * mm, "end": v(-2411.98, 29705.67) * mm});
            skLineSegment(sketch, "E1191", {"start": v(-4298.76, 35852.97) * mm, "end": v(-2428.66, 29674.5) * mm});
            skLineSegment(sketch, "E1192", {"start": v(-4319.96, 35864.31) * mm, "end": v(-2440.01, 29653.3) * mm});
            skLineSegment(sketch, "E1193", {"start": v(-4444.64, 35931.06) * mm, "end": v(-2506.75, 29528.62) * mm});
            skLineSegment(sketch, "E1194", {"start": v(-4463.34, 35941.07) * mm, "end": v(-2516.76, 29509.92) * mm});
            skLineSegment(sketch, "E1195", {"start": v(-4588.02, 36007.8) * mm, "end": v(-2583.5, 29385.24) * mm});
            skLineSegment(sketch, "E1196", {"start": v(-4686.52, 36060.54) * mm, "end": v(-2636.23, 29286.74) * mm});
            skLineSegment(sketch, "E1197", {"start": v(-789.5, 30183.7) * mm, "end": v(-448.47, 30286.92) * mm});
            skLineSegment(sketch, "E1198", {"start": v(-793.12, 30195.66) * mm, "end": v(-444.35, 30301.23) * mm});
            skLineSegment(sketch, "E1199", {"start": v(-785.87, 30171.74) * mm, "end": v(-452.6, 30272.61) * mm});
            skLineSegment(sketch, "E1200", {"start": v(-780.95, 30155.47) * mm, "end": v(-458.2, 30253.16) * mm});
            skLineSegment(sketch, "E1201", {"start": v(-751.98, 30059.75) * mm, "end": v(-491.14, 30138.7) * mm});
            skLineSegment(sketch, "E1202", {"start": v(-747.63, 30045.4) * mm, "end": v(-496.08, 30121.54) * mm});
            skLineSegment(sketch, "E1203", {"start": v(-718.66, 29949.68) * mm, "end": v(-529.03, 30007.08) * mm});
            skLineSegment(sketch, "E1204", {"start": v(-695.78, 29874.07) * mm, "end": v(-555.06, 29916.66) * mm});
            skLineSegment(sketch, "E1205", {"start": v(-2420.32, 29690.08) * mm, "end": v(-2177.32, 29763.64) * mm});
            skLineSegment(sketch, "E1206", {"start": v(-2411.98, 29705.67) * mm, "end": v(-2180.94, 29775.6) * mm});
            skLineSegment(sketch, "E1207", {"start": v(-2428.66, 29674.5) * mm, "end": v(-2173.7, 29751.67) * mm});
            skLineSegment(sketch, "E1208", {"start": v(-2440.01, 29653.3) * mm, "end": v(-2168.77, 29735.4) * mm});
            skLineSegment(sketch, "E1209", {"start": v(-2506.75, 29528.62) * mm, "end": v(-2139.8, 29639.69) * mm});
            skLineSegment(sketch, "E1210", {"start": v(-2516.76, 29509.92) * mm, "end": v(-2135.45, 29625.33) * mm});
            skLineSegment(sketch, "E1211", {"start": v(-2583.5, 29385.24) * mm, "end": v(-2106.48, 29529.62) * mm});
            skLineSegment(sketch, "E1212", {"start": v(-2636.23, 29286.74) * mm, "end": v(-2083.6, 29454) * mm});
            skLineSegment(sketch, "E1213", {"start": v(-2083.6, 29454) * mm, "end": v(-2180.94, 29775.6) * mm});
            skLineSegment(sketch, "E1214", {"start": v(-695.78, 29874.07) * mm, "end": v(-793.12, 30195.66) * mm});
            skLineSegment(sketch, "E1215", {"start": v(-2053.7, 29527.83) * mm, "end": v(-1527.29, 29687.17) * mm});
            skLineSegment(sketch, "E1216", {"start": v(-1527.29, 29687.17) * mm, "end": v(-1518.6, 29658.46) * mm});
            skLineSegment(sketch, "E1217", {"start": v(-1518.6, 29658.46) * mm, "end": v(-2045.01, 29499.12) * mm});
            skLineSegment(sketch, "E1218", {"start": v(-2045.01, 29499.12) * mm, "end": v(-2053.7, 29527.83) * mm});
            skLineSegment(sketch, "E1219", {"start": v(-809.98, 29964.88) * mm, "end": v(-1493.81, 30019.42) * mm});
            skLineSegment(sketch, "E1220", {"start": v(-1403.67, 29737.85) * mm, "end": v(-844.71, 29907.04) * mm});
            skLineSegment(sketch, "E1221", {"start": v(-844.71, 29907.04) * mm, "end": v(-836.02, 29878.33) * mm});
            skLineSegment(sketch, "E1222", {"start": v(-836.02, 29878.33) * mm, "end": v(-1394.98, 29709.14) * mm});
            skLineSegment(sketch, "E1223", {"start": v(-1394.98, 29709.14) * mm, "end": v(-1403.67, 29737.85) * mm});
            skLineSegment(sketch, "E1224", {"start": v(-1576.97, 29851.31) * mm, "end": v(-1529.12, 29865.8) * mm});
            skLineSegment(sketch, "E1225", {"start": v(-1529.12, 29865.8) * mm, "end": v(-1470.74, 29672.94) * mm});
            skLineSegment(sketch, "E1226", {"start": v(-1470.74, 29672.94) * mm, "end": v(-1518.6, 29658.46) * mm});
            skLineSegment(sketch, "E1227", {"start": v(-1518.6, 29658.46) * mm, "end": v(-1576.97, 29851.31) * mm});
            skLineSegment(sketch, "E1228", {"start": v(-2103.39, 29691.98) * mm, "end": v(-763.42, 30097.56) * mm});
            skLineSegment(sketch, "E1229", {"start": v(-2083.6, 29454) * mm, "end": v(-695.78, 29874.07) * mm});
            skLineSegment(sketch, "E1230", {"start": v(-1466.56, 29766.15) * mm, "end": v(-1464.83, 29760.4) * mm});
            skLineSegment(sketch, "E1231", {"start": v(-1464.83, 29760.4) * mm, "end": v(-1494.5, 29751.42) * mm});
            skLineSegment(sketch, "E1232", {"start": v(-1494.5, 29751.42) * mm, "end": v(-1470.74, 29672.94) * mm});
            skLineSegment(sketch, "E1233", {"start": v(-1470.74, 29672.94) * mm, "end": v(-1391.3, 29696.99) * mm});
            skLineSegment(sketch, "E1234", {"start": v(-1391.3, 29696.99) * mm, "end": v(-1416.8, 29781.21) * mm});
            skLineSegment(sketch, "E1235", {"start": v(-1416.8, 29781.21) * mm, "end": v(-1466.56, 29766.15) * mm});
            skLineSegment(sketch, "E1236", {"start": v(-1518.6, 29658.46) * mm, "end": v(-1470.74, 29672.94) * mm});
            skLineSegment(sketch, "E1237", {"start": v(-1470.74, 29672.94) * mm, "end": v(-1461.47, 29642.31) * mm});
            skLineSegment(sketch, "E1238", {"start": v(-1461.47, 29642.31) * mm, "end": v(-1509.33, 29627.83) * mm});
            skLineSegment(sketch, "E1239", {"start": v(-1509.33, 29627.83) * mm, "end": v(-1518.6, 29658.46) * mm});
            skLineSegment(sketch, "E1240", {"start": v(-776.66, 29968.7) * mm, "end": v(-808.24, 29959.14) * mm});
            skLineSegment(sketch, "E1241", {"start": v(-808.24, 29959.14) * mm, "end": v(-809.98, 29964.88) * mm});
            skLineSegment(sketch, "E1242", {"start": v(-809.98, 29964.88) * mm, "end": v(-857.84, 29950.4) * mm});
            skLineSegment(sketch, "E1243", {"start": v(-857.84, 29950.4) * mm, "end": v(-832.34, 29866.17) * mm});
            skLineSegment(sketch, "E1244", {"start": v(-832.34, 29866.17) * mm, "end": v(-752.9, 29890.22) * mm});
            skLineSegment(sketch, "E1245", {"start": v(-752.9, 29890.22) * mm, "end": v(-776.66, 29968.7) * mm});
            skLineSegment(sketch, "E1246", {"start": v(-811.28, 30083.07) * mm, "end": v(-763.42, 30097.56) * mm});
            skLineSegment(sketch, "E1247", {"start": v(-763.42, 30097.56) * mm, "end": v(-705.05, 29904.7) * mm});
            skLineSegment(sketch, "E1248", {"start": v(-705.05, 29904.7) * mm, "end": v(-752.9, 29890.22) * mm});
            skLineSegment(sketch, "E1249", {"start": v(-752.9, 29890.22) * mm, "end": v(-811.28, 30083.07) * mm});
            skLineSegment(sketch, "E1250", {"start": v(-752.9, 29890.22) * mm, "end": v(-705.05, 29904.7) * mm});
            skLineSegment(sketch, "E1251", {"start": v(-705.05, 29904.7) * mm, "end": v(-695.78, 29874.07) * mm});
            skLineSegment(sketch, "E1252", {"start": v(-695.78, 29874.07) * mm, "end": v(-743.63, 29859.59) * mm});
            skLineSegment(sketch, "E1253", {"start": v(-743.63, 29859.59) * mm, "end": v(-752.9, 29890.22) * mm});
            skLineSegment(sketch, "E1254", {"start": v(-2151.24, 29677.5) * mm, "end": v(-2103.39, 29691.98) * mm});
            skLineSegment(sketch, "E1255", {"start": v(-2103.39, 29691.98) * mm, "end": v(-2045.01, 29499.12) * mm});
            skLineSegment(sketch, "E1256", {"start": v(-2045.01, 29499.12) * mm, "end": v(-2092.87, 29484.64) * mm});
            skLineSegment(sketch, "E1257", {"start": v(-2092.87, 29484.64) * mm, "end": v(-2151.24, 29677.5) * mm});
            skLineSegment(sketch, "E1258", {"start": v(-2092.87, 29484.64) * mm, "end": v(-2045.01, 29499.12) * mm});
            skLineSegment(sketch, "E1259", {"start": v(-2045.01, 29499.12) * mm, "end": v(-2035.74, 29468.5) * mm});
            skLineSegment(sketch, "E1260", {"start": v(-2035.74, 29468.5) * mm, "end": v(-2083.6, 29454) * mm});
            skLineSegment(sketch, "E1261", {"start": v(-2083.6, 29454) * mm, "end": v(-2092.87, 29484.64) * mm});
            skArc(sketch, "E1262", {"start": v(-1493.81, 30019.42) * mm, "mid": v(-1492.05, 29891.5) * mm, "end": v(-1466.56, 29766.15) * mm});
            skLineSegment(sketch, "E1263", {"start": v(-801.46, 30180.08) * mm, "end": v(-775.39, 30093.94) * mm});
            skLineSegment(sketch, "E1264", {"start": v(-793.12, 30195.66) * mm, "end": v(-763.42, 30097.56) * mm});
            skLineSegment(sketch, "E1265", {"start": v(-817.04, 30188.42) * mm, "end": v(-787.35, 30090.32) * mm});
            skLineSegment(sketch, "E1266", {"start": v(-801.46, 30180.08) * mm, "end": v(-789.5, 30183.7) * mm});
            skLineSegment(sketch, "E1267", {"start": v(-793.12, 30195.66) * mm, "end": v(-817.04, 30188.42) * mm});
            skLineSegment(sketch, "E1268", {"start": v(-789.5, 30183.7) * mm, "end": v(-801.46, 30180.08) * mm});
            skLineSegment(sketch, "E1269", {"start": v(-2139.28, 29681.12) * mm, "end": v(-2165.35, 29767.26) * mm});
            skLineSegment(sketch, "E1270", {"start": v(-2151.24, 29677.5) * mm, "end": v(-2180.94, 29775.6) * mm});
            skLineSegment(sketch, "E1271", {"start": v(-2127.31, 29684.74) * mm, "end": v(-2157, 29782.84) * mm});
            skLineSegment(sketch, "E1272", {"start": v(-2165.35, 29767.26) * mm, "end": v(-2177.32, 29763.64) * mm});
            skLineSegment(sketch, "E1273", {"start": v(-2180.94, 29775.6) * mm, "end": v(-2157, 29782.84) * mm});
            skLineSegment(sketch, "E1274", {"start": v(-2177.32, 29763.64) * mm, "end": v(-2165.35, 29767.26) * mm});
            skLineSegment(sketch, "E1275", {"start": v(-2951.22, 36247.78) * mm, "end": v(-4283.18, 35844.63) * mm});
            skLineSegment(sketch, "E1276", {"start": v(-2947.6, 36235.82) * mm, "end": v(-4267.6, 35836.28) * mm});
            skLineSegment(sketch, "E1277", {"start": v(-2954.85, 36259.75) * mm, "end": v(-4298.76, 35852.97) * mm});
            skLineSegment(sketch, "E1278", {"start": v(-2959.77, 36276.02) * mm, "end": v(-4319.96, 35864.31) * mm});
            skLineSegment(sketch, "E1279", {"start": v(-2988.74, 36371.73) * mm, "end": v(-4444.64, 35931.06) * mm});
            skLineSegment(sketch, "E1280", {"start": v(-2993.09, 36386.08) * mm, "end": v(-4463.34, 35941.07) * mm});
            skLineSegment(sketch, "E1281", {"start": v(-3022.06, 36481.8) * mm, "end": v(-4588.02, 36007.8) * mm});
            skLineSegment(sketch, "E1282", {"start": v(-3044.94, 36557.4) * mm, "end": v(-4686.52, 36060.54) * mm});
            skLineSegment(sketch, "E1283", {"start": v(811.55, 37386.7) * mm, "end": v(-989.13, 36841.67) * mm});
            skLineSegment(sketch, "E1284", {"start": v(814.17, 37374.43) * mm, "end": v(-985.51, 36829.7) * mm});
            skLineSegment(sketch, "E1285", {"start": v(808.92, 37398.96) * mm, "end": v(-992.75, 36853.63) * mm});
            skLineSegment(sketch, "E1286", {"start": v(805.35, 37415.64) * mm, "end": v(-997.68, 36869.9) * mm});
            skLineSegment(sketch, "E1287", {"start": v(784.36, 37513.77) * mm, "end": v(-1026.65, 36965.61) * mm});
            skLineSegment(sketch, "E1288", {"start": v(781.21, 37528.49) * mm, "end": v(-1031, 36979.97) * mm});
            skLineSegment(sketch, "E1289", {"start": v(760.22, 37626.62) * mm, "end": v(-1059.97, 37075.68) * mm});
            skLineSegment(sketch, "E1290", {"start": v(743.64, 37704.14) * mm, "end": v(-1082.85, 37151.3) * mm});
            skLineSegment(sketch, "E1291", {"start": v(-1082.85, 37151.3) * mm, "end": v(-985.51, 36829.7) * mm});
            skLineSegment(sketch, "E1292", {"start": v(-3044.94, 36557.4) * mm, "end": v(-2947.6, 36235.82) * mm});
            skLineSegment(sketch, "E1293", {"start": v(-1109.85, 37067.9) * mm, "end": v(-1636.26, 36908.56) * mm});
            skLineSegment(sketch, "E1294", {"start": v(-1636.26, 36908.56) * mm, "end": v(-1647.85, 36946.85) * mm});
            skLineSegment(sketch, "E1295", {"start": v(-1647.85, 36946.85) * mm, "end": v(-1121.44, 37106.18) * mm});
            skLineSegment(sketch, "E1296", {"start": v(-1121.44, 37106.18) * mm, "end": v(-1109.85, 37067.9) * mm});
            skLineSegment(sketch, "E1297", {"start": v(-2356.47, 36640.42) * mm, "end": v(-1672.64, 36585.88) * mm});
            skLineSegment(sketch, "E1298", {"start": v(-1759.88, 36857.88) * mm, "end": v(-2318.84, 36688.7) * mm});
            skLineSegment(sketch, "E1299", {"start": v(-2318.84, 36688.7) * mm, "end": v(-2330.43, 36726.98) * mm});
            skLineSegment(sketch, "E1300", {"start": v(-2330.43, 36726.98) * mm, "end": v(-1771.47, 36896.16) * mm});
            skLineSegment(sketch, "E1301", {"start": v(-1771.47, 36896.16) * mm, "end": v(-1759.88, 36857.88) * mm});
            skLineSegment(sketch, "E1302", {"start": v(-2449.81, 36662.32) * mm, "end": v(-2976.23, 36502.98) * mm});
            skLineSegment(sketch, "E1303", {"start": v(-2976.23, 36502.98) * mm, "end": v(-2987.82, 36541.27) * mm});
            skLineSegment(sketch, "E1304", {"start": v(-2987.82, 36541.27) * mm, "end": v(-2461.4, 36700.6) * mm});
            skLineSegment(sketch, "E1305", {"start": v(-2461.4, 36700.6) * mm, "end": v(-2449.81, 36662.32) * mm});
            skLineSegment(sketch, "E1306", {"start": v(-1589.48, 36753.99) * mm, "end": v(-1637.33, 36739.5) * mm});
            skLineSegment(sketch, "E1307", {"start": v(-1637.33, 36739.5) * mm, "end": v(-1695.7, 36932.36) * mm});
            skLineSegment(sketch, "E1308", {"start": v(-1695.7, 36932.36) * mm, "end": v(-1647.85, 36946.85) * mm});
            skLineSegment(sketch, "E1309", {"start": v(-1647.85, 36946.85) * mm, "end": v(-1589.48, 36753.99) * mm});
            skLineSegment(sketch, "E1310", {"start": v(-2929.44, 36348.4) * mm, "end": v(-2977.3, 36333.92) * mm});
            skLineSegment(sketch, "E1311", {"start": v(-2977.3, 36333.92) * mm, "end": v(-3035.67, 36526.78) * mm});
            skLineSegment(sketch, "E1312", {"start": v(-3035.67, 36526.78) * mm, "end": v(-2987.82, 36541.27) * mm});
            skLineSegment(sketch, "E1313", {"start": v(-2987.82, 36541.27) * mm, "end": v(-2929.44, 36348.4) * mm});
            skLineSegment(sketch, "E1314", {"start": v(-1063.06, 36913.32) * mm, "end": v(-2929.44, 36348.4) * mm});
            skLineSegment(sketch, "E1315", {"start": v(-1082.85, 37151.3) * mm, "end": v(-3044.94, 36557.4) * mm});
            skLineSegment(sketch, "E1316", {"start": v(-1699.88, 36839.15) * mm, "end": v(-1701.62, 36844.9) * mm});
            skLineSegment(sketch, "E1317", {"start": v(-1701.62, 36844.9) * mm, "end": v(-1671.95, 36853.88) * mm});
            skLineSegment(sketch, "E1318", {"start": v(-1671.95, 36853.88) * mm, "end": v(-1695.7, 36932.36) * mm});
            skLineSegment(sketch, "E1319", {"start": v(-1695.7, 36932.36) * mm, "end": v(-1775.15, 36908.32) * mm});
            skLineSegment(sketch, "E1320", {"start": v(-1775.15, 36908.32) * mm, "end": v(-1749.65, 36824.09) * mm});
            skLineSegment(sketch, "E1321", {"start": v(-1749.65, 36824.09) * mm, "end": v(-1699.88, 36839.15) * mm});
            skLineSegment(sketch, "E1322", {"start": v(-1647.85, 36946.85) * mm, "end": v(-1695.7, 36932.36) * mm});
            skLineSegment(sketch, "E1323", {"start": v(-1695.7, 36932.36) * mm, "end": v(-1704.98, 36962.99) * mm});
            skLineSegment(sketch, "E1324", {"start": v(-1704.98, 36962.99) * mm, "end": v(-1657.12, 36977.47) * mm});
            skLineSegment(sketch, "E1325", {"start": v(-1657.12, 36977.47) * mm, "end": v(-1647.85, 36946.85) * mm});
            skLineSegment(sketch, "E1326", {"start": v(-2389.8, 36636.6) * mm, "end": v(-2358.2, 36646.16) * mm});
            skLineSegment(sketch, "E1327", {"start": v(-2358.2, 36646.16) * mm, "end": v(-2356.47, 36640.42) * mm});
            skLineSegment(sketch, "E1328", {"start": v(-2356.47, 36640.42) * mm, "end": v(-2308.61, 36654.9) * mm});
            skLineSegment(sketch, "E1329", {"start": v(-2308.61, 36654.9) * mm, "end": v(-2334.1, 36739.13) * mm});
            skLineSegment(sketch, "E1330", {"start": v(-2334.1, 36739.13) * mm, "end": v(-2413.55, 36715.09) * mm});
            skLineSegment(sketch, "E1331", {"start": v(-2413.55, 36715.09) * mm, "end": v(-2389.8, 36636.6) * mm});
            skLineSegment(sketch, "E1332", {"start": v(-2355.17, 36522.23) * mm, "end": v(-2403.03, 36507.74) * mm});
            skLineSegment(sketch, "E1333", {"start": v(-2403.03, 36507.74) * mm, "end": v(-2461.4, 36700.6) * mm});
            skLineSegment(sketch, "E1334", {"start": v(-2461.4, 36700.6) * mm, "end": v(-2413.55, 36715.09) * mm});
            skLineSegment(sketch, "E1335", {"start": v(-2413.55, 36715.09) * mm, "end": v(-2355.17, 36522.23) * mm});
            skLineSegment(sketch, "E1336", {"start": v(-2413.55, 36715.09) * mm, "end": v(-2461.4, 36700.6) * mm});
            skLineSegment(sketch, "E1337", {"start": v(-2461.4, 36700.6) * mm, "end": v(-2470.67, 36731.23) * mm});
            skLineSegment(sketch, "E1338", {"start": v(-2470.67, 36731.23) * mm, "end": v(-2422.82, 36745.71) * mm});
            skLineSegment(sketch, "E1339", {"start": v(-2422.82, 36745.71) * mm, "end": v(-2413.55, 36715.09) * mm});
            skLineSegment(sketch, "E1340", {"start": v(-1015.2, 36927.8) * mm, "end": v(-1063.06, 36913.32) * mm});
            skLineSegment(sketch, "E1341", {"start": v(-1063.06, 36913.32) * mm, "end": v(-1121.44, 37106.18) * mm});
            skLineSegment(sketch, "E1342", {"start": v(-1121.44, 37106.18) * mm, "end": v(-1073.58, 37120.67) * mm});
            skLineSegment(sketch, "E1343", {"start": v(-1073.58, 37120.67) * mm, "end": v(-1015.2, 36927.8) * mm});
            skLineSegment(sketch, "E1344", {"start": v(-2987.82, 36541.27) * mm, "end": v(-3035.67, 36526.78) * mm});
            skLineSegment(sketch, "E1345", {"start": v(-3035.67, 36526.78) * mm, "end": v(-3044.94, 36557.4) * mm});
            skLineSegment(sketch, "E1346", {"start": v(-3044.94, 36557.4) * mm, "end": v(-2997.09, 36571.9) * mm});
            skLineSegment(sketch, "E1347", {"start": v(-2997.09, 36571.9) * mm, "end": v(-2987.82, 36541.27) * mm});
            skLineSegment(sketch, "E1348", {"start": v(-1073.58, 37120.67) * mm, "end": v(-1121.44, 37106.18) * mm});
            skLineSegment(sketch, "E1349", {"start": v(-1121.44, 37106.18) * mm, "end": v(-1130.7, 37136.8) * mm});
            skLineSegment(sketch, "E1350", {"start": v(-1130.7, 37136.8) * mm, "end": v(-1082.85, 37151.3) * mm});
            skLineSegment(sketch, "E1351", {"start": v(-1082.85, 37151.3) * mm, "end": v(-1073.58, 37120.67) * mm});
            skArc(sketch, "E1352", {"start": v(-1672.64, 36585.88) * mm, "mid": v(-1674.4, 36713.8) * mm, "end": v(-1699.88, 36839.15) * mm});
            skLineSegment(sketch, "E1353", {"start": v(-1001.1, 36838.05) * mm, "end": v(-1027.17, 36924.19) * mm});
            skLineSegment(sketch, "E1354", {"start": v(-1013.06, 36834.42) * mm, "end": v(-1039.13, 36920.56) * mm});
            skLineSegment(sketch, "E1355", {"start": v(-989.13, 36841.67) * mm, "end": v(-1015.2, 36927.8) * mm});
            skLineSegment(sketch, "E1356", {"start": v(-1001.1, 36838.05) * mm, "end": v(-989.13, 36841.67) * mm});
            skLineSegment(sketch, "E1357", {"start": v(-989.13, 36841.67) * mm, "end": v(-985.51, 36829.7) * mm});
            skLineSegment(sketch, "E1358", {"start": v(-985.51, 36829.7) * mm, "end": v(-1009.44, 36822.46) * mm});
            skLineSegment(sketch, "E1359", {"start": v(-1009.44, 36822.46) * mm, "end": v(-1013.06, 36834.42) * mm});
            skLineSegment(sketch, "E1360", {"start": v(-2965.33, 36337.54) * mm, "end": v(-2939.26, 36251.4) * mm});
            skLineSegment(sketch, "E1361", {"start": v(-2953.37, 36341.16) * mm, "end": v(-2927.3, 36255.02) * mm});
            skLineSegment(sketch, "E1362", {"start": v(-2977.3, 36333.92) * mm, "end": v(-2951.22, 36247.78) * mm});
            skLineSegment(sketch, "E1363", {"start": v(-2939.26, 36251.4) * mm, "end": v(-2951.22, 36247.78) * mm});
            skLineSegment(sketch, "E1364", {"start": v(-2951.22, 36247.78) * mm, "end": v(-2947.6, 36235.82) * mm});
            skLineSegment(sketch, "E1365", {"start": v(-2947.6, 36235.82) * mm, "end": v(-2923.68, 36243.06) * mm});
            skLineSegment(sketch, "E1366", {"start": v(-2923.68, 36243.06) * mm, "end": v(-2927.3, 36255.02) * mm});
            skLineSegment(sketch, "E1367", {"start": v(8303.3, 25022.24) * mm, "end": v(8590.44, 25109.15) * mm});
            skLineSegment(sketch, "E1368", {"start": v(8590.44, 25109.15) * mm, "end": v(9039.33, 23626.12) * mm});
            skLineSegment(sketch, "E1369", {"start": v(9039.33, 23626.12) * mm, "end": v(8752.2, 23539.21) * mm});
            skLineSegment(sketch, "E1370", {"start": v(8752.2, 23539.21) * mm, "end": v(8303.3, 25022.24) * mm});
            skLineSegment(sketch, "E1371", {"start": v(197.13, 30196.02) * mm, "end": v(-281.42, 30051.14) * mm});
            skLineSegment(sketch, "E1372", {"start": v(-281.42, 30051.14) * mm, "end": v(-353.86, 30290.42) * mm});
            skLineSegment(sketch, "E1373", {"start": v(-353.86, 30290.42) * mm, "end": v(124.69, 30435.3) * mm});
            skLineSegment(sketch, "E1374", {"start": v(124.69, 30435.3) * mm, "end": v(197.13, 30196.02) * mm});
            skLineSegment(sketch, "E1375", {"start": v(8948.07, 22978.3) * mm, "end": v(9187.35, 23050.73) * mm});
            skLineSegment(sketch, "E1376", {"start": v(9067.7, 23014.51) * mm, "end": v(9011.18, 23201.26) * mm});
            skLineSegment(sketch, "E1377", {"start": v(9067.7, 23014.51) * mm, "end": v(9049.5, 23009) * mm});
            skCircle(sketch, "E1378", {"center": v(4156.9, 27384.5) * mm, "radius": 200 * mm});
            skLineSegment(sketch, "E1379", {"start": v(8752.39, 23538.73) * mm, "end": v(9409.92, 21366) * mm});
            skLineSegment(sketch, "E1380", {"start": v(-353.88, 30290.43) * mm, "end": v(124.67, 30435.31) * mm});
            skLineSegment(sketch, "E1381", {"start": v(197.11, 30196.04) * mm, "end": v(124.67, 30435.31) * mm});
            skLineSegment(sketch, "E1382", {"start": v(-281.44, 30051.16) * mm, "end": v(197.11, 30196.04) * mm});
            skLineSegment(sketch, "E1383", {"start": v(-281.44, 30051.16) * mm, "end": v(-353.88, 30290.43) * mm});
            skLineSegment(sketch, "E1384", {"start": v(-2472.02, 30328.5) * mm, "end": v(-2327.14, 29849.96) * mm});
            skLineSegment(sketch, "E1385", {"start": v(-2566.42, 29777.52) * mm, "end": v(-2327.14, 29849.96) * mm});
            skLineSegment(sketch, "E1386", {"start": v(-2711.3, 30256.07) * mm, "end": v(-2566.42, 29777.52) * mm});
            skLineSegment(sketch, "E1387", {"start": v(-2711.3, 30256.07) * mm, "end": v(-2472.02, 30328.5) * mm});
            skLineSegment(sketch, "E1388", {"start": v(-4186.63, 35993.38) * mm, "end": v(-4041.78, 35514.82) * mm});
            skLineSegment(sketch, "E1389", {"start": v(-4281.06, 35442.4) * mm, "end": v(-4041.78, 35514.82) * mm});
            skLineSegment(sketch, "E1390", {"start": v(-4425.9, 35920.95) * mm, "end": v(-4281.06, 35442.4) * mm});
            skLineSegment(sketch, "E1391", {"start": v(-4425.9, 35920.95) * mm, "end": v(-4186.63, 35993.38) * mm});
            skLineSegment(sketch, "E1392", {"start": v(-511.89, 37105.65) * mm, "end": v(-33.33, 37250.5) * mm});
            skLineSegment(sketch, "E1393", {"start": v(39.1, 37011.22) * mm, "end": v(-33.33, 37250.5) * mm});
            skLineSegment(sketch, "E1394", {"start": v(-439.46, 36866.37) * mm, "end": v(39.1, 37011.22) * mm});
            skLineSegment(sketch, "E1395", {"start": v(-439.46, 36866.37) * mm, "end": v(-511.89, 37105.65) * mm});
            skLineSegment(sketch, "E1396", {"start": v(4693.12, 37985.2) * mm, "end": v(8590.44, 25109.15) * mm});
            skLineSegment(sketch, "E1397", {"start": v(4405.99, 37898.29) * mm, "end": v(8303.3, 25022.24) * mm});
            skLineSegment(sketch, "E1398", {"start": v(4405.99, 37898.29) * mm, "end": v(4693.12, 37985.2) * mm});
            skLineSegment(sketch, "E1399", {"start": v(8030.58, 19741.8) * mm, "end": v(7885.73, 20220.35) * mm});
            skArc(sketch, "E1400", {"start": v(2269.14, 28633.68) * mm, "mid": v(2276.69, 28709.85) * mm, "end": v(2335.88, 28758.37) * mm});
            skLineSegment(sketch, "E1401", {"start": v(2335.88, 28758.37) * mm, "end": v(2878.3, 28922.55) * mm});
            skArc(sketch, "E1402", {"start": v(2878.3, 28922.55) * mm, "mid": v(2954.46, 28915) * mm, "end": v(3002.98, 28855.8) * mm});
            skLineSegment(sketch, "E1403", {"start": v(3002.98, 28855.8) * mm, "end": v(3296.16, 27887.2) * mm});
            skArc(sketch, "E1404", {"start": v(3296.16, 27887.2) * mm, "mid": v(3288.6, 27811.04) * mm, "end": v(3229.42, 27762.52) * mm});
            skLineSegment(sketch, "E1405", {"start": v(3229.42, 27762.52) * mm, "end": v(2687, 27598.34) * mm});
            skLineSegment(sketch, "E1406", {"start": v(4965.73, 23360.9) * mm, "end": v(4664.93, 23706.28) * mm});
            skLineSegment(sketch, "E1407", {"start": v(4664.93, 23706.28) * mm, "end": v(4755.42, 23785.1) * mm});
            skLineSegment(sketch, "E1408", {"start": v(4755.42, 23785.1) * mm, "end": v(5056.22, 23439.72) * mm});
            skLineSegment(sketch, "E1409", {"start": v(5056.22, 23439.72) * mm, "end": v(4965.73, 23360.9) * mm});
            skLineSegment(sketch, "E1410", {"start": v(4674.44, 23545.8) * mm, "end": v(4815.33, 23533.6) * mm});
            skLineSegment(sketch, "E1411", {"start": v(4815.33, 23533.6) * mm, "end": v(4803.13, 23392.71) * mm});
            skLineSegment(sketch, "E1412", {"start": v(4803.13, 23392.71) * mm, "end": v(4674.44, 23545.8) * mm});
            skLineSegment(sketch, "E1413", {"start": v(-436.04, 36975.35) * mm, "end": v(-370.87, 36760) * mm});
            skLineSegment(sketch, "E1414", {"start": v(-370.87, 36760) * mm, "end": v(-752.76, 36644.43) * mm});
            skLineSegment(sketch, "E1415", {"start": v(-752.76, 36644.43) * mm, "end": v(-817.94, 36859.78) * mm});
            skLineSegment(sketch, "E1416", {"start": v(-817.94, 36859.78) * mm, "end": v(-436.04, 36975.35) * mm});
            skLineSegment(sketch, "E1417", {"start": v(-494.77, 36722.5) * mm, "end": v(-480.29, 36674.65) * mm});
            skLineSegment(sketch, "E1418", {"start": v(-480.29, 36674.65) * mm, "end": v(-622.99, 36631.46) * mm});
            skLineSegment(sketch, "E1419", {"start": v(-622.99, 36631.46) * mm, "end": v(-637.47, 36679.32) * mm});
            skLineSegment(sketch, "E1420", {"start": v(-637.47, 36679.32) * mm, "end": v(-494.77, 36722.5) * mm});
            skLineSegment(sketch, "E1421", {"start": v(-570.8, 37337.8) * mm, "end": v(-1087.66, 37181.4) * mm});
            skLineSegment(sketch, "E1422", {"start": v(-771.24, 37240.58) * mm, "end": v(-866.95, 37211.62) * mm});
            skLineSegment(sketch, "E1423", {"start": v(-866.95, 37211.62) * mm, "end": v(-754.7, 36840.73) * mm});
            skArc(sketch, "E1424", {"start": v(-754.7, 36840.73) * mm, "mid": v(-692.94, 36809.25) * mm, "end": v(-659, 36869.7) * mm});
            skLineSegment(sketch, "E1425", {"start": v(-659, 36869.7) * mm, "end": v(-771.24, 37240.58) * mm});
            skLineSegment(sketch, "E1426", {"start": v(-807.47, 37360.3) * mm, "end": v(-772.69, 37245.37) * mm});
            skLineSegment(sketch, "E1427", {"start": v(-772.69, 37245.37) * mm, "end": v(-868.4, 37216.4) * mm});
            skLineSegment(sketch, "E1428", {"start": v(-868.4, 37216.4) * mm, "end": v(-903.18, 37331.34) * mm});
            skLineSegment(sketch, "E1429", {"start": v(-903.18, 37331.34) * mm, "end": v(-807.47, 37360.3) * mm});
            skLineSegment(sketch, "E1430", {"start": v(-715.26, 37262.75) * mm, "end": v(-713.81, 37257.96) * mm});
            skLineSegment(sketch, "E1431", {"start": v(-713.81, 37257.96) * mm, "end": v(-924.38, 37194.24) * mm});
            skLineSegment(sketch, "E1432", {"start": v(-924.38, 37194.24) * mm, "end": v(-925.83, 37199.02) * mm});
            skLineSegment(sketch, "E1433", {"start": v(-925.83, 37199.02) * mm, "end": v(-715.26, 37262.75) * mm});
            skLineSegment(sketch, "E1434", {"start": v(-661.9, 37086.54) * mm, "end": v(-660.45, 37081.76) * mm});
            skLineSegment(sketch, "E1435", {"start": v(-660.45, 37081.76) * mm, "end": v(-871.01, 37018.03) * mm});
            skLineSegment(sketch, "E1436", {"start": v(-871.01, 37018.03) * mm, "end": v(-872.46, 37022.82) * mm});
            skLineSegment(sketch, "E1437", {"start": v(-872.46, 37022.82) * mm, "end": v(-661.9, 37086.54) * mm});
            skLineSegment(sketch, "E1438", {"start": v(-859.07, 37344.69) * mm, "end": v(-884.06, 37337.19) * mm});
            skLineSegment(sketch, "E1439", {"start": v(-884.06, 37337.19) * mm, "end": v(-901.42, 37394.56) * mm});
            skLineSegment(sketch, "E1440", {"start": v(-901.42, 37394.56) * mm, "end": v(-844, 37411.94) * mm});
            skLineSegment(sketch, "E1441", {"start": v(-844, 37411.94) * mm, "end": v(-826.61, 37354.51) * mm});
            skLineSegment(sketch, "E1442", {"start": v(-826.61, 37354.51) * mm, "end": v(-859.07, 37344.69) * mm});
            skLineSegment(sketch, "E1443", {"start": v(-545.2, 36459.12) * mm, "end": v(-590.75, 36609.63) * mm});
            skLineSegment(sketch, "E1444", {"start": v(-590.75, 36609.63) * mm, "end": v(-495.04, 36638.6) * mm});
            skLineSegment(sketch, "E1445", {"start": v(-495.04, 36638.6) * mm, "end": v(-478.45, 36583.8) * mm});
            skLineSegment(sketch, "E1446", {"start": v(-478.45, 36583.8) * mm, "end": v(263.6, 36808.38) * mm});
            skLineSegment(sketch, "E1447", {"start": v(263.6, 36808.38) * mm, "end": v(1951.6, 31231.48) * mm});
            skLineSegment(sketch, "E1448", {"start": v(1951.6, 31231.48) * mm, "end": v(5860.45, 32414.6) * mm});
            skLineSegment(sketch, "E1449", {"start": v(5860.45, 32414.6) * mm, "end": v(6137.86, 31498.09) * mm});
            skLineSegment(sketch, "E1450", {"start": v(6137.86, 31498.09) * mm, "end": v(6042.15, 31469.12) * mm});
            skLineSegment(sketch, "E1451", {"start": v(6042.15, 31469.12) * mm, "end": v(5793.7, 32289.93) * mm});
            skLineSegment(sketch, "E1452", {"start": v(5793.7, 32289.93) * mm, "end": v(1884.86, 31106.8) * mm});
            skLineSegment(sketch, "E1453", {"start": v(1884.86, 31106.8) * mm, "end": v(196.85, 36683.7) * mm});
            skLineSegment(sketch, "E1454", {"start": v(196.85, 36683.7) * mm, "end": v(-497.34, 36473.6) * mm});
            skLineSegment(sketch, "E1455", {"start": v(-497.34, 36473.6) * mm, "end": v(-545.2, 36459.12) * mm});
            skLineSegment(sketch, "E1456", {"start": v(2834.55, 38123.59) * mm, "end": v(3288.83, 38181.86) * mm});
            skLineSegment(sketch, "E1457", {"start": v(3288.83, 38181.86) * mm, "end": v(3304.1, 38062.84) * mm});
            skLineSegment(sketch, "E1458", {"start": v(3304.1, 38062.84) * mm, "end": v(2849.82, 38004.56) * mm});
            skLineSegment(sketch, "E1459", {"start": v(2849.82, 38004.56) * mm, "end": v(2834.55, 38123.59) * mm});
            skLineSegment(sketch, "E1460", {"start": v(3062.96, 38142.8) * mm, "end": v(2961.17, 38936.3) * mm});
            skLineSegment(sketch, "E1461", {"start": v(2874.71, 38824.4) * mm, "end": v(2961.17, 38936.3) * mm});
            skLineSegment(sketch, "E1462", {"start": v(2961.17, 38936.3) * mm, "end": v(3073.08, 38849.85) * mm});
            skLineSegment(sketch, "E1463", {"start": v(3073.08, 38849.85) * mm, "end": v(2874.71, 38824.4) * mm});
            skLineSegment(sketch, "E1464", {"start": v(2331.57, 26371.66) * mm, "end": v(2030.77, 26717.04) * mm});
            skLineSegment(sketch, "E1465", {"start": v(2030.77, 26717.04) * mm, "end": v(2121.26, 26795.85) * mm});
            skLineSegment(sketch, "E1466", {"start": v(2121.26, 26795.85) * mm, "end": v(2422.06, 26450.48) * mm});
            skLineSegment(sketch, "E1467", {"start": v(2422.06, 26450.48) * mm, "end": v(2331.57, 26371.66) * mm});
            skArc(sketch, "E1468", {"start": v(-703.63, 37502.46) * mm, "mid": v(-730.29, 37505.1) * mm, "end": v(-747.27, 37525.82) * mm});
            skLineSegment(sketch, "E1469", {"start": v(-747.27, 37525.82) * mm, "end": v(-1019.28, 38424.52) * mm});
            skArc(sketch, "E1470", {"start": v(-1019.28, 38424.52) * mm, "mid": v(-1016.64, 38451.17) * mm, "end": v(-995.92, 38468.16) * mm});
            skLineSegment(sketch, "E1471", {"start": v(-995.92, 38468.16) * mm, "end": v(-501.25, 38617.88) * mm});
            skArc(sketch, "E1472", {"start": v(-501.25, 38617.88) * mm, "mid": v(-474.6, 38615.24) * mm, "end": v(-457.61, 38594.52) * mm});
            skLineSegment(sketch, "E1473", {"start": v(-457.61, 38594.52) * mm, "end": v(-185.6, 37695.83) * mm});
            skArc(sketch, "E1474", {"start": v(-185.6, 37695.83) * mm, "mid": v(-188.24, 37669.17) * mm, "end": v(-208.96, 37652.2) * mm});
            skLineSegment(sketch, "E1475", {"start": v(-208.96, 37652.2) * mm, "end": v(-703.63, 37502.46) * mm});
            skArc(sketch, "E1476", {"start": v(2331.2, 38107.6) * mm, "mid": v(2304.55, 38110.25) * mm, "end": v(2287.57, 38130.96) * mm});
            skLineSegment(sketch, "E1477", {"start": v(2287.57, 38130.96) * mm, "end": v(2015.55, 39029.66) * mm});
            skArc(sketch, "E1478", {"start": v(2015.55, 39029.66) * mm, "mid": v(2018.2, 39056.32) * mm, "end": v(2038.9, 39073.3) * mm});
            skLineSegment(sketch, "E1479", {"start": v(2038.9, 39073.3) * mm, "end": v(2533.58, 39223.02) * mm});
            skArc(sketch, "E1480", {"start": v(2533.58, 39223.02) * mm, "mid": v(2560.24, 39220.38) * mm, "end": v(2577.22, 39199.66) * mm});
            skLineSegment(sketch, "E1481", {"start": v(2577.22, 39199.66) * mm, "end": v(2849.23, 38300.97) * mm});
            skArc(sketch, "E1482", {"start": v(2849.23, 38300.97) * mm, "mid": v(2846.6, 38274.31) * mm, "end": v(2825.87, 38257.33) * mm});
            skLineSegment(sketch, "E1483", {"start": v(2825.87, 38257.33) * mm, "end": v(2331.2, 38107.6) * mm});
            skArc(sketch, "E1484", {"start": v(2379.2, 26143.37) * mm, "mid": v(2405.85, 26140.73) * mm, "end": v(2422.83, 26120.01) * mm});
            skArc(sketch, "E1485", {"start": v(5314.63, 22054.47) * mm, "mid": v(5311.99, 22027.81) * mm, "end": v(5291.27, 22010.83) * mm});
            skLineSegment(sketch, "E1486", {"start": v(716.1, 33838.68) * mm, "end": v(970.38, 32998.58) * mm});
            skLineSegment(sketch, "E1487", {"start": v(970.38, 32998.58) * mm, "end": v(700.26, 32916.82) * mm});
            skLineSegment(sketch, "E1488", {"start": v(700.26, 32916.82) * mm, "end": v(445.98, 33756.92) * mm});
            skLineSegment(sketch, "E1489", {"start": v(445.98, 33756.92) * mm, "end": v(716.1, 33838.68) * mm});
            skLineSegment(sketch, "E1490", {"start": v(727.53, 33815.17) * mm, "end": v(966.97, 33024.1) * mm});
            skLineSegment(sketch, "E1491", {"start": v(966.97, 33024.1) * mm, "end": v(717.1, 32948.47) * mm});
            skLineSegment(sketch, "E1492", {"start": v(717.1, 32948.47) * mm, "end": v(477.67, 33739.54) * mm});
            skLineSegment(sketch, "E1493", {"start": v(477.67, 33739.54) * mm, "end": v(727.53, 33815.17) * mm});
            skLineSegment(sketch, "E1494", {"start": v(440.6, 33809.24) * mm, "end": v(724.8, 32870.3) * mm});
            skLineSegment(sketch, "E1495", {"start": v(724.8, 32870.3) * mm, "end": v(705.65, 32864.5) * mm});
            skLineSegment(sketch, "E1496", {"start": v(705.65, 32864.5) * mm, "end": v(421.45, 33803.44) * mm});
            skLineSegment(sketch, "E1497", {"start": v(421.45, 33803.44) * mm, "end": v(440.6, 33809.24) * mm});
            skLineSegment(sketch, "E1498", {"start": v(810.64, 33867.3) * mm, "end": v(1064.92, 33027.2) * mm});
            skLineSegment(sketch, "E1499", {"start": v(1064.92, 33027.2) * mm, "end": v(794.8, 32945.44) * mm});
            skLineSegment(sketch, "E1500", {"start": v(794.8, 32945.44) * mm, "end": v(540.52, 33785.54) * mm});
            skLineSegment(sketch, "E1501", {"start": v(540.52, 33785.54) * mm, "end": v(810.64, 33867.3) * mm});
            skLineSegment(sketch, "E1502", {"start": v(818.12, 33842.59) * mm, "end": v(1057.56, 33051.52) * mm});
            skLineSegment(sketch, "E1503", {"start": v(1057.56, 33051.52) * mm, "end": v(809.68, 32976.49) * mm});
            skLineSegment(sketch, "E1504", {"start": v(809.68, 32976.49) * mm, "end": v(570.23, 33767.56) * mm});
            skLineSegment(sketch, "E1505", {"start": v(570.23, 33767.56) * mm, "end": v(818.12, 33842.59) * mm});
            skLineSegment(sketch, "E1506", {"start": v(535.14, 33837.85) * mm, "end": v(819.33, 32898.92) * mm});
            skLineSegment(sketch, "E1507", {"start": v(819.33, 32898.92) * mm, "end": v(800.2, 32893.13) * mm});
            skLineSegment(sketch, "E1508", {"start": v(800.2, 32893.13) * mm, "end": v(516, 33832.06) * mm});
            skLineSegment(sketch, "E1509", {"start": v(516, 33832.06) * mm, "end": v(535.14, 33837.85) * mm});
            skLineSegment(sketch, "E1510", {"start": v(874.87, 33886.52) * mm, "end": v(1129.15, 33046.43) * mm});
            skLineSegment(sketch, "E1511", {"start": v(1129.15, 33046.43) * mm, "end": v(859.03, 32964.67) * mm});
            skLineSegment(sketch, "E1512", {"start": v(859.03, 32964.67) * mm, "end": v(604.75, 33804.76) * mm});
            skLineSegment(sketch, "E1513", {"start": v(604.75, 33804.76) * mm, "end": v(874.87, 33886.52) * mm});
            skLineSegment(sketch, "E1514", {"start": v(886.3, 33863) * mm, "end": v(1125.73, 33071.94) * mm});
            skLineSegment(sketch, "E1515", {"start": v(1125.73, 33071.94) * mm, "end": v(875.87, 32996.31) * mm});
            skLineSegment(sketch, "E1516", {"start": v(875.87, 32996.31) * mm, "end": v(636.43, 33787.38) * mm});
            skLineSegment(sketch, "E1517", {"start": v(636.43, 33787.38) * mm, "end": v(886.3, 33863) * mm});
            skLineSegment(sketch, "E1518", {"start": v(599.36, 33857.08) * mm, "end": v(883.56, 32918.15) * mm});
            skLineSegment(sketch, "E1519", {"start": v(883.56, 32918.15) * mm, "end": v(864.41, 32912.35) * mm});
            skLineSegment(sketch, "E1520", {"start": v(864.41, 32912.35) * mm, "end": v(580.22, 33851.28) * mm});
            skLineSegment(sketch, "E1521", {"start": v(580.22, 33851.28) * mm, "end": v(599.36, 33857.08) * mm});
            skLineSegment(sketch, "E1522", {"start": v(969.4, 33915.14) * mm, "end": v(1223.69, 33075.04) * mm});
            skLineSegment(sketch, "E1523", {"start": v(1223.69, 33075.04) * mm, "end": v(953.57, 32993.28) * mm});
            skLineSegment(sketch, "E1524", {"start": v(953.57, 32993.28) * mm, "end": v(699.29, 33833.38) * mm});
            skLineSegment(sketch, "E1525", {"start": v(699.29, 33833.38) * mm, "end": v(969.4, 33915.14) * mm});
            skLineSegment(sketch, "E1526", {"start": v(976.89, 33890.43) * mm, "end": v(1216.33, 33099.36) * mm});
            skLineSegment(sketch, "E1527", {"start": v(1216.33, 33099.36) * mm, "end": v(968.44, 33024.33) * mm});
            skLineSegment(sketch, "E1528", {"start": v(968.44, 33024.33) * mm, "end": v(729, 33815.4) * mm});
            skLineSegment(sketch, "E1529", {"start": v(729, 33815.4) * mm, "end": v(976.89, 33890.43) * mm});
            skLineSegment(sketch, "E1530", {"start": v(693.9, 33885.7) * mm, "end": v(978.1, 32946.76) * mm});
            skLineSegment(sketch, "E1531", {"start": v(978.1, 32946.76) * mm, "end": v(958.96, 32940.97) * mm});
            skLineSegment(sketch, "E1532", {"start": v(958.96, 32940.97) * mm, "end": v(674.76, 33879.9) * mm});
            skLineSegment(sketch, "E1533", {"start": v(674.76, 33879.9) * mm, "end": v(693.9, 33885.7) * mm});
            skLineSegment(sketch, "E1534", {"start": v(1643.09, 33148.04) * mm, "end": v(1650.33, 33124.11) * mm});
            skLineSegment(sketch, "E1535", {"start": v(1650.33, 33124.11) * mm, "end": v(1089.45, 32954.35) * mm});
            skLineSegment(sketch, "E1536", {"start": v(1089.45, 32954.35) * mm, "end": v(1082.21, 32978.27) * mm});
            skLineSegment(sketch, "E1537", {"start": v(1082.21, 32978.27) * mm, "end": v(1643.09, 33148.04) * mm});
            skLineSegment(sketch, "E1538", {"start": v(1351.65, 34110.9) * mm, "end": v(1358.9, 34086.97) * mm});
            skLineSegment(sketch, "E1539", {"start": v(1358.9, 34086.97) * mm, "end": v(798.02, 33917.2) * mm});
            skLineSegment(sketch, "E1540", {"start": v(798.02, 33917.2) * mm, "end": v(790.77, 33941.13) * mm});
            skLineSegment(sketch, "E1541", {"start": v(790.77, 33941.13) * mm, "end": v(1351.65, 34110.9) * mm});
            skLineSegment(sketch, "E1542", {"start": v(752.16, 33450.68) * mm, "end": v(785.18, 33914.73) * mm});
            skLineSegment(sketch, "E1543", {"start": v(785.18, 33914.73) * mm, "end": v(769.72, 33921.7) * mm});
            skLineSegment(sketch, "E1544", {"start": v(769.72, 33921.7) * mm, "end": v(736.7, 33457.65) * mm});
            skLineSegment(sketch, "E1545", {"start": v(736.7, 33457.65) * mm, "end": v(752.16, 33450.68) * mm});
            skLineSegment(sketch, "E1546", {"start": v(784.65, 33343.33) * mm, "end": v(1069.47, 32975.49) * mm});
            skLineSegment(sketch, "E1547", {"start": v(1069.47, 32975.49) * mm, "end": v(1060.47, 32961.11) * mm});
            skLineSegment(sketch, "E1548", {"start": v(1060.47, 32961.11) * mm, "end": v(775.65, 33328.96) * mm});
            skLineSegment(sketch, "E1549", {"start": v(775.65, 33328.96) * mm, "end": v(784.65, 33343.33) * mm});
            skLineSegment(sketch, "E1550", {"start": v(917.16, 33440.74) * mm, "end": v(938.21, 33447.11) * mm});
            skLineSegment(sketch, "E1551", {"start": v(938.21, 33447.11) * mm, "end": v(1083.06, 32968.55) * mm});
            skLineSegment(sketch, "E1552", {"start": v(1083.06, 32968.55) * mm, "end": v(1062, 32962.18) * mm});
            skLineSegment(sketch, "E1553", {"start": v(1062, 32962.18) * mm, "end": v(917.16, 33440.74) * mm});
            skLineSegment(sketch, "E1554", {"start": v(771.42, 33922.22) * mm, "end": v(792.48, 33928.6) * mm});
            skLineSegment(sketch, "E1555", {"start": v(792.48, 33928.6) * mm, "end": v(937.33, 33450.03) * mm});
            skLineSegment(sketch, "E1556", {"start": v(937.33, 33450.03) * mm, "end": v(916.27, 33443.66) * mm});
            skLineSegment(sketch, "E1557", {"start": v(916.27, 33443.66) * mm, "end": v(771.42, 33922.22) * mm});
            skLineSegment(sketch, "E1558", {"start": v(1358.89, 34086.97) * mm, "end": v(1643.08, 33148.04) * mm});
            skLineSegment(sketch, "E1559", {"start": v(1643.08, 33148.04) * mm, "end": v(1082.21, 32978.27) * mm});
            skLineSegment(sketch, "E1560", {"start": v(1082.21, 32978.27) * mm, "end": v(798.02, 33917.2) * mm});
            skLineSegment(sketch, "E1561", {"start": v(798.02, 33917.2) * mm, "end": v(1358.89, 34086.97) * mm});
            skLineSegment(sketch, "E1562", {"start": v(1643.08, 33148.04) * mm, "end": v(798.02, 33917.2) * mm});
            skLineSegment(sketch, "E1563", {"start": v(1358.89, 34086.97) * mm, "end": v(1082.21, 32978.27) * mm});
            skLineSegment(sketch, "E1564", {"start": v(1060.21, 35073.76) * mm, "end": v(1067.46, 35049.83) * mm});
            skLineSegment(sketch, "E1565", {"start": v(1067.46, 35049.83) * mm, "end": v(506.58, 34880.07) * mm});
            skLineSegment(sketch, "E1566", {"start": v(506.58, 34880.07) * mm, "end": v(499.34, 34904) * mm});
            skLineSegment(sketch, "E1567", {"start": v(499.34, 34904) * mm, "end": v(1060.21, 35073.76) * mm});
            skLineSegment(sketch, "E1568", {"start": v(460.72, 34413.54) * mm, "end": v(493.75, 34877.6) * mm});
            skLineSegment(sketch, "E1569", {"start": v(493.75, 34877.6) * mm, "end": v(478.28, 34884.56) * mm});
            skLineSegment(sketch, "E1570", {"start": v(478.28, 34884.56) * mm, "end": v(445.26, 34420.51) * mm});
            skLineSegment(sketch, "E1571", {"start": v(445.26, 34420.51) * mm, "end": v(460.72, 34413.54) * mm});
            skLineSegment(sketch, "E1572", {"start": v(493.21, 34306.2) * mm, "end": v(778.04, 33938.35) * mm});
            skLineSegment(sketch, "E1573", {"start": v(778.04, 33938.35) * mm, "end": v(769.03, 33923.97) * mm});
            skLineSegment(sketch, "E1574", {"start": v(769.03, 33923.97) * mm, "end": v(484.21, 34291.82) * mm});
            skLineSegment(sketch, "E1575", {"start": v(484.21, 34291.82) * mm, "end": v(493.21, 34306.2) * mm});
            skLineSegment(sketch, "E1576", {"start": v(625.72, 34403.6) * mm, "end": v(646.78, 34409.97) * mm});
            skLineSegment(sketch, "E1577", {"start": v(646.78, 34409.97) * mm, "end": v(791.63, 33931.42) * mm});
            skLineSegment(sketch, "E1578", {"start": v(791.63, 33931.42) * mm, "end": v(770.57, 33925.04) * mm});
            skLineSegment(sketch, "E1579", {"start": v(770.57, 33925.04) * mm, "end": v(625.72, 34403.6) * mm});
            skLineSegment(sketch, "E1580", {"start": v(479.99, 34885.08) * mm, "end": v(501.05, 34891.45) * mm});
            skLineSegment(sketch, "E1581", {"start": v(501.05, 34891.45) * mm, "end": v(645.9, 34412.9) * mm});
            skLineSegment(sketch, "E1582", {"start": v(645.9, 34412.9) * mm, "end": v(624.84, 34406.52) * mm});
            skLineSegment(sketch, "E1583", {"start": v(624.84, 34406.52) * mm, "end": v(479.99, 34885.08) * mm});
            skLineSegment(sketch, "E1584", {"start": v(1067.45, 35049.83) * mm, "end": v(1351.65, 34110.9) * mm});
            skLineSegment(sketch, "E1585", {"start": v(1351.65, 34110.9) * mm, "end": v(790.78, 33941.14) * mm});
            skLineSegment(sketch, "E1586", {"start": v(790.78, 33941.14) * mm, "end": v(506.58, 34880.07) * mm});
            skLineSegment(sketch, "E1587", {"start": v(506.58, 34880.07) * mm, "end": v(1067.45, 35049.83) * mm});
            skLineSegment(sketch, "E1588", {"start": v(1351.65, 34110.9) * mm, "end": v(506.58, 34880.07) * mm});
            skLineSegment(sketch, "E1589", {"start": v(1067.45, 35049.83) * mm, "end": v(790.78, 33941.14) * mm});
            skLineSegment(sketch, "E1590", {"start": v(630, 36495.08) * mm, "end": v(768.77, 36036.62) * mm});
            skLineSegment(sketch, "E1591", {"start": v(768.77, 36036.62) * mm, "end": v(207.9, 35866.86) * mm});
            skLineSegment(sketch, "E1592", {"start": v(207.9, 35866.86) * mm, "end": v(69.13, 36325.32) * mm});
            skLineSegment(sketch, "E1593", {"start": v(69.13, 36325.32) * mm, "end": v(630, 36495.08) * mm});
            skLineSegment(sketch, "E1594", {"start": v(768.77, 36036.62) * mm, "end": v(69.13, 36325.32) * mm});
            skLineSegment(sketch, "E1595", {"start": v(630, 36495.08) * mm, "end": v(207.9, 35866.86) * mm});
            skLineSegment(sketch, "E1596", {"start": v(798.02, 33917.2) * mm, "end": v(790.78, 33941.14) * mm});
            skLineSegment(sketch, "E1597", {"start": v(790.78, 33941.14) * mm, "end": v(1351.65, 34110.9) * mm});
            skLineSegment(sketch, "E1598", {"start": v(1062.88, 32959.3) * mm, "end": v(1083.93, 32965.68) * mm});
            skLineSegment(sketch, "E1599", {"start": v(1083.93, 32965.68) * mm, "end": v(1095.08, 32928.84) * mm});
            skLineSegment(sketch, "E1600", {"start": v(1095.08, 32928.84) * mm, "end": v(1074.03, 32922.47) * mm});
            skLineSegment(sketch, "E1601", {"start": v(1074.03, 32922.47) * mm, "end": v(1062.88, 32959.3) * mm});
            skLineSegment(sketch, "E1602", {"start": v(776.01, 36012.7) * mm, "end": v(1060.2, 35073.76) * mm});
            skLineSegment(sketch, "E1603", {"start": v(1060.2, 35073.76) * mm, "end": v(499.34, 34904) * mm});
            skLineSegment(sketch, "E1604", {"start": v(499.34, 34904) * mm, "end": v(215.14, 35842.93) * mm});
            skLineSegment(sketch, "E1605", {"start": v(215.14, 35842.93) * mm, "end": v(776.01, 36012.7) * mm});
            skLineSegment(sketch, "E1606", {"start": v(1060.2, 35073.76) * mm, "end": v(215.14, 35842.93) * mm});
            skLineSegment(sketch, "E1607", {"start": v(776.01, 36012.7) * mm, "end": v(499.34, 34904) * mm});
            skLineSegment(sketch, "E1608", {"start": v(768.78, 36036.62) * mm, "end": v(776.02, 36012.7) * mm});
            skLineSegment(sketch, "E1609", {"start": v(776.02, 36012.7) * mm, "end": v(215.14, 35842.93) * mm});
            skLineSegment(sketch, "E1610", {"start": v(215.14, 35842.93) * mm, "end": v(207.9, 35866.86) * mm});
            skLineSegment(sketch, "E1611", {"start": v(207.9, 35866.86) * mm, "end": v(768.78, 36036.62) * mm});
            skLineSegment(sketch, "E1612", {"start": v(622.77, 36519) * mm, "end": v(630, 36495.08) * mm});
            skLineSegment(sketch, "E1613", {"start": v(630, 36495.08) * mm, "end": v(69.13, 36325.32) * mm});
            skLineSegment(sketch, "E1614", {"start": v(69.13, 36325.32) * mm, "end": v(61.9, 36349.24) * mm});
            skLineSegment(sketch, "E1615", {"start": v(61.9, 36349.24) * mm, "end": v(622.77, 36519) * mm});
            skLineSegment(sketch, "E1616", {"start": v(31.38, 36367.22) * mm, "end": v(52.43, 36373.6) * mm});
            skLineSegment(sketch, "E1617", {"start": v(52.43, 36373.6) * mm, "end": v(63, 36338.66) * mm});
            skLineSegment(sketch, "E1618", {"start": v(63, 36338.66) * mm, "end": v(41.95, 36332.3) * mm});
            skLineSegment(sketch, "E1619", {"start": v(41.95, 36332.3) * mm, "end": v(31.38, 36367.22) * mm});
            skLineSegment(sketch, "E1620", {"start": v(169.27, 35376.45) * mm, "end": v(202.3, 35840.5) * mm});
            skLineSegment(sketch, "E1621", {"start": v(202.3, 35840.5) * mm, "end": v(186.83, 35847.47) * mm});
            skLineSegment(sketch, "E1622", {"start": v(186.83, 35847.47) * mm, "end": v(153.8, 35383.42) * mm});
            skLineSegment(sketch, "E1623", {"start": v(153.8, 35383.42) * mm, "end": v(169.27, 35376.45) * mm});
            skLineSegment(sketch, "E1624", {"start": v(201.76, 35269.1) * mm, "end": v(486.58, 34901.26) * mm});
            skLineSegment(sketch, "E1625", {"start": v(486.58, 34901.26) * mm, "end": v(477.58, 34886.88) * mm});
            skLineSegment(sketch, "E1626", {"start": v(477.58, 34886.88) * mm, "end": v(192.76, 35254.73) * mm});
            skLineSegment(sketch, "E1627", {"start": v(192.76, 35254.73) * mm, "end": v(201.76, 35269.1) * mm});
            skLineSegment(sketch, "E1628", {"start": v(334.27, 35366.5) * mm, "end": v(355.33, 35372.88) * mm});
            skLineSegment(sketch, "E1629", {"start": v(355.33, 35372.88) * mm, "end": v(500.18, 34894.32) * mm});
            skLineSegment(sketch, "E1630", {"start": v(500.18, 34894.32) * mm, "end": v(479.12, 34887.95) * mm});
            skLineSegment(sketch, "E1631", {"start": v(479.12, 34887.95) * mm, "end": v(334.27, 35366.5) * mm});
            skLineSegment(sketch, "E1632", {"start": v(188.54, 35847.99) * mm, "end": v(209.6, 35854.36) * mm});
            skLineSegment(sketch, "E1633", {"start": v(209.6, 35854.36) * mm, "end": v(354.44, 35375.8) * mm});
            skLineSegment(sketch, "E1634", {"start": v(354.44, 35375.8) * mm, "end": v(333.39, 35369.43) * mm});
            skLineSegment(sketch, "E1635", {"start": v(333.39, 35369.43) * mm, "end": v(188.54, 35847.99) * mm});
            skLineSegment(sketch, "E1636", {"start": v(23.55, 35857.88) * mm, "end": v(56.58, 36321.93) * mm});
            skLineSegment(sketch, "E1637", {"start": v(56.58, 36321.93) * mm, "end": v(41.11, 36328.9) * mm});
            skLineSegment(sketch, "E1638", {"start": v(41.11, 36328.9) * mm, "end": v(8.09, 35864.85) * mm});
            skLineSegment(sketch, "E1639", {"start": v(8.09, 35864.85) * mm, "end": v(23.55, 35857.88) * mm});
            skLineSegment(sketch, "E1640", {"start": v(42.82, 36329.42) * mm, "end": v(63.87, 36335.8) * mm});
            skLineSegment(sketch, "E1641", {"start": v(63.87, 36335.8) * mm, "end": v(208.72, 35857.23) * mm});
            skLineSegment(sketch, "E1642", {"start": v(208.72, 35857.23) * mm, "end": v(187.67, 35850.86) * mm});
            skLineSegment(sketch, "E1643", {"start": v(187.67, 35850.86) * mm, "end": v(42.82, 36329.42) * mm});
            skLineSegment(sketch, "E1644", {"start": v(4780.4, 34909.38) * mm, "end": v(5193.87, 35034.53) * mm});
            skLineSegment(sketch, "E1645", {"start": v(5193.87, 35034.53) * mm, "end": v(5363.64, 34473.66) * mm});
            skLineSegment(sketch, "E1646", {"start": v(5363.64, 34473.66) * mm, "end": v(4950.17, 34348.5) * mm});
            skLineSegment(sketch, "E1647", {"start": v(4950.17, 34348.5) * mm, "end": v(4780.4, 34909.38) * mm});
            skLineSegment(sketch, "E1648", {"start": v(2815.1, 34640.25) * mm, "end": v(3655.2, 34894.53) * mm});
            skLineSegment(sketch, "E1649", {"start": v(3655.2, 34894.53) * mm, "end": v(3736.97, 34624.41) * mm});
            skLineSegment(sketch, "E1650", {"start": v(3736.97, 34624.41) * mm, "end": v(2896.87, 34370.13) * mm});
            skLineSegment(sketch, "E1651", {"start": v(2896.87, 34370.13) * mm, "end": v(2815.1, 34640.25) * mm});
            skLineSegment(sketch, "E1652", {"start": v(2846.75, 34623.4) * mm, "end": v(3637.82, 34862.85) * mm});
            skLineSegment(sketch, "E1653", {"start": v(3637.82, 34862.85) * mm, "end": v(3713.45, 34612.99) * mm});
            skLineSegment(sketch, "E1654", {"start": v(3713.45, 34612.99) * mm, "end": v(2922.38, 34373.54) * mm});
            skLineSegment(sketch, "E1655", {"start": v(2922.38, 34373.54) * mm, "end": v(2846.75, 34623.4) * mm});
            skLineSegment(sketch, "E1656", {"start": v(2762.8, 34634.86) * mm, "end": v(3701.72, 34919.06) * mm});
            skLineSegment(sketch, "E1657", {"start": v(3701.72, 34919.06) * mm, "end": v(3707.52, 34899.92) * mm});
            skLineSegment(sketch, "E1658", {"start": v(3707.52, 34899.92) * mm, "end": v(2768.59, 34615.72) * mm});
            skLineSegment(sketch, "E1659", {"start": v(2768.59, 34615.72) * mm, "end": v(2762.8, 34634.86) * mm});
            skLineSegment(sketch, "E1660", {"start": v(2843.72, 34545.7) * mm, "end": v(3683.82, 34800) * mm});
            skLineSegment(sketch, "E1661", {"start": v(3683.82, 34800) * mm, "end": v(3765.58, 34529.87) * mm});
            skLineSegment(sketch, "E1662", {"start": v(3765.58, 34529.87) * mm, "end": v(2925.49, 34275.59) * mm});
            skLineSegment(sketch, "E1663", {"start": v(2925.49, 34275.59) * mm, "end": v(2843.72, 34545.7) * mm});
            skLineSegment(sketch, "E1664", {"start": v(2874.77, 34530.83) * mm, "end": v(3665.84, 34770.28) * mm});
            skLineSegment(sketch, "E1665", {"start": v(3665.84, 34770.28) * mm, "end": v(3740.87, 34522.4) * mm});
            skLineSegment(sketch, "E1666", {"start": v(3740.87, 34522.4) * mm, "end": v(2949.8, 34282.95) * mm});
            skLineSegment(sketch, "E1667", {"start": v(2949.8, 34282.95) * mm, "end": v(2874.77, 34530.83) * mm});
            skLineSegment(sketch, "E1668", {"start": v(2791.41, 34540.32) * mm, "end": v(3730.34, 34824.52) * mm});
            skLineSegment(sketch, "E1669", {"start": v(3730.34, 34824.52) * mm, "end": v(3736.13, 34805.38) * mm});
            skLineSegment(sketch, "E1670", {"start": v(3736.13, 34805.38) * mm, "end": v(2797.2, 34521.18) * mm});
            skLineSegment(sketch, "E1671", {"start": v(2797.2, 34521.18) * mm, "end": v(2791.41, 34540.32) * mm});
            skLineSegment(sketch, "E1672", {"start": v(2830.76, 34319.24) * mm, "end": v(2854.68, 34326.49) * mm});
            skLineSegment(sketch, "E1673", {"start": v(2854.68, 34326.49) * mm, "end": v(3024.45, 33765.61) * mm});
            skLineSegment(sketch, "E1674", {"start": v(3024.45, 33765.61) * mm, "end": v(3000.52, 33758.37) * mm});
            skLineSegment(sketch, "E1675", {"start": v(3000.52, 33758.37) * mm, "end": v(2830.76, 34319.24) * mm});
            skLineSegment(sketch, "E1676", {"start": v(3793.61, 34610.69) * mm, "end": v(3817.54, 34617.93) * mm});
            skLineSegment(sketch, "E1677", {"start": v(3817.54, 34617.93) * mm, "end": v(3987.31, 34057.06) * mm});
            skLineSegment(sketch, "E1678", {"start": v(3987.31, 34057.06) * mm, "end": v(3963.38, 34049.82) * mm});
            skLineSegment(sketch, "E1679", {"start": v(3963.38, 34049.82) * mm, "end": v(3793.61, 34610.69) * mm});
            skLineSegment(sketch, "E1680", {"start": v(3327.09, 34656.54) * mm, "end": v(3791.14, 34623.52) * mm});
            skLineSegment(sketch, "E1681", {"start": v(3791.14, 34623.52) * mm, "end": v(3798.1, 34638.99) * mm});
            skLineSegment(sketch, "E1682", {"start": v(3798.1, 34638.99) * mm, "end": v(3334.06, 34672) * mm});
            skLineSegment(sketch, "E1683", {"start": v(3334.06, 34672) * mm, "end": v(3327.09, 34656.54) * mm});
            skLineSegment(sketch, "E1684", {"start": v(3219.74, 34624.05) * mm, "end": v(2851.9, 34339.23) * mm});
            skLineSegment(sketch, "E1685", {"start": v(2851.9, 34339.23) * mm, "end": v(2837.52, 34348.23) * mm});
            skLineSegment(sketch, "E1686", {"start": v(2837.52, 34348.23) * mm, "end": v(3205.36, 34633.06) * mm});
            skLineSegment(sketch, "E1687", {"start": v(3205.36, 34633.06) * mm, "end": v(3219.74, 34624.05) * mm});
            skLineSegment(sketch, "E1688", {"start": v(3317.15, 34491.54) * mm, "end": v(3323.52, 34470.49) * mm});
            skLineSegment(sketch, "E1689", {"start": v(3323.52, 34470.49) * mm, "end": v(2844.96, 34325.63) * mm});
            skLineSegment(sketch, "E1690", {"start": v(2844.96, 34325.63) * mm, "end": v(2838.59, 34346.7) * mm});
            skLineSegment(sketch, "E1691", {"start": v(2838.59, 34346.7) * mm, "end": v(3317.15, 34491.54) * mm});
            skLineSegment(sketch, "E1692", {"start": v(3798.62, 34637.28) * mm, "end": v(3805, 34616.22) * mm});
            skLineSegment(sketch, "E1693", {"start": v(3805, 34616.22) * mm, "end": v(3326.44, 34471.37) * mm});
            skLineSegment(sketch, "E1694", {"start": v(3326.44, 34471.37) * mm, "end": v(3320.07, 34492.43) * mm});
            skLineSegment(sketch, "E1695", {"start": v(3320.07, 34492.43) * mm, "end": v(3798.62, 34637.28) * mm});
            skLineSegment(sketch, "E1696", {"start": v(2854.68, 34326.49) * mm, "end": v(3793.61, 34610.69) * mm});
            skLineSegment(sketch, "E1697", {"start": v(3793.61, 34610.69) * mm, "end": v(3963.38, 34049.82) * mm});
            skLineSegment(sketch, "E1698", {"start": v(3963.38, 34049.82) * mm, "end": v(3024.45, 33765.62) * mm});
            skLineSegment(sketch, "E1699", {"start": v(3024.45, 33765.62) * mm, "end": v(2854.68, 34326.49) * mm});
            skLineSegment(sketch, "E1700", {"start": v(3024.45, 33765.62) * mm, "end": v(3793.61, 34610.69) * mm});
            skLineSegment(sketch, "E1701", {"start": v(3963.38, 34049.82) * mm, "end": v(2854.68, 34326.49) * mm});
            skLineSegment(sketch, "E1702", {"start": v(4756.47, 34902.13) * mm, "end": v(4780.4, 34909.38) * mm});
            skLineSegment(sketch, "E1703", {"start": v(4780.4, 34909.38) * mm, "end": v(4950.17, 34348.5) * mm});
            skLineSegment(sketch, "E1704", {"start": v(4950.17, 34348.5) * mm, "end": v(4926.24, 34341.26) * mm});
            skLineSegment(sketch, "E1705", {"start": v(4926.24, 34341.26) * mm, "end": v(4756.47, 34902.13) * mm});
            skLineSegment(sketch, "E1706", {"start": v(4289.94, 34947.99) * mm, "end": v(4754, 34914.97) * mm});
            skLineSegment(sketch, "E1707", {"start": v(4754, 34914.97) * mm, "end": v(4760.97, 34930.43) * mm});
            skLineSegment(sketch, "E1708", {"start": v(4760.97, 34930.43) * mm, "end": v(4296.91, 34963.45) * mm});
            skLineSegment(sketch, "E1709", {"start": v(4296.91, 34963.45) * mm, "end": v(4289.94, 34947.99) * mm});
            skLineSegment(sketch, "E1710", {"start": v(4182.6, 34915.5) * mm, "end": v(3814.75, 34630.67) * mm});
            skLineSegment(sketch, "E1711", {"start": v(3814.75, 34630.67) * mm, "end": v(3800.38, 34639.67) * mm});
            skLineSegment(sketch, "E1712", {"start": v(3800.38, 34639.67) * mm, "end": v(4168.22, 34924.5) * mm});
            skLineSegment(sketch, "E1713", {"start": v(4168.22, 34924.5) * mm, "end": v(4182.6, 34915.5) * mm});
            skLineSegment(sketch, "E1714", {"start": v(4280, 34782.99) * mm, "end": v(4286.38, 34761.93) * mm});
            skLineSegment(sketch, "E1715", {"start": v(4286.38, 34761.93) * mm, "end": v(3807.82, 34617.08) * mm});
            skLineSegment(sketch, "E1716", {"start": v(3807.82, 34617.08) * mm, "end": v(3801.45, 34638.14) * mm});
            skLineSegment(sketch, "E1717", {"start": v(3801.45, 34638.14) * mm, "end": v(4280, 34782.99) * mm});
            skLineSegment(sketch, "E1718", {"start": v(4761.48, 34928.73) * mm, "end": v(4767.86, 34907.67) * mm});
            skLineSegment(sketch, "E1719", {"start": v(4767.86, 34907.67) * mm, "end": v(4289.3, 34762.82) * mm});
            skLineSegment(sketch, "E1720", {"start": v(4289.3, 34762.82) * mm, "end": v(4282.92, 34783.87) * mm});
            skLineSegment(sketch, "E1721", {"start": v(4282.92, 34783.87) * mm, "end": v(4761.48, 34928.73) * mm});
            skLineSegment(sketch, "E1722", {"start": v(3817.54, 34617.93) * mm, "end": v(4756.47, 34902.13) * mm});
            skLineSegment(sketch, "E1723", {"start": v(4756.47, 34902.13) * mm, "end": v(4926.24, 34341.26) * mm});
            skLineSegment(sketch, "E1724", {"start": v(4926.24, 34341.26) * mm, "end": v(3987.3, 34057.06) * mm});
            skLineSegment(sketch, "E1725", {"start": v(3987.3, 34057.06) * mm, "end": v(3817.54, 34617.93) * mm});
            skLineSegment(sketch, "E1726", {"start": v(3987.3, 34057.06) * mm, "end": v(4756.47, 34902.13) * mm});
            skLineSegment(sketch, "E1727", {"start": v(4926.24, 34341.26) * mm, "end": v(3817.54, 34617.93) * mm});
            skLineSegment(sketch, "E1728", {"start": v(5193.87, 35034.53) * mm, "end": v(5217.8, 35041.77) * mm});
            skLineSegment(sketch, "E1729", {"start": v(5217.8, 35041.77) * mm, "end": v(5387.57, 34480.9) * mm});
            skLineSegment(sketch, "E1730", {"start": v(5387.57, 34480.9) * mm, "end": v(5363.64, 34473.66) * mm});
            skLineSegment(sketch, "E1731", {"start": v(5363.64, 34473.66) * mm, "end": v(5193.87, 35034.53) * mm});
            skLineSegment(sketch, "E1732", {"start": v(4764.22, 35092.48) * mm, "end": v(5191.97, 35048.84) * mm});
            skLineSegment(sketch, "E1733", {"start": v(5191.97, 35048.84) * mm, "end": v(5198.02, 35064) * mm});
            skLineSegment(sketch, "E1734", {"start": v(5198.02, 35064) * mm, "end": v(4770.27, 35107.64) * mm});
            skLineSegment(sketch, "E1735", {"start": v(4770.27, 35107.64) * mm, "end": v(4764.22, 35092.48) * mm});
            skLineSegment(sketch, "E1736", {"start": v(5198.88, 35061.12) * mm, "end": v(5205.26, 35040.07) * mm});
            skLineSegment(sketch, "E1737", {"start": v(5205.26, 35040.07) * mm, "end": v(4766.93, 34907.39) * mm});
            skLineSegment(sketch, "E1738", {"start": v(4766.93, 34907.39) * mm, "end": v(4760.56, 34928.45) * mm});
            skLineSegment(sketch, "E1739", {"start": v(4760.56, 34928.45) * mm, "end": v(5198.88, 35061.12) * mm});
            skLineSegment(sketch, "E1740", {"start": v(4950.17, 34348.5) * mm, "end": v(5191.25, 35033.75) * mm});
            skLineSegment(sketch, "E1741", {"start": v(5363.64, 34473.66) * mm, "end": v(4780.4, 34909.4) * mm});
            skLineSegment(sketch, "E1742", {"start": v(2805.77, 34313.77) * mm, "end": v(2799.4, 34334.83) * mm});
            skLineSegment(sketch, "E1743", {"start": v(2799.4, 34334.83) * mm, "end": v(2835.72, 34345.82) * mm});
            skLineSegment(sketch, "E1744", {"start": v(2835.72, 34345.82) * mm, "end": v(2842.1, 34324.77) * mm});
            skLineSegment(sketch, "E1745", {"start": v(2842.1, 34324.77) * mm, "end": v(2805.77, 34313.77) * mm});
            skLineSegment(sketch, "E1746", {"start": v(5208.18, 35040.95) * mm, "end": v(5201.8, 35062) * mm});
            skLineSegment(sketch, "E1747", {"start": v(5201.8, 35062) * mm, "end": v(5235.25, 35072.13) * mm});
            skLineSegment(sketch, "E1748", {"start": v(5235.25, 35072.13) * mm, "end": v(5241.63, 35051.07) * mm});
            skLineSegment(sketch, "E1749", {"start": v(5241.63, 35051.07) * mm, "end": v(5208.18, 35040.95) * mm});
            skLineSegment(sketch, "E1750", {"start": v(6924.09, 26007.02) * mm, "end": v(6750.27, 26581.29) * mm});
            skLineSegment(sketch, "E1751", {"start": v(6750.27, 26581.29) * mm, "end": v(7094.6, 26685.5) * mm});
            skLineSegment(sketch, "E1752", {"start": v(7094.6, 26685.5) * mm, "end": v(7268.41, 26111.24) * mm});
            skLineSegment(sketch, "E1753", {"start": v(7268.41, 26111.24) * mm, "end": v(6924.09, 26007.02) * mm});
            skLineSegment(sketch, "E1754", {"start": v(7268.41, 26111.24) * mm, "end": v(7094.6, 26685.5) * mm});
            skLineSegment(sketch, "E1755", {"start": v(7094.6, 26685.5) * mm, "end": v(7668.86, 26859.33) * mm});
            skLineSegment(sketch, "E1756", {"start": v(7668.86, 26859.33) * mm, "end": v(7842.68, 26285.06) * mm});
            skLineSegment(sketch, "E1757", {"start": v(7842.68, 26285.06) * mm, "end": v(7268.41, 26111.24) * mm});
            skLineSegment(sketch, "E1758", {"start": v(6855.98, 26655.48) * mm, "end": v(6706.41, 27149.62) * mm});
            skLineSegment(sketch, "E1759", {"start": v(6706.41, 27149.62) * mm, "end": v(6956.27, 27225.25) * mm});
            skLineSegment(sketch, "E1760", {"start": v(6956.27, 27225.25) * mm, "end": v(7105.84, 26731.11) * mm});
            skLineSegment(sketch, "E1761", {"start": v(7105.84, 26731.11) * mm, "end": v(6855.98, 26655.48) * mm});
            skArc(sketch, "E1762", {"start": v(6871.7, 26682.1) * mm, "mid": v(6859.74, 26683.3) * mm, "end": v(6852.12, 26692.58) * mm});
            skLineSegment(sketch, "E1763", {"start": v(6852.12, 26692.58) * mm, "end": v(6723.78, 27116.6) * mm});
            skArc(sketch, "E1764", {"start": v(6723.78, 27116.6) * mm, "mid": v(6724.96, 27128.57) * mm, "end": v(6734.25, 27136.18) * mm});
            skLineSegment(sketch, "E1765", {"start": v(6734.25, 27136.18) * mm, "end": v(6947.31, 27200.67) * mm});
            skArc(sketch, "E1766", {"start": v(6947.31, 27200.67) * mm, "mid": v(6959.27, 27199.49) * mm, "end": v(6966.88, 27190.2) * mm});
            skLineSegment(sketch, "E1767", {"start": v(6966.88, 27190.2) * mm, "end": v(7095.23, 26766.17) * mm});
            skArc(sketch, "E1768", {"start": v(7095.23, 26766.17) * mm, "mid": v(7094.04, 26754.21) * mm, "end": v(7084.75, 26746.6) * mm});
            skLineSegment(sketch, "E1769", {"start": v(7084.75, 26746.6) * mm, "end": v(6871.7, 26682.1) * mm});
            skLineSegment(sketch, "E1770", {"start": v(6852.76, 26666.12) * mm, "end": v(6849.9, 26675.59) * mm});
            skLineSegment(sketch, "E1771", {"start": v(6849.9, 26675.59) * mm, "end": v(7093, 26749.17) * mm});
            skLineSegment(sketch, "E1772", {"start": v(7093, 26749.17) * mm, "end": v(7095.86, 26739.7) * mm});
            skLineSegment(sketch, "E1773", {"start": v(7095.86, 26739.7) * mm, "end": v(6852.76, 26666.12) * mm});
            skLineSegment(sketch, "E1774", {"start": v(6712.32, 27130.1) * mm, "end": v(6709.45, 27139.57) * mm});
            skLineSegment(sketch, "E1775", {"start": v(6709.45, 27139.57) * mm, "end": v(6952.56, 27213.16) * mm});
            skLineSegment(sketch, "E1776", {"start": v(6952.56, 27213.16) * mm, "end": v(6955.43, 27203.7) * mm});
            skLineSegment(sketch, "E1777", {"start": v(6955.43, 27203.7) * mm, "end": v(6712.32, 27130.1) * mm});
            skArc(sketch, "E1778", {"start": v(6874.13, 26690.2) * mm, "mid": v(6862.17, 26691.4) * mm, "end": v(6854.55, 26700.69) * mm});
            skLineSegment(sketch, "E1779", {"start": v(6854.55, 26700.69) * mm, "end": v(6798.97, 26884.32) * mm});
            skArc(sketch, "E1780", {"start": v(6798.97, 26884.32) * mm, "mid": v(6800.16, 26896.28) * mm, "end": v(6809.45, 26903.9) * mm});
            skLineSegment(sketch, "E1781", {"start": v(6809.45, 26903.9) * mm, "end": v(7015.76, 26966.34) * mm});
            skArc(sketch, "E1782", {"start": v(7015.76, 26966.34) * mm, "mid": v(7027.71, 26965.15) * mm, "end": v(7035.33, 26955.86) * mm});
            skLineSegment(sketch, "E1783", {"start": v(7035.33, 26955.86) * mm, "end": v(7090.9, 26772.23) * mm});
            skArc(sketch, "E1784", {"start": v(7090.9, 26772.23) * mm, "mid": v(7089.72, 26760.27) * mm, "end": v(7080.43, 26752.65) * mm});
            skLineSegment(sketch, "E1785", {"start": v(7080.43, 26752.65) * mm, "end": v(6874.13, 26690.2) * mm});
            skArc(sketch, "E1786", {"start": v(6878.93, 26698.95) * mm, "mid": v(6866.97, 26700.14) * mm, "end": v(6859.36, 26709.43) * mm});
            skLineSegment(sketch, "E1787", {"start": v(6859.36, 26709.43) * mm, "end": v(6807.82, 26879.7) * mm});
            skArc(sketch, "E1788", {"start": v(6807.82, 26879.7) * mm, "mid": v(6809, 26891.66) * mm, "end": v(6818.3, 26899.28) * mm});
            skLineSegment(sketch, "E1789", {"start": v(6818.3, 26899.28) * mm, "end": v(7011.1, 26957.64) * mm});
            skArc(sketch, "E1790", {"start": v(7011.1, 26957.64) * mm, "mid": v(7023.05, 26956.45) * mm, "end": v(7030.67, 26947.16) * mm});
            skLineSegment(sketch, "E1791", {"start": v(7030.67, 26947.16) * mm, "end": v(7082.2, 26776.88) * mm});
            skArc(sketch, "E1792", {"start": v(7082.2, 26776.88) * mm, "mid": v(7081.02, 26764.93) * mm, "end": v(7071.73, 26757.3) * mm});
            skLineSegment(sketch, "E1793", {"start": v(7071.73, 26757.3) * mm, "end": v(6878.93, 26698.95) * mm});
            skLineSegment(sketch, "E1794", {"start": v(6831.61, 26874.15) * mm, "end": v(6878.1, 26720.57) * mm});
            skLineSegment(sketch, "E1795", {"start": v(6878.1, 26720.57) * mm, "end": v(6891.6, 26724.66) * mm});
            skLineSegment(sketch, "E1796", {"start": v(6891.6, 26724.66) * mm, "end": v(6851.18, 26858.2) * mm});
            skLineSegment(sketch, "E1797", {"start": v(6851.18, 26858.2) * mm, "end": v(7013.25, 26907.27) * mm});
            skLineSegment(sketch, "E1798", {"start": v(7013.25, 26907.27) * mm, "end": v(7007.2, 26927.3) * mm});
            skLineSegment(sketch, "E1799", {"start": v(7007.2, 26927.3) * mm, "end": v(6831.61, 26874.15) * mm});
            skArc(sketch, "E1800", {"start": v(6806.41, 26915.6) * mm, "mid": v(6794.46, 26916.78) * mm, "end": v(6786.84, 26926.07) * mm});
            skLineSegment(sketch, "E1801", {"start": v(6786.84, 26926.07) * mm, "end": v(6731.26, 27109.7) * mm});
            skArc(sketch, "E1802", {"start": v(6731.26, 27109.7) * mm, "mid": v(6732.44, 27121.66) * mm, "end": v(6741.74, 27129.28) * mm});
            skLineSegment(sketch, "E1803", {"start": v(6741.74, 27129.28) * mm, "end": v(6948.04, 27191.72) * mm});
            skArc(sketch, "E1804", {"start": v(6948.04, 27191.72) * mm, "mid": v(6960, 27190.54) * mm, "end": v(6967.61, 27181.25) * mm});
            skLineSegment(sketch, "E1805", {"start": v(6967.61, 27181.25) * mm, "end": v(7023.2, 26997.61) * mm});
            skArc(sketch, "E1806", {"start": v(7023.2, 26997.61) * mm, "mid": v(7022.01, 26985.66) * mm, "end": v(7012.72, 26978.04) * mm});
            skLineSegment(sketch, "E1807", {"start": v(7012.72, 26978.04) * mm, "end": v(6806.41, 26915.6) * mm});
            skArc(sketch, "E1808", {"start": v(6811.22, 26924.34) * mm, "mid": v(6799.26, 26925.52) * mm, "end": v(6791.64, 26934.82) * mm});
            skLineSegment(sketch, "E1809", {"start": v(6791.64, 26934.82) * mm, "end": v(6740.1, 27105.1) * mm});
            skArc(sketch, "E1810", {"start": v(6740.1, 27105.1) * mm, "mid": v(6741.29, 27117.05) * mm, "end": v(6750.58, 27124.67) * mm});
            skLineSegment(sketch, "E1811", {"start": v(6750.58, 27124.67) * mm, "end": v(6943.38, 27183.02) * mm});
            skArc(sketch, "E1812", {"start": v(6943.38, 27183.02) * mm, "mid": v(6955.34, 27181.84) * mm, "end": v(6962.95, 27172.55) * mm});
            skLineSegment(sketch, "E1813", {"start": v(6962.95, 27172.55) * mm, "end": v(7014.5, 27002.27) * mm});
            skArc(sketch, "E1814", {"start": v(7014.5, 27002.27) * mm, "mid": v(7013.3, 26990.31) * mm, "end": v(7004.01, 26982.7) * mm});
            skLineSegment(sketch, "E1815", {"start": v(7004.01, 26982.7) * mm, "end": v(6811.22, 26924.34) * mm});
            skLineSegment(sketch, "E1816", {"start": v(6763.9, 27099.54) * mm, "end": v(6810.39, 26945.96) * mm});
            skLineSegment(sketch, "E1817", {"start": v(6810.39, 26945.96) * mm, "end": v(6823.9, 26950.04) * mm});
            skLineSegment(sketch, "E1818", {"start": v(6823.9, 26950.04) * mm, "end": v(6783.47, 27083.6) * mm});
            skLineSegment(sketch, "E1819", {"start": v(6783.47, 27083.6) * mm, "end": v(6945.54, 27132.65) * mm});
            skLineSegment(sketch, "E1820", {"start": v(6945.54, 27132.65) * mm, "end": v(6939.48, 27152.68) * mm});
            skLineSegment(sketch, "E1821", {"start": v(6939.48, 27152.68) * mm, "end": v(6763.9, 27099.54) * mm});
            skLineSegment(sketch, "E1822", {"start": v(6849.65, 26609.83) * mm, "end": v(6675.83, 27184.1) * mm});
            skLineSegment(sketch, "E1823", {"start": v(6675.83, 27184.1) * mm, "end": v(6694.97, 27189.9) * mm});
            skLineSegment(sketch, "E1824", {"start": v(6694.97, 27189.9) * mm, "end": v(6868.79, 26615.62) * mm});
            skLineSegment(sketch, "E1825", {"start": v(6868.79, 26615.62) * mm, "end": v(6849.65, 26609.83) * mm});
            skLineSegment(sketch, "E1826", {"start": v(7316.67, 25538.47) * mm, "end": v(7167.47, 26031.38) * mm});
            skLineSegment(sketch, "E1827", {"start": v(7167.47, 26031.38) * mm, "end": v(7437.6, 26113.14) * mm});
            skLineSegment(sketch, "E1828", {"start": v(7437.6, 26113.14) * mm, "end": v(7586.79, 25620.23) * mm});
            skLineSegment(sketch, "E1829", {"start": v(7586.79, 25620.23) * mm, "end": v(7316.67, 25538.47) * mm});
            skLineSegment(sketch, "E1830", {"start": v(7332.31, 25559.85) * mm, "end": v(7193.25, 26019.27) * mm});
            skLineSegment(sketch, "E1831", {"start": v(7193.25, 26019.27) * mm, "end": v(7443.12, 26094.9) * mm});
            skLineSegment(sketch, "E1832", {"start": v(7443.12, 26094.9) * mm, "end": v(7582.17, 25635.48) * mm});
            skLineSegment(sketch, "E1833", {"start": v(7582.17, 25635.48) * mm, "end": v(7332.31, 25559.85) * mm});
            skLineSegment(sketch, "E1834", {"start": v(7314.12, 25498.19) * mm, "end": v(7140.3, 26072.46) * mm});
            skLineSegment(sketch, "E1835", {"start": v(7140.3, 26072.46) * mm, "end": v(7159.44, 26078.25) * mm});
            skLineSegment(sketch, "E1836", {"start": v(7159.44, 26078.25) * mm, "end": v(7333.26, 25503.98) * mm});
            skLineSegment(sketch, "E1837", {"start": v(7333.26, 25503.98) * mm, "end": v(7314.12, 25498.19) * mm});
            skLineSegment(sketch, "E1838", {"start": v(7490.49, 24964.2) * mm, "end": v(7341.3, 25457.11) * mm});
            skLineSegment(sketch, "E1839", {"start": v(7341.3, 25457.11) * mm, "end": v(7611.41, 25538.87) * mm});
            skLineSegment(sketch, "E1840", {"start": v(7611.41, 25538.87) * mm, "end": v(7760.6, 25045.96) * mm});
            skLineSegment(sketch, "E1841", {"start": v(7760.6, 25045.96) * mm, "end": v(7490.49, 24964.2) * mm});
            skLineSegment(sketch, "E1842", {"start": v(7506.13, 24985.58) * mm, "end": v(7367.07, 25445) * mm});
            skLineSegment(sketch, "E1843", {"start": v(7367.07, 25445) * mm, "end": v(7616.94, 25520.63) * mm});
            skLineSegment(sketch, "E1844", {"start": v(7616.94, 25520.63) * mm, "end": v(7756, 25061.21) * mm});
            skLineSegment(sketch, "E1845", {"start": v(7756, 25061.21) * mm, "end": v(7506.13, 24985.58) * mm});
            skLineSegment(sketch, "E1846", {"start": v(7487.94, 24923.92) * mm, "end": v(7314.12, 25498.19) * mm});
            skLineSegment(sketch, "E1847", {"start": v(7314.12, 25498.19) * mm, "end": v(7333.26, 25503.98) * mm});
            skLineSegment(sketch, "E1848", {"start": v(7333.26, 25503.98) * mm, "end": v(7507.08, 24929.71) * mm});
            skLineSegment(sketch, "E1849", {"start": v(7507.08, 24929.71) * mm, "end": v(7487.94, 24923.92) * mm});
            skLineSegment(sketch, "E1850", {"start": v(7624.74, 24933.98) * mm, "end": v(6920.77, 27259.78) * mm});
            skLineSegment(sketch, "E1851", {"start": v(6920.77, 27259.78) * mm, "end": v(7542.9, 27448.08) * mm});
            skLineSegment(sketch, "E1852", {"start": v(7542.9, 27448.08) * mm, "end": v(8246.87, 25122.29) * mm});
            skLineSegment(sketch, "E1853", {"start": v(8246.87, 25122.29) * mm, "end": v(7624.74, 24933.98) * mm});
            skLineSegment(sketch, "E1854", {"start": v(7113.74, 26691.3) * mm, "end": v(6939.92, 27265.57) * mm});
            skLineSegment(sketch, "E1855", {"start": v(6939.92, 27265.57) * mm, "end": v(7514.19, 27439.4) * mm});
            skLineSegment(sketch, "E1856", {"start": v(7514.19, 27439.4) * mm, "end": v(7688, 26865.12) * mm});
            skLineSegment(sketch, "E1857", {"start": v(7688, 26865.12) * mm, "end": v(7113.74, 26691.3) * mm});
            skLineSegment(sketch, "E1858", {"start": v(7616.05, 24962.7) * mm, "end": v(6920.77, 27259.78) * mm});
            skLineSegment(sketch, "E1859", {"start": v(6920.77, 27259.78) * mm, "end": v(6939.92, 27265.57) * mm});
            skLineSegment(sketch, "E1860", {"start": v(6939.92, 27265.57) * mm, "end": v(7635.2, 24968.49) * mm});
            skLineSegment(sketch, "E1861", {"start": v(7635.2, 24968.49) * mm, "end": v(7616.05, 24962.7) * mm});
            skLineSegment(sketch, "E1862", {"start": v(8208.59, 25110.7) * mm, "end": v(7504.61, 27436.5) * mm});
            skLineSegment(sketch, "E1863", {"start": v(7504.61, 27436.5) * mm, "end": v(7523.76, 27442.29) * mm});
            skLineSegment(sketch, "E1864", {"start": v(7523.76, 27442.29) * mm, "end": v(8227.73, 25116.5) * mm});
            skLineSegment(sketch, "E1865", {"start": v(8227.73, 25116.5) * mm, "end": v(8208.59, 25110.7) * mm});
            skLineSegment(sketch, "E1866", {"start": v(7450.11, 25673.57) * mm, "end": v(7340.03, 26037.28) * mm});
            skLineSegment(sketch, "E1867", {"start": v(7340.03, 26037.28) * mm, "end": v(7847.3, 26190.82) * mm});
            skLineSegment(sketch, "E1868", {"start": v(7847.3, 26190.82) * mm, "end": v(7957.38, 25827.11) * mm});
            skLineSegment(sketch, "E1869", {"start": v(7957.38, 25827.11) * mm, "end": v(7450.11, 25673.57) * mm});
            skLineSegment(sketch, "E1870", {"start": v(7681.7, 25790.4) * mm, "end": v(7596.08, 26073.27) * mm});
            skLineSegment(sketch, "E1871", {"start": v(7596.08, 26073.27) * mm, "end": v(7816.22, 26139.9) * mm});
            skLineSegment(sketch, "E1872", {"start": v(7816.22, 26139.9) * mm, "end": v(7901.84, 25857.02) * mm});
            skLineSegment(sketch, "E1873", {"start": v(7901.84, 25857.02) * mm, "end": v(7681.7, 25790.4) * mm});
            skLineSegment(sketch, "E1874", {"start": v(7782.43, 25826.93) * mm, "end": v(7752.01, 25927.42) * mm});
            skLineSegment(sketch, "E1875", {"start": v(7731.55, 26000.74) * mm, "end": v(7701.13, 26101.24) * mm});
            skLineSegment(sketch, "E1876", {"start": v(7456.1, 25791.38) * mm, "end": v(7389.47, 26011.52) * mm});
            skLineSegment(sketch, "E1877", {"start": v(7389.47, 26011.52) * mm, "end": v(7592.38, 26072.94) * mm});
            skLineSegment(sketch, "E1878", {"start": v(7592.38, 26072.94) * mm, "end": v(7659.01, 25852.8) * mm});
            skLineSegment(sketch, "E1879", {"start": v(7659.01, 25852.8) * mm, "end": v(7456.1, 25791.38) * mm});
            skLineSegment(sketch, "E1880", {"start": v(7477.18, 25710.32) * mm, "end": v(7456.8, 25777.67) * mm});
            skLineSegment(sketch, "E1881", {"start": v(7456.8, 25777.67) * mm, "end": v(7646.17, 25835) * mm});
            skLineSegment(sketch, "E1882", {"start": v(7646.17, 25835) * mm, "end": v(7666.56, 25767.64) * mm});
            skLineSegment(sketch, "E1883", {"start": v(7666.56, 25767.64) * mm, "end": v(7477.18, 25710.32) * mm});
            skEllipse(sketch, "E1884", {"center": v(7534.08, 25764.73) * mm, "majorRadius": 28.27 * mm, "minorRadius": 28.15 * mm, "majorAxis": v(-0.96, -0.29)});
            skLineSegment(sketch, "E1885", {"start": v(7515.83, 25751.85) * mm, "end": v(7511.75, 25765.33) * mm});
            skLineSegment(sketch, "E1886", {"start": v(7511.75, 25765.33) * mm, "end": v(7559.1, 25779.66) * mm});
            skLineSegment(sketch, "E1887", {"start": v(7559.1, 25779.66) * mm, "end": v(7563.18, 25766.19) * mm});
            skLineSegment(sketch, "E1888", {"start": v(7563.18, 25766.19) * mm, "end": v(7515.83, 25751.85) * mm});
            skEllipse(sketch, "E1889", {"center": v(7614.08, 25788.94) * mm, "majorRadius": 28.27 * mm, "minorRadius": 28.15 * mm, "majorAxis": v(-0.96, -0.29)});
            skLineSegment(sketch, "E1890", {"start": v(7593.19, 25775.27) * mm, "end": v(7589.1, 25788.74) * mm});
            skLineSegment(sketch, "E1891", {"start": v(7589.1, 25788.74) * mm, "end": v(7636.45, 25803.07) * mm});
            skLineSegment(sketch, "E1892", {"start": v(7636.45, 25803.07) * mm, "end": v(7640.53, 25789.6) * mm});
            skLineSegment(sketch, "E1893", {"start": v(7640.53, 25789.6) * mm, "end": v(7593.19, 25775.27) * mm});
            skLineSegment(sketch, "E1894", {"start": v(7460.65, 25692.64) * mm, "end": v(7360.76, 26022.67) * mm});
            skLineSegment(sketch, "E1895", {"start": v(7360.76, 26022.67) * mm, "end": v(7834.21, 26165.98) * mm});
            skLineSegment(sketch, "E1896", {"start": v(7834.21, 26165.98) * mm, "end": v(7934.1, 25835.95) * mm});
            skLineSegment(sketch, "E1897", {"start": v(7934.1, 25835.95) * mm, "end": v(7460.65, 25692.64) * mm});
            skLineSegment(sketch, "E1898", {"start": v(7856.78, 26001.67) * mm, "end": v(7780.22, 25978.5) * mm});
            skLineSegment(sketch, "E1899", {"start": v(7835.37, 26083.87) * mm, "end": v(7781.26, 26067.5) * mm});
            skLineSegment(sketch, "E1900", {"start": v(7745.72, 25999.47) * mm, "end": v(7781.09, 26065.54) * mm});
            skLineSegment(sketch, "E1901", {"start": v(7877.04, 25918.81) * mm, "end": v(7833.14, 25905.53) * mm});
            skLineSegment(sketch, "E1902", {"start": v(7770.05, 25939.97) * mm, "end": v(7836.12, 25904.6) * mm});
            skLineSegment(sketch, "E1903", {"start": v(7637.64, 25931.67) * mm, "end": v(7714.2, 25954.85) * mm});
            skLineSegment(sketch, "E1904", {"start": v(7608.91, 26015.12) * mm, "end": v(7663.02, 26031.5) * mm});
            skLineSegment(sketch, "E1905", {"start": v(7730.32, 25994.6) * mm, "end": v(7664.25, 26029.97) * mm});
            skLineSegment(sketch, "E1906", {"start": v(7665.53, 25849.3) * mm, "end": v(7708.66, 25862.35) * mm});
            skLineSegment(sketch, "E1907", {"start": v(7744.03, 25928.43) * mm, "end": v(7708.66, 25862.35) * mm});
            skLineSegment(sketch, "E1908", {"start": v(7618.07, 25963.33) * mm, "end": v(7555.18, 25944.29) * mm});
            skLineSegment(sketch, "E1909", {"start": v(7597.31, 26045.72) * mm, "end": v(7556.22, 26033.28) * mm});
            skLineSegment(sketch, "E1910", {"start": v(7520.68, 25965.26) * mm, "end": v(7556.05, 26031.33) * mm});
            skLineSegment(sketch, "E1911", {"start": v(7649.29, 25880.9) * mm, "end": v(7608.9, 25868.68) * mm});
            skLineSegment(sketch, "E1912", {"start": v(7545.01, 25905.76) * mm, "end": v(7611.08, 25870.4) * mm});
            skLineSegment(sketch, "E1913", {"start": v(7425.75, 25901.45) * mm, "end": v(7489.16, 25920.64) * mm});
            skLineSegment(sketch, "E1914", {"start": v(7398.29, 25985.28) * mm, "end": v(7430.16, 25994.92) * mm});
            skLineSegment(sketch, "E1915", {"start": v(7505.28, 25960.4) * mm, "end": v(7439.2, 25995.76) * mm});
            skLineSegment(sketch, "E1916", {"start": v(7448.32, 25817.84) * mm, "end": v(7483.62, 25828.15) * mm});
            skLineSegment(sketch, "E1917", {"start": v(7518.99, 25894.22) * mm, "end": v(7483.62, 25828.15) * mm});
            skEllipse(sketch, "E1918", {"center": v(7747.52, 25965.14) * mm, "majorRadius": 35.33 * mm, "minorRadius": 35.19 * mm, "majorAxis": v(-0.96, -0.29)});
            skEllipse(sketch, "E1919", {"center": v(7747.52, 25965.14) * mm, "majorRadius": 25 * mm, "minorRadius": 25 * mm, "majorAxis": v(-0.29, 0.96)});
            skEllipse(sketch, "E1920", {"center": v(7522.48, 25930.93) * mm, "majorRadius": 35.33 * mm, "minorRadius": 35.19 * mm, "majorAxis": v(-0.96, -0.29)});
            skEllipse(sketch, "E1921", {"center": v(7522.86, 25931.04) * mm, "majorRadius": 25 * mm, "minorRadius": 25 * mm, "majorAxis": v(-0.29, 0.96)});
            skLineSegment(sketch, "E1922", {"start": v(7616.05, 24962.7) * mm, "end": v(7442.23, 25536.97) * mm});
            skLineSegment(sketch, "E1923", {"start": v(7442.23, 25536.97) * mm, "end": v(8016.5, 25710.79) * mm});
            skLineSegment(sketch, "E1924", {"start": v(8016.5, 25710.79) * mm, "end": v(8190.32, 25136.52) * mm});
            skLineSegment(sketch, "E1925", {"start": v(8190.32, 25136.52) * mm, "end": v(7616.05, 24962.7) * mm});
            skLineSegment(sketch, "E1926", {"start": v(6906.29, 27307.63) * mm, "end": v(6732.47, 27881.9) * mm});
            skLineSegment(sketch, "E1927", {"start": v(6732.47, 27881.9) * mm, "end": v(6751.61, 27887.7) * mm});
            skLineSegment(sketch, "E1928", {"start": v(6751.61, 27887.7) * mm, "end": v(6925.43, 27313.43) * mm});
            skLineSegment(sketch, "E1929", {"start": v(6925.43, 27313.43) * mm, "end": v(6906.29, 27307.63) * mm});
            skLineSegment(sketch, "E1930", {"start": v(6920.77, 27259.78) * mm, "end": v(6914.98, 27278.92) * mm});
            skLineSegment(sketch, "E1931", {"start": v(6914.98, 27278.92) * mm, "end": v(7537.1, 27467.23) * mm});
            skLineSegment(sketch, "E1932", {"start": v(7537.1, 27467.23) * mm, "end": v(7542.9, 27448.08) * mm});
            skLineSegment(sketch, "E1933", {"start": v(7542.9, 27448.08) * mm, "end": v(6920.77, 27259.78) * mm});
            skLineSegment(sketch, "E1934", {"start": v(7287.56, 26117.03) * mm, "end": v(7113.74, 26691.3) * mm});
            skLineSegment(sketch, "E1935", {"start": v(7113.74, 26691.3) * mm, "end": v(7664.08, 26857.88) * mm});
            skLineSegment(sketch, "E1936", {"start": v(7664.08, 26857.88) * mm, "end": v(7837.9, 26283.6) * mm});
            skLineSegment(sketch, "E1937", {"start": v(7837.9, 26283.6) * mm, "end": v(7287.56, 26117.03) * mm});
            skLineSegment(sketch, "E1938", {"start": v(7287.56, 26117.03) * mm, "end": v(7644.94, 26852.08) * mm});
            skLineSegment(sketch, "E1939", {"start": v(7818.76, 26277.81) * mm, "end": v(7113.74, 26691.3) * mm});
            skLineSegment(sketch, "E1940", {"start": v(7624.74, 24933.98) * mm, "end": v(7616.05, 24962.7) * mm});
            skLineSegment(sketch, "E1941", {"start": v(7616.05, 24962.7) * mm, "end": v(7635.2, 24968.49) * mm});
            skLineSegment(sketch, "E1942", {"start": v(7635.2, 24968.49) * mm, "end": v(7643.89, 24939.78) * mm});
            skLineSegment(sketch, "E1943", {"start": v(7643.89, 24939.78) * mm, "end": v(7624.74, 24933.98) * mm});
            skLineSegment(sketch, "E1944", {"start": v(7643.89, 24939.78) * mm, "end": v(7635.2, 24968.49) * mm});
            skLineSegment(sketch, "E1945", {"start": v(7635.2, 24968.49) * mm, "end": v(7662.72, 24976.82) * mm});
            skLineSegment(sketch, "E1946", {"start": v(7662.72, 24976.82) * mm, "end": v(7671.41, 24948.1) * mm});
            skLineSegment(sketch, "E1947", {"start": v(7671.41, 24948.1) * mm, "end": v(7643.89, 24939.78) * mm});
            skLineSegment(sketch, "E1948", {"start": v(7635.2, 24968.49) * mm, "end": v(7671.41, 24948.1) * mm});
            skLineSegment(sketch, "E1949", {"start": v(7643.89, 24939.78) * mm, "end": v(7662.72, 24976.82) * mm});
            skLineSegment(sketch, "E1950", {"start": v(7892.74, 25015.1) * mm, "end": v(7188.77, 27340.9) * mm});
            skLineSegment(sketch, "E1951", {"start": v(7188.77, 27340.9) * mm, "end": v(7504.61, 27436.5) * mm});
            skLineSegment(sketch, "E1952", {"start": v(7504.61, 27436.5) * mm, "end": v(8208.59, 25110.7) * mm});
            skLineSegment(sketch, "E1953", {"start": v(8208.59, 25110.7) * mm, "end": v(7892.74, 25015.1) * mm});
            skLineSegment(sketch, "E1954", {"start": v(7362.59, 26766.62) * mm, "end": v(7188.77, 27340.9) * mm});
            skLineSegment(sketch, "E1955", {"start": v(7504.61, 27436.5) * mm, "end": v(7678.43, 26862.22) * mm});
            skLineSegment(sketch, "E1956", {"start": v(7678.43, 26862.22) * mm, "end": v(7362.59, 26766.62) * mm});
            skLineSegment(sketch, "E1957", {"start": v(7884.05, 25043.81) * mm, "end": v(7710.23, 25618.08) * mm});
            skLineSegment(sketch, "E1958", {"start": v(7710.23, 25618.08) * mm, "end": v(8026.07, 25713.68) * mm});
            skLineSegment(sketch, "E1959", {"start": v(8026.07, 25713.68) * mm, "end": v(8199.9, 25139.41) * mm});
            skLineSegment(sketch, "E1960", {"start": v(8199.9, 25139.41) * mm, "end": v(7884.05, 25043.81) * mm});
            skLineSegment(sketch, "E1961", {"start": v(8026.07, 25713.68) * mm, "end": v(7903.19, 25049.6) * mm});
            skLineSegment(sketch, "E1962", {"start": v(7188.77, 27340.9) * mm, "end": v(7207.9, 27346.69) * mm});
            skLineSegment(sketch, "E1963", {"start": v(7207.9, 27346.69) * mm, "end": v(7381.73, 26772.42) * mm});
            skLineSegment(sketch, "E1964", {"start": v(7381.73, 26772.42) * mm, "end": v(7362.59, 26766.62) * mm});
            skLineSegment(sketch, "E1965", {"start": v(7668.86, 26859.33) * mm, "end": v(7207.9, 27346.69) * mm});
            skLineSegment(sketch, "E1966", {"start": v(7536.4, 26192.35) * mm, "end": v(7362.59, 26766.62) * mm});
            skLineSegment(sketch, "E1967", {"start": v(7362.59, 26766.62) * mm, "end": v(7678.43, 26862.22) * mm});
            skLineSegment(sketch, "E1968", {"start": v(7678.43, 26862.22) * mm, "end": v(7852.25, 26287.95) * mm});
            skLineSegment(sketch, "E1969", {"start": v(7852.25, 26287.95) * mm, "end": v(7536.4, 26192.35) * mm});
            skLineSegment(sketch, "E1970", {"start": v(7381.73, 26772.42) * mm, "end": v(7852.25, 26287.95) * mm});
            skLineSegment(sketch, "E1971", {"start": v(7710.23, 25618.08) * mm, "end": v(7536.4, 26192.35) * mm});
            skLineSegment(sketch, "E1972", {"start": v(7536.4, 26192.35) * mm, "end": v(7852.25, 26287.95) * mm});
            skLineSegment(sketch, "E1973", {"start": v(7852.25, 26287.95) * mm, "end": v(8026.07, 25713.68) * mm});
            skLineSegment(sketch, "E1974", {"start": v(8026.07, 25713.68) * mm, "end": v(7710.23, 25618.08) * mm});
            skLineSegment(sketch, "E1975", {"start": v(7729.37, 25623.88) * mm, "end": v(7852.25, 26287.95) * mm});
            skLineSegment(sketch, "E1976", {"start": v(7362.59, 26766.62) * mm, "end": v(7381.73, 26772.42) * mm});
            skLineSegment(sketch, "E1977", {"start": v(7381.73, 26772.42) * mm, "end": v(7555.55, 26198.15) * mm});
            skLineSegment(sketch, "E1978", {"start": v(7555.55, 26198.15) * mm, "end": v(7536.4, 26192.35) * mm});
            skLineSegment(sketch, "E1979", {"start": v(7536.4, 26192.35) * mm, "end": v(7555.55, 26198.15) * mm});
            skLineSegment(sketch, "E1980", {"start": v(7555.55, 26198.15) * mm, "end": v(7729.37, 25623.88) * mm});
            skLineSegment(sketch, "E1981", {"start": v(7729.37, 25623.88) * mm, "end": v(7710.23, 25618.08) * mm});
            skLineSegment(sketch, "E1982", {"start": v(7710.23, 25618.08) * mm, "end": v(7729.37, 25623.88) * mm});
            skLineSegment(sketch, "E1983", {"start": v(7729.37, 25623.88) * mm, "end": v(7903.19, 25049.6) * mm});
            skLineSegment(sketch, "E1984", {"start": v(7903.19, 25049.6) * mm, "end": v(7884.05, 25043.81) * mm});
            skLineSegment(sketch, "E1985", {"start": v(7892.74, 25015.1) * mm, "end": v(7884.05, 25043.81) * mm});
            skLineSegment(sketch, "E1986", {"start": v(7884.05, 25043.81) * mm, "end": v(7903.19, 25049.6) * mm});
            skLineSegment(sketch, "E1987", {"start": v(7903.19, 25049.6) * mm, "end": v(7911.88, 25020.9) * mm});
            skLineSegment(sketch, "E1988", {"start": v(7911.88, 25020.9) * mm, "end": v(7892.74, 25015.1) * mm});
            skLineSegment(sketch, "E1989", {"start": v(7911.88, 25020.9) * mm, "end": v(7903.19, 25049.6) * mm});
            skLineSegment(sketch, "E1990", {"start": v(7903.19, 25049.6) * mm, "end": v(7930.71, 25057.94) * mm});
            skLineSegment(sketch, "E1991", {"start": v(7930.71, 25057.94) * mm, "end": v(7939.4, 25029.22) * mm});
            skLineSegment(sketch, "E1992", {"start": v(7939.4, 25029.22) * mm, "end": v(7911.88, 25020.9) * mm});
            skLineSegment(sketch, "E1993", {"start": v(7903.19, 25049.6) * mm, "end": v(7939.4, 25029.22) * mm});
            skLineSegment(sketch, "E1994", {"start": v(7911.88, 25020.9) * mm, "end": v(7930.71, 25057.94) * mm});
            skLineSegment(sketch, "E1995", {"start": v(6732.47, 27881.9) * mm, "end": v(6723.78, 27910.62) * mm});
            skLineSegment(sketch, "E1996", {"start": v(6723.78, 27910.62) * mm, "end": v(6742.92, 27916.41) * mm});
            skLineSegment(sketch, "E1997", {"start": v(6742.92, 27916.41) * mm, "end": v(6751.61, 27887.7) * mm});
            skLineSegment(sketch, "E1998", {"start": v(6751.61, 27887.7) * mm, "end": v(6732.47, 27881.9) * mm});
            skLineSegment(sketch, "E1999", {"start": v(6751.61, 27887.7) * mm, "end": v(6742.92, 27916.41) * mm});
            skLineSegment(sketch, "E2000", {"start": v(6742.92, 27916.41) * mm, "end": v(6770.45, 27924.74) * mm});
            skLineSegment(sketch, "E2001", {"start": v(6770.45, 27924.74) * mm, "end": v(6779.14, 27896.03) * mm});
            skLineSegment(sketch, "E2002", {"start": v(6779.14, 27896.03) * mm, "end": v(6751.61, 27887.7) * mm});
            skLineSegment(sketch, "E2003", {"start": v(6742.92, 27916.41) * mm, "end": v(6779.14, 27896.03) * mm});
            skLineSegment(sketch, "E2004", {"start": v(6751.61, 27887.7) * mm, "end": v(6770.45, 27924.74) * mm});
            skLineSegment(sketch, "E2005", {"start": v(7442.23, 25536.97) * mm, "end": v(7268.41, 26111.24) * mm});
            skLineSegment(sketch, "E2006", {"start": v(7268.41, 26111.24) * mm, "end": v(7842.68, 26285.06) * mm});
            skLineSegment(sketch, "E2007", {"start": v(7842.68, 26285.06) * mm, "end": v(8016.5, 25710.79) * mm});
            skLineSegment(sketch, "E2008", {"start": v(8016.5, 25710.79) * mm, "end": v(7442.23, 25536.97) * mm});
            skLineSegment(sketch, "E2009", {"start": v(6771.72, 27282.86) * mm, "end": v(6752.46, 27882.55) * mm});
            skLineSegment(sketch, "E2010", {"start": v(6752.46, 27882.55) * mm, "end": v(6732.47, 27881.9) * mm});
            skLineSegment(sketch, "E2011", {"start": v(6732.47, 27881.9) * mm, "end": v(6751.73, 27282.21) * mm});
            skLineSegment(sketch, "E2012", {"start": v(6751.73, 27282.21) * mm, "end": v(6771.72, 27282.86) * mm});
            skArc(sketch, "E2013", {"start": v(6751.73, 27282.21) * mm, "mid": v(6829.84, 27289.86) * mm, "end": v(6906.29, 27307.63) * mm});
            skLineSegment(sketch, "E2014", {"start": v(6732.47, 27881.9) * mm, "end": v(7306.74, 28055.72) * mm});
            skLineSegment(sketch, "E2015", {"start": v(7306.74, 28055.72) * mm, "end": v(7480.56, 27481.45) * mm});
            skLineSegment(sketch, "E2016", {"start": v(7480.56, 27481.45) * mm, "end": v(6906.29, 27307.63) * mm});
            skLineSegment(sketch, "E2017", {"start": v(7306.74, 28055.72) * mm, "end": v(6925.43, 27313.43) * mm});
            skLineSegment(sketch, "E2018", {"start": v(6751.61, 27887.7) * mm, "end": v(7480.56, 27481.45) * mm});
            skLineSegment(sketch, "E2019", {"start": v(6934.12, 27284.71) * mm, "end": v(6925.43, 27313.43) * mm});
            skLineSegment(sketch, "E2020", {"start": v(6925.43, 27313.43) * mm, "end": v(6944.57, 27319.22) * mm});
            skLineSegment(sketch, "E2021", {"start": v(6944.57, 27319.22) * mm, "end": v(6953.26, 27290.5) * mm});
            skLineSegment(sketch, "E2022", {"start": v(6953.26, 27290.5) * mm, "end": v(6934.12, 27284.71) * mm});
            skLineSegment(sketch, "E2023", {"start": v(6953.26, 27290.5) * mm, "end": v(6944.57, 27319.22) * mm});
            skLineSegment(sketch, "E2024", {"start": v(6944.57, 27319.22) * mm, "end": v(6972.1, 27327.55) * mm});
            skLineSegment(sketch, "E2025", {"start": v(6972.1, 27327.55) * mm, "end": v(6980.79, 27298.84) * mm});
            skLineSegment(sketch, "E2026", {"start": v(6980.79, 27298.84) * mm, "end": v(6953.26, 27290.5) * mm});
            skLineSegment(sketch, "E2027", {"start": v(6944.57, 27319.22) * mm, "end": v(6980.79, 27298.84) * mm});
            skLineSegment(sketch, "E2028", {"start": v(6953.26, 27290.5) * mm, "end": v(6972.1, 27327.55) * mm});
            skLineSegment(sketch, "E2029", {"start": v(2727.74, 31147.01) * mm, "end": v(-4048.13, 29096.1) * mm});
            skLineSegment(sketch, "E2030", {"start": v(3637.83, 40953.93) * mm, "end": v(10124.78, 19522.2) * mm});
            skLineSegment(sketch, "E2031", {"start": v(-2736.57, 39024.53) * mm, "end": v(3750.38, 17592.8) * mm});
            skLineSegment(sketch, "E2032", {"start": v(-5129.37, 38300.28) * mm, "end": v(1357.59, 16868.54) * mm});
            skCircle(sketch, "E2033", {"center": v(-5245.25, 38683.12) * mm, "radius": 400 * mm});
            skCircle(sketch, "E2034", {"center": v(-2852.45, 39407.37) * mm, "radius": 400 * mm});
            skCircle(sketch, "E2035", {"center": v(3521.95, 41336.78) * mm, "radius": 400 * mm});
            skCircle(sketch, "E2036", {"center": v(-6386.26, 35440.86) * mm, "radius": 400 * mm});
            skLineSegment(sketch, "E2037", {"start": v(1232.56, 37746.92) * mm, "end": v(-6002.92, 35556.9) * mm});
            skFitSpline(sketch, "E2038", {"points": [v(4051.69, 27214.27) * mm, v(4006.1, 27242.45) * mm, v(3955.36, 27336.86) * mm, v(3958.58, 27444.03) * mm, v(4014.98, 27535.28) * mm, v(4109.4, 27586.09) * mm, v(4216.54, 27582.92) * mm, v(4307.72, 27526.55) * mm, v(4358.46, 27432.14) * mm, v(4355.23, 27324.97) * mm, v(4298.83, 27233.73) * mm, v(4204.42, 27182.92) * mm, v(4097.28, 27186.09) * mm, v(4051.69, 27214.27) * mm]});
            skFitSpline(sketch, "E2039", {"points": [v(915.1, 33441.4) * mm, v(829.93, 33415.63) * mm, v(736.7, 33457.65) * mm]});
            skFitSpline(sketch, "E2040", {"points": [v(775.65, 33328.96) * mm, v(829.93, 33415.63) * mm, v(915.1, 33441.4) * mm]});
            skFitSpline(sketch, "E2041", {"points": [v(623.66, 34404.27) * mm, v(538.5, 34378.49) * mm, v(445.26, 34420.51) * mm]});
            skFitSpline(sketch, "E2042", {"points": [v(484.21, 34291.82) * mm, v(538.5, 34378.49) * mm, v(623.66, 34404.27) * mm]});
            skFitSpline(sketch, "E2043", {"points": [v(332.2, 35367.18) * mm, v(247.04, 35341.4) * mm, v(153.8, 35383.42) * mm]});
            skFitSpline(sketch, "E2044", {"points": [v(192.76, 35254.73) * mm, v(247.04, 35341.4) * mm, v(332.2, 35367.18) * mm]});
            skFitSpline(sketch, "E2045", {"points": [v(186.49, 35848.6) * mm, v(101.32, 35822.83) * mm, v(8.09, 35864.85) * mm]});
            skFitSpline(sketch, "E2046", {"points": [v(3317.81, 34493.6) * mm, v(3292.03, 34578.78) * mm, v(3334.06, 34672) * mm]});
            skFitSpline(sketch, "E2047", {"points": [v(3205.36, 34633.06) * mm, v(3292.03, 34578.78) * mm, v(3317.81, 34493.6) * mm]});
            skFitSpline(sketch, "E2048", {"points": [v(4280.67, 34785.05) * mm, v(4254.9, 34870.22) * mm, v(4296.91, 34963.45) * mm]});
            skFitSpline(sketch, "E2049", {"points": [v(4168.22, 34924.5) * mm, v(4254.9, 34870.22) * mm, v(4280.67, 34785.05) * mm]});
            skFitSpline(sketch, "E2050", {"points": [v(4770.27, 35107.64) * mm, v(4733.8, 35016.25) * mm, v(4759.53, 34931.27) * mm]});
            skSolve(sketch);
        }
        {
            var Q0;
            Q0=qCreatedBy(makeId("Top.planeOp"),FACE);
            var Q1;
            Q1=qCreatedBy(makeId("Top.planeOp"),FACE);
            var Q2;
            Q2=qCreatedBy(makeId("Top.planeOp"),FACE);
            var sketch = newSketch(context, id + "F1", { "sketchPlane" : qUnion([Q0, Q1, Q2])});
            skLineSegment(sketch, "E2051.0", {"start": v(8303.3, 25022.24) * mm, "end": v(8590.44, 25109.15) * mm});
            skLineSegment(sketch, "E2051.1", {"start": v(8275.24, 25028.58) * mm, "end": v(7643.52, 24837.37) * mm});
            skLineSegment(sketch, "E2051.4", {"start": v(8246.85, 25122.28) * mm, "end": v(7345.9, 28098.92) * mm});
            skLineSegment(sketch, "E2051.5", {"start": v(7345.9, 28098.92) * mm, "end": v(6714.19, 27907.71) * mm});
            skLineSegment(sketch, "E2051.6", {"start": v(6714.19, 27907.71) * mm, "end": v(6686.09, 28000.55) * mm});
            skLineSegment(sketch, "E2051.9", {"start": v(7106.28, 28127.74) * mm, "end": v(6323.55, 30713.74) * mm});
            skLineSegment(sketch, "E2051.10", {"start": v(6323.55, 30713.74) * mm, "end": v(6018.23, 30621.33) * mm});
            skLineSegment(sketch, "E2051.11", {"start": v(6018.23, 30621.33) * mm, "end": v(5596.86, 32013.45) * mm});
            skLineSegment(sketch, "E2051.13", {"start": v(6057.79, 32277.66) * mm, "end": v(3665, 31553.41) * mm});
            skLineSegment(sketch, "E2051.14", {"start": v(5539.28, 33990.02) * mm, "end": v(6057.79, 32277.66) * mm});
            skLineSegment(sketch, "E2051.16", {"start": v(1038.97, 28597.26) * mm, "end": v(1585.97, 29073.44) * mm});
            skLineSegment(sketch, "E2051.24", {"start": v(981.9, 30734.55) * mm, "end": v(-2157.46, 29784.33) * mm});
            skLineSegment(sketch, "E2051.25", {"start": v(-2157.46, 29784.33) * mm, "end": v(-2347.02, 30410.5) * mm});
            skLineSegment(sketch, "E2051.27", {"start": v(-3425.5, 33295.77) * mm, "end": v(-2534.67, 30352.63) * mm});
            skLineSegment(sketch, "E2051.31", {"start": v(-622.8, 35013.09) * mm, "end": v(-861.8, 34940.5) * mm});
            skLineSegment(sketch, "E2051.32", {"start": v(-977.95, 36186.57) * mm, "end": v(-902.73, 35938) * mm});
            skLineSegment(sketch, "E2051.33", {"start": v(-710, 34438.17) * mm, "end": v(-3559.9, 33575.84) * mm});
            skLineSegment(sketch, "E2051.34", {"start": v(-861.8, 34940.5) * mm, "end": v(-710, 34438.17) * mm});
            skLineSegment(sketch, "E2051.35", {"start": v(-3973.74, 34943.1) * mm, "end": v(-3685.65, 35030.3) * mm});
            skLineSegment(sketch, "E2051.36", {"start": v(-3559.9, 33575.84) * mm, "end": v(-3973.74, 34943.1) * mm});
            skLineSegment(sketch, "E2051.37", {"start": v(-3685.65, 35030.3) * mm, "end": v(-3957.95, 35930) * mm});
            skLineSegment(sketch, "E2051.41", {"start": v(7597.64, 21063) * mm, "end": v(9116.94, 21522.85) * mm});
            skLineSegment(sketch, "E2051.42", {"start": v(9116.94, 21522.85) * mm, "end": v(8459.27, 23695.52) * mm});
            skLineSegment(sketch, "E2051.43", {"start": v(8459.27, 23695.52) * mm, "end": v(8971.72, 23850.63) * mm});
            skLineSegment(sketch, "E2051.45", {"start": v(383.02, 32713.3) * mm, "end": v(681.08, 31728.48) * mm});
            skLineSegment(sketch, "E2051.46", {"start": v(688.47, 32038.93) * mm, "end": v(503.96, 32648.57) * mm});
            skLineSegment(sketch, "E2051.47", {"start": v(1870.5, 32396.71) * mm, "end": v(1711.8, 32348.67) * mm});
            skLineSegment(sketch, "E2051.48", {"start": v(3194.1, 32695.99) * mm, "end": v(2994.87, 32635.69) * mm});
            skLineSegment(sketch, "E2051.49", {"start": v(2368.65, 31137.53) * mm, "end": v(3556.94, 31497.2) * mm});
            skLineSegment(sketch, "E2051.50", {"start": v(2396.47, 31045.6) * mm, "end": v(2368.65, 31137.53) * mm});
            skLineSegment(sketch, "E2051.51", {"start": v(3665, 31553.41) * mm, "end": v(3596, 31781.37) * mm});
            skLineSegment(sketch, "E2051.52", {"start": v(3556.94, 31497.2) * mm, "end": v(3481.43, 31746.7) * mm});
            skLineSegment(sketch, "E2051.53", {"start": v(4630.34, 33714.9) * mm, "end": v(5539.28, 33990.02) * mm});
            skLineSegment(sketch, "E2051.54", {"start": v(4569.53, 33915.8) * mm, "end": v(4630.34, 33714.9) * mm});
            skLineSegment(sketch, "E2051.55", {"start": v(3803.84, 33684.03) * mm, "end": v(4569.53, 33915.8) * mm});
            skLineSegment(sketch, "E2051.56", {"start": v(3864.66, 33483.1) * mm, "end": v(3803.84, 33684.03) * mm});
            skLineSegment(sketch, "E2051.57", {"start": v(3146.69, 33265.8) * mm, "end": v(3864.66, 33483.1) * mm});
            skLineSegment(sketch, "E2051.58", {"start": v(2703.65, 34316.33) * mm, "end": v(3166, 32788.83) * mm});
            skLineSegment(sketch, "E2051.59", {"start": v(3166, 32788.83) * mm, "end": v(2966.77, 32728.53) * mm});
            skLineSegment(sketch, "E2051.60", {"start": v(1685.98, 33006.34) * mm, "end": v(1870.5, 32396.71) * mm});
            skLineSegment(sketch, "E2051.61", {"start": v(503.96, 32648.57) * mm, "end": v(1685.98, 33006.34) * mm});
            skLineSegment(sketch, "E2051.63", {"start": v(1657.88, 33099.18) * mm, "end": v(615.22, 36543.93) * mm});
            skLineSegment(sketch, "E2051.66", {"start": v(615.22, 36543.93) * mm, "end": v(-828.96, 36106.8) * mm});
            skLineSegment(sketch, "E2051.67", {"start": v(-831.43, 36230.92) * mm, "end": v(-977.95, 36186.57) * mm});
            skLineSegment(sketch, "E2051.68", {"start": v(-1009.44, 36822.46) * mm, "end": v(-831.43, 36230.92) * mm});
            skLineSegment(sketch, "E2051.69", {"start": v(-3957.95, 35930) * mm, "end": v(-1009.44, 36822.46) * mm});
            skLineSegment(sketch, "E2051.70", {"start": v(561.48, 37297.94) * mm, "end": v(2030.34, 32445.09) * mm});
            skLineSegment(sketch, "E2051.72", {"start": v(817.35, 37375.45) * mm, "end": v(4399.01, 37834.91) * mm});
            skLineSegment(sketch, "E2051.74", {"start": v(5411.97, 34488.28) * mm, "end": v(2976.11, 33751) * mm});
            skLineSegment(sketch, "E2051.76", {"start": v(2976.11, 33751) * mm, "end": v(2796.5, 34344.43) * mm});
            skLineSegment(sketch, "E2052.1", {"start": v(734.61, 37774.63) * mm, "end": v(3515.53, 38130.64) * mm});
            skLineSegment(sketch, "E2053", {"start": v(2396.47, 31045.6) * mm, "end": v(5596.86, 32013.45) * mm});
            skLineSegment(sketch, "E2054", {"start": v(-2534.67, 30352.63) * mm, "end": v(-2347.02, 30410.5) * mm});
            skLineSegment(sketch, "E2055", {"start": v(4693.12, 37985.2) * mm, "end": v(3515.53, 38130.64) * mm});
            skLineSegment(sketch, "E2056", {"start": v(2703.65, 34316.33) * mm, "end": v(2796.5, 34344.43) * mm});
            skLineSegment(sketch, "E2057", {"start": v(-267.45, 34251.58) * mm, "end": v(-544.23, 35166.06) * mm});
            skLineSegment(sketch, "E2058", {"start": v(8275.24, 25028.58) * mm, "end": v(8303.3, 25022.24) * mm});
            skLineSegment(sketch, "E2059", {"start": v(6686.09, 28000.55) * mm, "end": v(7106.28, 28127.74) * mm});
            skLineSegment(sketch, "E2060", {"start": v(817.35, 37375.45) * mm, "end": v(561.48, 37297.94) * mm});
            skLineSegment(sketch, "E2061", {"start": v(-3425.5, 33295.77) * mm, "end": v(-267.45, 34251.58) * mm});
            skLineSegment(sketch, "E2062", {"start": v(1038.97, 28597.26) * mm, "end": v(7597.64, 21063) * mm});
            skLineSegment(sketch, "E2063", {"start": v(383.02, 32713.3) * mm, "end": v(1657.88, 33099.18) * mm});
            skLineSegment(sketch, "E2064", {"start": v(1585.97, 29073.44) * mm, "end": v(1490.98, 29387.32) * mm});
            skLineSegment(sketch, "E2065", {"start": v(7643.52, 24837.37) * mm, "end": v(7615.16, 24931.08) * mm});
            skLineSegment(sketch, "E2066", {"start": v(8246.85, 25122.28) * mm, "end": v(7615.16, 24931.08) * mm});
            skLineSegment(sketch, "E2067", {"start": v(5411.97, 34488.28) * mm, "end": v(4399.01, 37834.91) * mm});
            skLineSegment(sketch, "E2068", {"start": v(4693.12, 37985.2) * mm, "end": v(8590.44, 25109.15) * mm});
            skLineSegment(sketch, "E2069", {"start": v(8971.72, 23850.63) * mm, "end": v(9919.68, 20721.66) * mm});
            skLineSegment(sketch, "E2070", {"start": v(9919.68, 20721.66) * mm, "end": v(7849.46, 20094.46) * mm});
            skLineSegment(sketch, "E2071", {"start": v(7849.46, 20094.46) * mm, "end": v(-620.1, 29823.84) * mm});
            skLineSegment(sketch, "E2072", {"start": v(-620.1, 29823.84) * mm, "end": v(-2682.94, 29199.46) * mm});
            skLineSegment(sketch, "E2073", {"start": v(-2682.94, 29199.46) * mm, "end": v(-4773.82, 36107.33) * mm});
            skLineSegment(sketch, "E2074", {"start": v(734.61, 37774.63) * mm, "end": v(-4773.82, 36107.33) * mm});
            skLineSegment(sketch, "E2075", {"start": v(187.3, 30366.58) * mm, "end": v(1017.23, 30617.78) * mm});
            skLineSegment(sketch, "E2076", {"start": v(187.3, 30366.58) * mm, "end": v(247, 30169.35) * mm});
            skLineSegment(sketch, "E2077", {"start": v(-209.3, 30031.2) * mm, "end": v(247, 30169.35) * mm});
            skLineSegment(sketch, "E2078", {"start": v(975.28, 28670.43) * mm, "end": v(-209.3, 30031.2) * mm});
            skLineSegment(sketch, "E2079", {"start": v(975.28, 28670.43) * mm, "end": v(1474.96, 29105.4) * mm});
            skLineSegment(sketch, "E2080", {"start": v(1474.96, 29105.4) * mm, "end": v(1398.14, 29359.22) * mm});
            skLineSegment(sketch, "E2081", {"start": v(1398.14, 29359.22) * mm, "end": v(1490.98, 29387.32) * mm});
            skLineSegment(sketch, "E2082", {"start": v(1093.63, 30365.34) * mm, "end": v(1186.48, 30393.43) * mm});
            skLineSegment(sketch, "E2083.trimOffspring", {"start": v(1186.48, 30393.43) * mm, "end": v(1003.85, 30996.86) * mm});
            skLineSegment(sketch, "E2084.trimOffspring", {"start": v(1093.63, 30365.34) * mm, "end": v(1017.23, 30617.78) * mm});
            skLineSegment(sketch, "E2085", {"start": v(911, 30968.76) * mm, "end": v(1003.85, 30996.86) * mm});
            skLineSegment(sketch, "E2086", {"start": v(681.08, 31728.48) * mm, "end": v(773.92, 31756.58) * mm});
            skLineSegment(sketch, "E2087.trimOffspring", {"start": v(773.92, 31756.58) * mm, "end": v(716.57, 31946.1) * mm});
            skLineSegment(sketch, "E2088.trimOffspring", {"start": v(911, 30968.76) * mm, "end": v(981.9, 30734.55) * mm});
            skLineSegment(sketch, "E2089.trimOffspring", {"start": v(3481.43, 31746.7) * mm, "end": v(3596, 31781.37) * mm});
            skLineSegment(sketch, "E2090.trimOffspring", {"start": v(3251.48, 32506.41) * mm, "end": v(3194.1, 32695.99) * mm});
            skLineSegment(sketch, "E2091.trimOffspring", {"start": v(3366.04, 32541.08) * mm, "end": v(3146.69, 33265.8) * mm});
            skLineSegment(sketch, "E2092.trimOffspring", {"start": v(3251.48, 32506.41) * mm, "end": v(3366.04, 32541.08) * mm});
            skLineSegment(sketch, "E2093", {"start": v(862.55, 31990.28) * mm, "end": v(834.45, 32083.12) * mm});
            skLineSegment(sketch, "E2094", {"start": v(1739.9, 32255.83) * mm, "end": v(1711.8, 32348.67) * mm});
            skLineSegment(sketch, "E2095.trimOffspring", {"start": v(862.55, 31990.28) * mm, "end": v(716.57, 31946.1) * mm});
            skLineSegment(sketch, "E2096.trimOffspring", {"start": v(834.45, 32083.12) * mm, "end": v(688.47, 32038.93) * mm});
            skLineSegment(sketch, "E2097", {"start": v(-788.35, 35972.62) * mm, "end": v(-902.73, 35938) * mm});
            skLineSegment(sketch, "E2098", {"start": v(-544.23, 35166.06) * mm, "end": v(-658.62, 35131.44) * mm});
            skLineSegment(sketch, "E2099.trimOffspring", {"start": v(-658.62, 35131.44) * mm, "end": v(-622.8, 35013.09) * mm});
            skLineSegment(sketch, "E2100.trimOffspring", {"start": v(-788.35, 35972.62) * mm, "end": v(-828.96, 36106.8) * mm});
            skLineSegment(sketch, "E2101", {"start": v(2241.17, 32407.56) * mm, "end": v(2213.07, 32500.4) * mm});
            skLineSegment(sketch, "E2102", {"start": v(2994.87, 32635.69) * mm, "end": v(2966.77, 32728.53) * mm});
            skLineSegment(sketch, "E2103.trimOffspring", {"start": v(2213.07, 32500.4) * mm, "end": v(2030.34, 32445.09) * mm});
            skLineSegment(sketch, "E2104.trimOffspring", {"start": v(2241.17, 32407.56) * mm, "end": v(1739.9, 32255.83) * mm});
            skFitSpline(sketch, "E2105.0", {"points": [v(4051.69, 27214.27) * mm, v(4006.1, 27242.45) * mm, v(3955.36, 27336.86) * mm, v(3958.58, 27444.03) * mm, v(4014.98, 27535.28) * mm, v(4109.4, 27586.09) * mm, v(4216.54, 27582.92) * mm, v(4307.72, 27526.55) * mm, v(4358.46, 27432.14) * mm, v(4355.23, 27324.97) * mm, v(4298.83, 27233.73) * mm, v(4204.42, 27182.92) * mm, v(4097.28, 27186.09) * mm, v(4051.69, 27214.27) * mm]});
            skPoint(sketch, "E2106.orphan", {"position": v(-281.93, 34299.42) * mm});
            skSolve(sketch);
        }
        {
            var Q0;
            Q0=qSketchRegion(id+"F1",true);
            extrude(context, id + "F2", {"entities" : qUnion([Q0]), "depth" : (2930 - 130) * mm, "offsetDistance" : 25 * mm});
        }
        {
            var Q0;
            Q0=qCreatedBy(makeId("Top.planeOp"),FACE);
            var Q1;
            Q1=qCreatedBy(makeId("Top.planeOp"),FACE);
            var sketch = newSketch(context, id + "F3", { "sketchPlane" : qUnion([Q0, Q1])});
            skLineSegment(sketch, "E2107.0", {"start": v(7849.46, 20094.46) * mm, "end": v(-620.1, 29823.84) * mm});
            skLineSegment(sketch, "E2107.1", {"start": v(9919.68, 20721.66) * mm, "end": v(7849.46, 20094.46) * mm});
            skLineSegment(sketch, "E2107.2", {"start": v(8971.72, 23850.63) * mm, "end": v(9919.68, 20721.66) * mm});
            skLineSegment(sketch, "E2107.3", {"start": v(4693.12, 37985.2) * mm, "end": v(8590.44, 25109.15) * mm});
            skLineSegment(sketch, "E2107.4", {"start": v(4693.12, 37985.2) * mm, "end": v(3515.53, 38130.64) * mm});
            skLineSegment(sketch, "E2107.5", {"start": v(734.61, 37774.63) * mm, "end": v(3515.53, 38130.64) * mm});
            skLineSegment(sketch, "E2107.6", {"start": v(734.61, 37774.63) * mm, "end": v(-4773.82, 36107.33) * mm});
            skLineSegment(sketch, "E2107.7", {"start": v(-2682.94, 29199.46) * mm, "end": v(-4773.82, 36107.33) * mm});
            skLineSegment(sketch, "E2107.8", {"start": v(-620.1, 29823.84) * mm, "end": v(-2682.94, 29199.46) * mm});
            skLineSegment(sketch, "E2108", {"start": v(8971.72, 23850.63) * mm, "end": v(8590.44, 25109.15) * mm});
            skLineSegment(sketch, "E2109.0", {"start": v(-3425.5, 33295.77) * mm, "end": v(-267.45, 34251.58) * mm});
            skLineSegment(sketch, "E2109.1", {"start": v(-3425.5, 33295.77) * mm, "end": v(-2534.67, 30352.63) * mm});
            skLineSegment(sketch, "E2109.2", {"start": v(981.9, 30734.55) * mm, "end": v(-2157.46, 29784.33) * mm});
            skLineSegment(sketch, "E2109.3", {"start": v(383.02, 32713.3) * mm, "end": v(981.9, 30734.55) * mm});
            skLineSegment(sketch, "E2109.6", {"start": v(3166, 32788.83) * mm, "end": v(1953.77, 32421.91) * mm});
            skLineSegment(sketch, "E2109.7", {"start": v(561.48, 37297.94) * mm, "end": v(2030.34, 32445.09) * mm});
            skLineSegment(sketch, "E2109.8", {"start": v(2703.65, 34316.33) * mm, "end": v(3166, 32788.83) * mm});
            skLineSegment(sketch, "E2109.10", {"start": v(5232.35, 35081.71) * mm, "end": v(4399.01, 37834.91) * mm});
            skLineSegment(sketch, "E2110.1", {"start": v(-828.96, 36106.8) * mm, "end": v(-267.45, 34251.56) * mm});
            skLineSegment(sketch, "E2110.2", {"start": v(31.45, 36367.24) * mm, "end": v(-828.96, 36106.8) * mm});
            skPoint(sketch, "E2109.4.end.orphan", {"position": v(1657.88, 33099.18) * mm});
            skPoint(sketch, "E2109.4.start.orphan", {"position": v(383.02, 32713.3) * mm});
            skLineSegment(sketch, "E2111.trimOffspring", {"start": v(-267.45, 34251.58) * mm, "end": v(583.38, 34509.1) * mm});
            skLineSegment(sketch, "E2112", {"start": v(383.02, 32713.3) * mm, "end": v(1064.5, 32919.58) * mm});
            skLineSegment(sketch, "E2113.0", {"start": v(-2157.46, 29784.33) * mm, "end": v(-2347.02, 30410.5) * mm});
            skLineSegment(sketch, "E2114.0", {"start": v(-2534.67, 30352.63) * mm, "end": v(-2347.02, 30410.5) * mm});
            skLineSegment(sketch, "E2115", {"start": v(561.48, 37297.94) * mm, "end": v(817.35, 37375.45) * mm});
            skLineSegment(sketch, "E2116", {"start": v(1064.5, 32919.58) * mm, "end": v(31.45, 36367.24) * mm});
            skLineSegment(sketch, "E2117", {"start": v(817.35, 37375.45) * mm, "end": v(4399.01, 37834.91) * mm});
            skLineSegment(sketch, "E2118", {"start": v(5232.35, 35081.71) * mm, "end": v(2703.65, 34316.33) * mm});
            skLineSegment(sketch, "E2119.0", {"start": v(1038.97, 28597.26) * mm, "end": v(1585.97, 29073.44) * mm});
            skLineSegment(sketch, "E2119.1", {"start": v(1585.97, 29073.44) * mm, "end": v(1107.2, 30655.36) * mm});
            skLineSegment(sketch, "E2119.2", {"start": v(1107.2, 30655.36) * mm, "end": v(2396.47, 31045.6) * mm});
            skLineSegment(sketch, "E2119.4", {"start": v(6018.23, 30621.33) * mm, "end": v(5596.86, 32013.45) * mm});
            skLineSegment(sketch, "E2119.5", {"start": v(6323.55, 30713.74) * mm, "end": v(6018.23, 30621.33) * mm});
            skLineSegment(sketch, "E2119.6", {"start": v(7106.28, 28127.74) * mm, "end": v(6323.55, 30713.74) * mm});
            skLineSegment(sketch, "E2119.7", {"start": v(6686.09, 28000.55) * mm, "end": v(2627.74, 26772.17) * mm});
            skLineSegment(sketch, "E2119.8", {"start": v(7106.28, 28127.74) * mm, "end": v(2627.74, 26772.17) * mm});
            skLineSegment(sketch, "E2119.9", {"start": v(2627.74, 26772.17) * mm, "end": v(1038.97, 28597.26) * mm});
            skPoint(sketch, "E2120.orphan", {"position": v(7173.28, 28148.02) * mm});
            skPoint(sketch, "E2119.3.end.orphan", {"position": v(5663.61, 32034.54) * mm});
            skPoint(sketch, "E2119.3.start.orphan", {"position": v(1107.2, 30655.36) * mm});
            skLineSegment(sketch, "E2121", {"start": v(2396.47, 31045.6) * mm, "end": v(5596.86, 32013.45) * mm});
            skSolve(sketch);
        }
        {
            var Q0;
            Q0=qSketchRegion(id+"F3",true);
            extrude(context, id + "F4", {"entities" : qUnion([Q0]), "operationType" : NewBodyOperationType.ADD, "oppositeDirection" : true, "depth" : 130 * mm, "offsetDistance" : 25 * mm});
        }
        {
            var Q0;
            Q0=makeQuery(id+"F2.opExtrude","CAP_FACE",FACE,{"disambiguationData":[OSD([sQuery(id+"F1.wireOp",EDGE,"E2051.0"),sQuery(id+"F1.wireOp",EDGE,"E2051.1"),sQuery(id+"F1.wireOp",EDGE,"E2051.4"),sQuery(id+"F1.wireOp",EDGE,"E2051.5"),sQuery(id+"F1.wireOp",EDGE,"E2051.6"),sQuery(id+"F1.wireOp",EDGE,"E2051.9"),sQuery(id+"F1.wireOp",EDGE,"E2051.10"),sQuery(id+"F1.wireOp",EDGE,"E2051.11"),sQuery(id+"F1.wireOp",EDGE,"E2051.13"),sQuery(id+"F1.wireOp",EDGE,"E2051.14"),sQuery(id+"F1.wireOp",EDGE,"E2051.16"),sQuery(id+"F1.wireOp",EDGE,"E2051.24"),sQuery(id+"F1.wireOp",EDGE,"E2051.25"),sQuery(id+"F1.wireOp",EDGE,"E2051.27"),sQuery(id+"F1.wireOp",EDGE,"E2051.29"),sQuery(id+"F1.wireOp",EDGE,"E2051.31"),sQuery(id+"F1.wireOp",EDGE,"E2051.32"),sQuery(id+"F1.wireOp",EDGE,"E2051.33"),sQuery(id+"F1.wireOp",EDGE,"E2051.34"),sQuery(id+"F1.wireOp",EDGE,"E2051.35"),sQuery(id+"F1.wireOp",EDGE,"E2051.36"),sQuery(id+"F1.wireOp",EDGE,"E2051.37"),sQuery(id+"F1.wireOp",EDGE,"E2051.41"),sQuery(id+"F1.wireOp",EDGE,"E2051.42"),sQuery(id+"F1.wireOp",EDGE,"E2051.43"),sQuery(id+"F1.wireOp",EDGE,"E2051.45"),sQuery(id+"F1.wireOp",EDGE,"E2051.46"),sQuery(id+"F1.wireOp",EDGE,"E2051.47"),sQuery(id+"F1.wireOp",EDGE,"E2051.48"),sQuery(id+"F1.wireOp",EDGE,"E2051.49"),sQuery(id+"F1.wireOp",EDGE,"E2051.50"),sQuery(id+"F1.wireOp",EDGE,"E2051.51"),sQuery(id+"F1.wireOp",EDGE,"E2051.52"),sQuery(id+"F1.wireOp",EDGE,"E2051.53"),sQuery(id+"F1.wireOp",EDGE,"E2051.54"),sQuery(id+"F1.wireOp",EDGE,"E2051.55"),sQuery(id+"F1.wireOp",EDGE,"E2051.56"),sQuery(id+"F1.wireOp",EDGE,"E2051.57"),sQuery(id+"F1.wireOp",EDGE,"E2051.58"),sQuery(id+"F1.wireOp",EDGE,"E2051.59"),sQuery(id+"F1.wireOp",EDGE,"E2051.60"),sQuery(id+"F1.wireOp",EDGE,"E2051.61"),sQuery(id+"F1.wireOp",EDGE,"E2051.63"),sQuery(id+"F1.wireOp",EDGE,"E2051.66"),sQuery(id+"F1.wireOp",EDGE,"E2051.67"),sQuery(id+"F1.wireOp",EDGE,"E2051.68"),sQuery(id+"F1.wireOp",EDGE,"E2051.69"),sQuery(id+"F1.wireOp",EDGE,"E2051.70"),sQuery(id+"F1.wireOp",EDGE,"E2051.72"),sQuery(id+"F1.wireOp",EDGE,"E2051.74"),sQuery(id+"F1.wireOp",EDGE,"E2051.76"),sQuery(id+"F1.wireOp",EDGE,"E2052.1"),sQuery(id+"F1.wireOp",EDGE,"E2053"),sQuery(id+"F1.wireOp",EDGE,"E2054"),sQuery(id+"F1.wireOp",EDGE,"E2055"),sQuery(id+"F1.wireOp",EDGE,"E2056"),sQuery(id+"F1.wireOp",EDGE,"8N5yKqKh-33Wy-w2C3-t1WD-QRp7Pawzj6BH"),sQuery(id+"F1.wireOp",EDGE,"E2057"),sQuery(id+"F1.wireOp",EDGE,"E2058"),sQuery(id+"F1.wireOp",EDGE,"E2059"),sQuery(id+"F1.wireOp",EDGE,"E2060"),sQuery(id+"F1.wireOp",EDGE,"E2061"),sQuery(id+"F1.wireOp",EDGE,"E2062"),sQuery(id+"F1.wireOp",EDGE,"E2063"),sQuery(id+"F1.wireOp",EDGE,"E2064"),sQuery(id+"F1.wireOp",EDGE,"E2065"),sQuery(id+"F1.wireOp",EDGE,"E2066"),sQuery(id+"F1.wireOp",EDGE,"E2067"),sQuery(id+"F1.wireOp",EDGE,"E2068"),sQuery(id+"F1.wireOp",EDGE,"E2069"),sQuery(id+"F1.wireOp",EDGE,"E2070"),sQuery(id+"F1.wireOp",EDGE,"E2071"),sQuery(id+"F1.wireOp",EDGE,"E2072"),sQuery(id+"F1.wireOp",EDGE,"E2073"),sQuery(id+"F1.wireOp",EDGE,"E2074"),sQuery(id+"F1.wireOp",EDGE,"E2075"),sQuery(id+"F1.wireOp",EDGE,"E2076"),sQuery(id+"F1.wireOp",EDGE,"E2077"),sQuery(id+"F1.wireOp",EDGE,"E2078"),sQuery(id+"F1.wireOp",EDGE,"E2079"),sQuery(id+"F1.wireOp",EDGE,"E2080"),sQuery(id+"F1.wireOp",EDGE,"E2081"),sQuery(id+"F1.wireOp",EDGE,"E2082"),sQuery(id+"F1.wireOp",EDGE,"E2083.trimOffspring"),sQuery(id+"F1.wireOp",EDGE,"E2084.trimOffspring"),sQuery(id+"F1.wireOp",EDGE,"E2085"),sQuery(id+"F1.wireOp",EDGE,"E2086"),sQuery(id+"F1.wireOp",EDGE,"E2087.trimOffspring"),sQuery(id+"F1.wireOp",EDGE,"E2088.trimOffspring"),sQuery(id+"F1.wireOp",EDGE,"E2089.trimOffspring"),sQuery(id+"F1.wireOp",EDGE,"E2090.trimOffspring"),sQuery(id+"F1.wireOp",EDGE,"E2091.trimOffspring"),sQuery(id+"F1.wireOp",EDGE,"E2092.trimOffspring"),sQuery(id+"F1.wireOp",EDGE,"E2093"),sQuery(id+"F1.wireOp",EDGE,"E2094"),sQuery(id+"F1.wireOp",EDGE,"E2095.trimOffspring"),sQuery(id+"F1.wireOp",EDGE,"E2096.trimOffspring"),sQuery(id+"F1.wireOp",EDGE,"E2097"),sQuery(id+"F1.wireOp",EDGE,"E2098"),sQuery(id+"F1.wireOp",EDGE,"E2099.trimOffspring"),sQuery(id+"F1.wireOp",EDGE,"E2100.trimOffspring"),sQuery(id+"F1.wireOp",EDGE,"E2101"),sQuery(id+"F1.wireOp",EDGE,"E2102"),sQuery(id+"F1.wireOp",EDGE,"E2103.trimOffspring"),sQuery(id+"F1.wireOp",EDGE,"E2104.trimOffspring")])],"isStart":false});
            var sketch = newSketch(context, id + "F5", { "sketchPlane" : qUnion([Q0])});
            skLineSegment(sketch, "E2122.0", {"start": v(4687.04, 23962.9) * mm, "end": v(4434.9, 24252.53) * mm, "construction": true});
            skLineSegment(sketch, "E2122.1", {"start": v(2061.51, 26978.96) * mm, "end": v(1809.38, 27268.6) * mm, "construction": true});
            skLineSegment(sketch, "E2123", {"start": v(4560.97, 24107.71) * mm, "end": v(5293.04, 24744.99) * mm});
            skLineSegment(sketch, "E2124", {"start": v(1935.45, 27123.78) * mm, "end": v(2258.45, 27404.95) * mm});
            skPoint(sketch, "E2125.0", {"position": v(7638.9, 25931.83) * mm});
            skLineSegment(sketch, "E2126", {"start": v(7638.9, 25931.83) * mm, "end": v(7115.2, 27662.02) * mm});
            skPoint(sketch, "E2127.0", {"position": v(908.05, 30118.16) * mm});
            skLineSegment(sketch, "E2128.0", {"start": v(3344.76, 38068.05) * mm, "end": v(2809.15, 37999.35) * mm, "construction": true});
            skLineSegment(sketch, "E2129", {"start": v(3076.96, 38033.7) * mm, "end": v(3163.87, 37356.2) * mm});
            skLineSegment(sketch, "E2130", {"start": v(7115.2, 27662.02) * mm, "end": v(5837.7, 28345.87) * mm});
            skLineSegment(sketch, "E2131", {"start": v(5837.7, 28345.87) * mm, "end": v(4878.58, 31514.62) * mm});
            skCircle(sketch, "E2132.0", {"center": v(7896.13, 22311.4) * mm, "radius": 50 * mm});
            skCircle(sketch, "E2133.0", {"center": v(6878.77, 25672.55) * mm, "radius": 50 * mm});
            skPoint(sketch, "E2134.0", {"position": v(6714.5, 26215.26) * mm});
            skPoint(sketch, "E2134.1", {"position": v(7043.04, 25129.83) * mm});
            skLineSegment(sketch, "E2135", {"start": v(6714.5, 26215.26) * mm, "end": v(7043.04, 25129.83) * mm, "construction": true});
            skLineSegment(sketch, "E2136.0", {"start": v(7106.28, 28127.74) * mm, "end": v(6323.55, 30713.74) * mm, "construction": true});
            skLineSegment(sketch, "E2136.1", {"start": v(1107.2, 30655.36) * mm, "end": v(5663.61, 32034.54) * mm, "construction": true});
            skLineSegment(sketch, "E2136.2", {"start": v(6686.09, 28000.55) * mm, "end": v(2627.74, 26772.17) * mm, "construction": true});
            skFitSpline(sketch, "E2136.3", {"points": [v(4051.69, 27214.27) * mm, v(4006.1, 27242.45) * mm, v(3955.36, 27336.86) * mm, v(3958.58, 27444.03) * mm, v(4014.98, 27535.28) * mm, v(4109.4, 27586.09) * mm, v(4216.54, 27582.92) * mm, v(4307.72, 27526.55) * mm, v(4358.46, 27432.14) * mm, v(4355.23, 27324.97) * mm, v(4298.83, 27233.73) * mm, v(4204.42, 27182.92) * mm, v(4097.28, 27186.09) * mm, v(4051.69, 27214.27) * mm], "construction": true});
            skLineSegment(sketch, "E2136.4", {"start": v(6018.23, 30621.33) * mm, "end": v(5596.86, 32013.45) * mm, "construction": true});
            skLineSegment(sketch, "E2136.5", {"start": v(6323.55, 30713.74) * mm, "end": v(6018.23, 30621.33) * mm, "construction": true});
            skLineSegment(sketch, "E2137", {"start": v(6878.77, 25672.55) * mm, "end": v(6574.96, 25580.59) * mm, "construction": true});
            skCircle(sketch, "E2138.0", {"center": v(6574.96, 25580.59) * mm, "radius": 50 * mm});
            skLineSegment(sketch, "E2139", {"start": v(3268.23, 36971.04) * mm, "end": v(3163.87, 37356.2) * mm});
            skCircle(sketch, "E2140.0", {"center": v(5058.95, 32518.43) * mm, "radius": 50 * mm});
            skLineSegment(sketch, "E2141", {"start": v(3881.99, 32833.7) * mm, "end": v(4646.56, 33065.12) * mm, "construction": true});
            skLineSegment(sketch, "E2142", {"start": v(4805.59, 32539.71) * mm, "end": v(4041.02, 32308.3) * mm, "construction": true});
            skLineSegment(sketch, "E2143", {"start": v(3881.99, 32833.7) * mm, "end": v(4041.02, 32308.3) * mm, "construction": true});
            skLineSegment(sketch, "E2144", {"start": v(3752.86, 35233.78) * mm, "end": v(4723.1, 34421.2) * mm});
            skPoint(sketch, "E2144.endSnap0", {"position": v(3505.67, 33374.45) * mm});
            skLineSegment(sketch, "E2145", {"start": v(4723.1, 34421.2) * mm, "end": v(5332.17, 32408.94) * mm});
            skLineSegment(sketch, "E2146", {"start": v(4878.58, 31514.62) * mm, "end": v(5332.17, 32408.94) * mm});
            skLineSegment(sketch, "E2147", {"start": v(3752.86, 35233.78) * mm, "end": v(3268.23, 36971.04) * mm});
            skLineSegment(sketch, "E2148", {"start": v(-3073.52, 33826.5) * mm, "end": v(-2407.8, 34028.01) * mm, "construction": true});
            skLineSegment(sketch, "E2149", {"start": v(-2407.8, 34028.01) * mm, "end": v(-2644.52, 34810.13) * mm, "construction": true});
            skLineSegment(sketch, "E2150", {"start": v(-2644.52, 34810.13) * mm, "end": v(-3310.26, 34608.63) * mm, "construction": true});
            skLineSegment(sketch, "E2151", {"start": v(-3073.52, 33826.5) * mm, "end": v(-3310.26, 34608.63) * mm, "construction": true});
            skCircle(sketch, "E2152.0", {"center": v(-2699.12, 34924.53) * mm, "radius": 50 * mm});
            skPoint(sketch, "E2153.0", {"position": v(-1220.67, 35372.03) * mm});
            skLineSegment(sketch, "E2154", {"start": v(-1220.67, 35372.03) * mm, "end": v(-3519.52, 34676.21) * mm, "construction": true});
            skCircle(sketch, "E2155.0", {"center": v(-2068.6, 35115.38) * mm, "radius": 50 * mm});
            skCircle(sketch, "E2156.0", {"center": v(166.2, 34789.31) * mm, "radius": 50 * mm});
            skLineSegment(sketch, "E2157", {"start": v(4805.59, 32539.71) * mm, "end": v(4646.56, 33065.12) * mm, "construction": true});
            skCircle(sketch, "E2158.0", {"center": v(-1322.96, 31668.6) * mm, "radius": 50 * mm});
            skPoint(sketch, "E2159.0", {"position": v(2789.14, 31831.37) * mm});
            skPoint(sketch, "E2159.1", {"position": v(1508.54, 31443.79) * mm});
            skLineSegment(sketch, "E2160", {"start": v(2789.14, 31831.37) * mm, "end": v(1508.54, 31443.79) * mm, "construction": true});
            skCircle(sketch, "E2161.0", {"center": v(2148.84, 31637.58) * mm, "radius": 50 * mm});
            skLineSegment(sketch, "E2162", {"start": v(6239.3, 27440.09) * mm, "end": v(6765.72, 27599.42) * mm, "construction": true});
            skLineSegment(sketch, "E2163", {"start": v(7011.97, 26785.87) * mm, "end": v(6485.55, 26626.54) * mm, "construction": true});
            skLineSegment(sketch, "E2164", {"start": v(6239.3, 27440.09) * mm, "end": v(6485.55, 26626.54) * mm, "construction": true});
            skLineSegment(sketch, "E2165", {"start": v(7011.97, 26785.87) * mm, "end": v(6765.72, 27599.42) * mm, "construction": true});
            skLineSegment(sketch, "E2166.0", {"start": v(8246.85, 25122.28) * mm, "end": v(7345.9, 28098.92) * mm, "construction": true});
            skLineSegment(sketch, "E2167.0", {"start": v(7615.16, 24931.08) * mm, "end": v(8246.85, 25122.28) * mm, "construction": true});
            skLineSegment(sketch, "E2168.0", {"start": v(7643.52, 24837.37) * mm, "end": v(7615.16, 24931.08) * mm, "construction": true});
            skLineSegment(sketch, "E2169", {"start": v(6221.05, 24876.98) * mm, "end": v(6747.46, 25036.31) * mm, "construction": true});
            skLineSegment(sketch, "E2170", {"start": v(6993.7, 24222.76) * mm, "end": v(6467.3, 24063.43) * mm, "construction": true});
            skLineSegment(sketch, "E2171", {"start": v(6221.05, 24876.98) * mm, "end": v(6467.3, 24063.43) * mm, "construction": true});
            skLineSegment(sketch, "E2172", {"start": v(6993.7, 24222.76) * mm, "end": v(6747.46, 25036.31) * mm, "construction": true});
            skPoint(sketch, "E2173.0", {"position": v(3141.78, 35075.9) * mm});
            skPoint(sketch, "E2173.1", {"position": v(1919, 34705.78) * mm});
            skLineSegment(sketch, "E2174", {"start": v(3141.78, 35075.9) * mm, "end": v(1919, 34705.78) * mm, "construction": true});
            skCircle(sketch, "E2175.0", {"center": v(2590.14, 34903.62) * mm, "radius": 50 * mm});
            skPoint(sketch, "E2176.0", {"position": v(4997.08, 28345.47) * mm});
            skPoint(sketch, "E2176.1", {"position": v(4647.16, 29501.5) * mm});
            skPoint(sketch, "E2176.2", {"position": v(3702.85, 29215.68) * mm});
            skLineSegment(sketch, "E2177", {"start": v(3702.85, 29215.68) * mm, "end": v(4647.16, 29501.5) * mm, "construction": true});
            skLineSegment(sketch, "E2178", {"start": v(4997.08, 28345.47) * mm, "end": v(4647.16, 29501.5) * mm, "construction": true});
            skLineSegment(sketch, "E2179", {"start": v(4822.12, 28923.48) * mm, "end": v(3561.47, 28541.9) * mm, "construction": true});
            skLineSegment(sketch, "E2180", {"start": v(4175, 29358.59) * mm, "end": v(4349.97, 28780.57) * mm, "construction": true});
            skCircle(sketch, "E2181.0", {"center": v(4349.97, 28780.57) * mm, "radius": 50 * mm});
            skLineSegment(sketch, "E2182", {"start": v(3175.66, 28928.82) * mm, "end": v(908.05, 30118.16) * mm});
            skLineSegment(sketch, "E2183", {"start": v(5510.25, 26584.6) * mm, "end": v(4655.3, 26317.92) * mm});
            skLineSegment(sketch, "E2184", {"start": v(4655.3, 26317.92) * mm, "end": v(3859.92, 26735.09) * mm});
            skLineSegment(sketch, "E2185", {"start": v(3859.92, 26735.09) * mm, "end": v(3175.66, 28928.82) * mm});
            skLineSegment(sketch, "E2186", {"start": v(2258.45, 27404.95) * mm, "end": v(2258.45, 27768.14) * mm});
            skLineSegment(sketch, "E2187", {"start": v(2258.45, 27768.14) * mm, "end": v(2043.44, 28142.32) * mm});
            skLineSegment(sketch, "E2188", {"start": v(5293.04, 24744.99) * mm, "end": v(3049.57, 26988.45) * mm});
            skLineSegment(sketch, "E2189", {"start": v(3049.57, 26988.45) * mm, "end": v(3049.57, 27901.95) * mm});
            skLineSegment(sketch, "E2190", {"start": v(3049.57, 27901.95) * mm, "end": v(1903.05, 29088.45) * mm});
            skLineSegment(sketch, "E2191.0", {"start": v(3323.52, 34470.49) * mm, "end": v(2844.96, 34325.63) * mm, "construction": true});
            skLineSegment(sketch, "E2192", {"start": v(5058.95, 32518.43) * mm, "end": v(4927.7, 32258.07) * mm});
            skLineSegment(sketch, "E2193", {"start": v(4927.7, 32258.07) * mm, "end": v(1279.84, 31154.03) * mm});
            skLineSegment(sketch, "E2194", {"start": v(1279.84, 31154.03) * mm, "end": v(1518.86, 30324.85) * mm});
            skLineSegment(sketch, "E2195", {"start": v(1518.86, 30324.85) * mm, "end": v(908.05, 30118.16) * mm});
            skLineSegment(sketch, "E2196", {"start": v(1671.27, 31272.5) * mm, "end": v(325.72, 35661.39) * mm});
            skLineSegment(sketch, "E2197", {"start": v(325.72, 35661.39) * mm, "end": v(-1787.91, 35030.12) * mm});
            skLineSegment(sketch, "E2198", {"start": v(-2068.6, 35115.38) * mm, "end": v(-1787.91, 35030.12) * mm});
            skLineSegment(sketch, "E2199", {"start": v(6878.77, 25672.55) * mm, "end": v(6808.88, 25903.48) * mm});
            skLineSegment(sketch, "E2200", {"start": v(6808.88, 25903.48) * mm, "end": v(5510.25, 26584.6) * mm});
            skPoint(sketch, "E2201", {"position": v(2043.44, 28142.32) * mm});
            skPoint(sketch, "E2202", {"position": v(1903.05, 29088.45) * mm});
            skLineSegment(sketch, "E2203", {"start": v(2043.44, 28142.32) * mm, "end": v(573.62, 29830.77) * mm});
            skLineSegment(sketch, "E2204", {"start": v(573.62, 29830.77) * mm, "end": v(908.05, 30118.16) * mm});
            skLineSegment(sketch, "E2205", {"start": v(1903.05, 29088.45) * mm, "end": v(1538.48, 29230.38) * mm});
            skLineSegment(sketch, "E2206", {"start": v(1538.48, 29230.38) * mm, "end": v(908.05, 30118.16) * mm});
            skLineSegment(sketch, "E2207", {"start": v(3049.57, 26988.45) * mm, "end": v(3062.78, 27001.22) * mm});
            skPoint(sketch, "E2208", {"position": v(946.45, 30851.65) * mm});
            skLineSegment(sketch, "E2209", {"start": v(1138.13, 31346.5) * mm, "end": v(1093.22, 31502.86) * mm});
            skLineSegment(sketch, "E2210", {"start": v(1093.22, 31502.86) * mm, "end": v(3068.18, 32100.64) * mm});
            skLineSegment(sketch, "E2211", {"start": v(3068.18, 32100.64) * mm, "end": v(2572.5, 33738.24) * mm});
            skLineSegment(sketch, "E2212", {"start": v(2572.5, 33738.24) * mm, "end": v(3230, 33937.25) * mm});
            skLineSegment(sketch, "E2213", {"start": v(3230, 33937.25) * mm, "end": v(3090, 34399.8) * mm});
            skLineSegment(sketch, "E2214", {"start": v(1093.22, 31502.86) * mm, "end": v(20.36, 35002.32) * mm});
            skLineSegment(sketch, "E2215", {"start": v(20.36, 35002.32) * mm, "end": v(-1097.47, 34659.61) * mm});
            skLineSegment(sketch, "E2216", {"start": v(-1097.47, 34659.61) * mm, "end": v(-912.52, 34056.34) * mm});
            skLineSegment(sketch, "E2217", {"start": v(908.05, 30118.16) * mm, "end": v(589.97, 31179.59) * mm});
            skLineSegment(sketch, "E2218", {"start": v(589.97, 31179.59) * mm, "end": v(1138.13, 31346.5) * mm});
            skLineSegment(sketch, "E2219", {"start": v(6041.84, 31418.26) * mm, "end": v(5515.37, 33157.62) * mm});
            skLineSegment(sketch, "E2220", {"start": v(1731.39, 31943.2) * mm, "end": v(155.66, 37149.13) * mm});
            skPoint(sketch, "E2221", {"position": v(4264.27, 32949.42) * mm});
            skLineSegment(sketch, "E2222", {"start": v(5515.37, 33157.62) * mm, "end": v(4877.49, 32964.55) * mm});
            skLineSegment(sketch, "E2223", {"start": v(4877.49, 32964.55) * mm, "end": v(4748.44, 33390.88) * mm});
            skLineSegment(sketch, "E2224", {"start": v(4748.44, 33390.88) * mm, "end": v(3419.8, 32988.73) * mm});
            skLineSegment(sketch, "E2225", {"start": v(3419.8, 32988.73) * mm, "end": v(3573.2, 32481.95) * mm});
            skLineSegment(sketch, "E2226", {"start": v(3573.2, 32481.95) * mm, "end": v(1731.39, 31943.2) * mm});
            skSolve(sketch);
        }
        {
            var Q0;
            Q0=makeQuery(id+"F5.imprint","IMPRINT",FACE,{"disambiguationData":[TD([[makeQuery(id+"F5.imprint","IMPRINT",EDGE,{"derivedFrom":makeQuery(id+"F2.opExtrude","CAP_EDGE",EDGE,{"disambiguationData":[OSD([sQuery(id+"F1.wireOp",EDGE,"E2051.0")])],"isStart":false})}),1.0]])]});
            var sketch = newSketch(context, id + "F6", { "sketchPlane" : qUnion([Q0])});
            skLineSegment(sketch, "E2227.0", {"start": v(7345.9, 28098.92) * mm, "end": v(6714.19, 27907.71) * mm, "construction": true});
            skLineSegment(sketch, "E2228.0", {"start": v(7011.97, 26785.87) * mm, "end": v(6485.55, 26626.54) * mm});
            skLineSegment(sketch, "E2228.1", {"start": v(6239.3, 27440.09) * mm, "end": v(6485.55, 26626.54) * mm});
            skLineSegment(sketch, "E2228.2", {"start": v(6239.3, 27440.09) * mm, "end": v(6765.72, 27599.42) * mm});
            skLineSegment(sketch, "E2228.3", {"start": v(7011.97, 26785.87) * mm, "end": v(6765.72, 27599.42) * mm});
            skLineSegment(sketch, "E2229.0", {"start": v(6993.7, 24222.76) * mm, "end": v(6747.46, 25036.31) * mm});
            skLineSegment(sketch, "E2229.1", {"start": v(6993.7, 24222.76) * mm, "end": v(6467.3, 24063.43) * mm});
            skLineSegment(sketch, "E2229.2", {"start": v(6221.05, 24876.98) * mm, "end": v(6467.3, 24063.43) * mm});
            skLineSegment(sketch, "E2229.3", {"start": v(6221.05, 24876.98) * mm, "end": v(6747.46, 25036.31) * mm});
            skLineSegment(sketch, "E2229.4", {"start": v(3881.99, 32833.7) * mm, "end": v(4041.02, 32308.3) * mm});
            skLineSegment(sketch, "E2229.5", {"start": v(3881.99, 32833.7) * mm, "end": v(4646.56, 33065.12) * mm});
            skLineSegment(sketch, "E2229.6", {"start": v(4805.59, 32539.71) * mm, "end": v(4646.56, 33065.12) * mm});
            skLineSegment(sketch, "E2229.7", {"start": v(4805.59, 32539.71) * mm, "end": v(4041.02, 32308.3) * mm});
            skLineSegment(sketch, "E2229.8", {"start": v(-2407.8, 34028.01) * mm, "end": v(-2644.52, 34810.13) * mm});
            skLineSegment(sketch, "E2229.9", {"start": v(-2644.52, 34810.13) * mm, "end": v(-3310.26, 34608.63) * mm});
            skLineSegment(sketch, "E2229.10", {"start": v(-3073.52, 33826.5) * mm, "end": v(-3310.26, 34608.63) * mm});
            skLineSegment(sketch, "E2229.11", {"start": v(-3073.52, 33826.5) * mm, "end": v(-2407.8, 34028.01) * mm});
            skSolve(sketch);
        }
        {
            var Q0;
            Q0=qSketchRegion(id+"F6",true);
            extrude(context, id + "F7", {"entities" : qUnion([Q0]), "oppositeDirection" : true, "depth" : 270 * mm, "offsetDistance" : 25 * mm});
        }
        {
            var Q0;
            Q0=makeQuery(id+"F2.opExtrude","SWEPT_FACE",FACE,{"disambiguationData":[OSD([sQuery(id+"F1.wireOp",EDGE,"E2075")])]});
            var sketch = newSketch(context, id + "F8", { "sketchPlane" : qUnion([Q0])});
            skLineSegment(sketch, "E2230.bottom", {"start": v(10158.7, 2800) * mm, "end": v(10328.7, 2800) * mm});
            skLineSegment(sketch, "E2230.top", {"start": v(10158.7, 2740) * mm, "end": v(10328.7, 2740) * mm});
            skLineSegment(sketch, "E2230.left", {"start": v(10143.7, 2785) * mm, "end": v(10143.7, 2755) * mm});
            skLineSegment(sketch, "E2230.right", {"start": v(10343.7, 2785) * mm, "end": v(10343.7, 2755) * mm});
            skPoint(sketch, "E2231.visualSharp", {"position": v(10343.7, 2800) * mm});
            skArc(sketch, "E2231.filletArc", {"start": v(10343.7, 2785) * mm, "mid": v(10339.3, 2795.6) * mm, "end": v(10328.7, 2800) * mm});
            skPoint(sketch, "E2232.visualSharp", {"position": v(10343.7, 2740) * mm});
            skArc(sketch, "E2232.filletArc", {"start": v(10328.7, 2740) * mm, "mid": v(10339.3, 2744.4) * mm, "end": v(10343.7, 2755) * mm});
            skPoint(sketch, "E2233.visualSharp", {"position": v(10143.7, 2740) * mm});
            skArc(sketch, "E2233.filletArc", {"start": v(10143.7, 2755) * mm, "mid": v(10148.1, 2744.4) * mm, "end": v(10158.7, 2740) * mm});
            skPoint(sketch, "E2234.visualSharp", {"position": v(10143.7, 2800) * mm});
            skArc(sketch, "E2234.filletArc", {"start": v(10158.7, 2800) * mm, "mid": v(10148.1, 2795.6) * mm, "end": v(10143.7, 2785) * mm});
            skSolve(sketch);
        }
        {
            var Q0;
            Q0 = qSketchRegion(id + "F8", true);
            var Q1;
            Q1=sQuery(id+"F5.wireOp",EDGE,"E2194");
            var Q2;
            Q2=sQuery(id+"F5.wireOp",EDGE,"E2193");
            var Q3;
            Q3=sQuery(id+"F5.wireOp",EDGE,"E2192");
            var Q4;
            Q4=sQuery(id+"F5.wireOp",EDGE,"kGcZSspn-hcER-Nqsi-UGx7-NQiUgX1dfJvI");
            var Q5;
            Q5=sQuery(id+"F5.wireOp",EDGE,"7BX8t2Mn-Jqwu-94FP-VFa5-I3hdeHvYqdHI");
            var Q6;
            Q6=sQuery(id+"F5.wireOp",EDGE,"eMEioUq2-DQpa-45Pf-66eT-HMwIYd4lu9Qu");
            var Q7;
            Q7=sQuery(id+"F5.wireOp",EDGE,"E2195");
            sweep(context, id + "F9", {"profiles" : qUnion([Q0]), "path" : qUnion([Q1, Q2, Q3, Q4, Q5, Q6, Q7])});
        }
        {
            var Q0;
            Q0=makeQuery(id+"F9.opSweep","SWEPT_FACE",FACE,{"disambiguationData":[OSD([sQuery(id+"F5.wireOp",EDGE,"E2193"),sQuery(id+"F8.wireOp",EDGE,"E2230.right")])]});
            var sketch = newSketch(context, id + "F10", { "sketchPlane" : qUnion([Q0])});
            skLineSegment(sketch, "E2235.0", {"start": v(11890.42, 2800) * mm, "end": v(10552.46, 2800) * mm, "construction": true});
            skLineSegment(sketch, "E2236.bottom", {"start": v(10575.98, 2740) * mm, "end": v(10745.98, 2740) * mm});
            skLineSegment(sketch, "E2236.top", {"start": v(10575.98, 2800) * mm, "end": v(10745.98, 2800) * mm});
            skLineSegment(sketch, "E2236.left", {"start": v(10560.98, 2755) * mm, "end": v(10560.98, 2785) * mm});
            skLineSegment(sketch, "E2236.right", {"start": v(10760.98, 2755) * mm, "end": v(10760.98, 2785) * mm});
            skPoint(sketch, "E2237.visualSharp", {"position": v(10560.98, 2740) * mm});
            skArc(sketch, "E2237.filletArc", {"start": v(10560.98, 2755) * mm, "mid": v(10565.38, 2744.4) * mm, "end": v(10575.98, 2740) * mm});
            skPoint(sketch, "E2238.visualSharp", {"position": v(10760.98, 2740) * mm});
            skArc(sketch, "E2238.filletArc", {"start": v(10745.98, 2740) * mm, "mid": v(10756.6, 2744.4) * mm, "end": v(10760.98, 2755) * mm});
            skPoint(sketch, "E2239.visualSharp", {"position": v(10760.98, 2800) * mm});
            skArc(sketch, "E2239.filletArc", {"start": v(10760.98, 2785) * mm, "mid": v(10756.6, 2795.6) * mm, "end": v(10745.98, 2800) * mm});
            skPoint(sketch, "E2240.visualSharp", {"position": v(10560.98, 2800) * mm});
            skArc(sketch, "E2240.filletArc", {"start": v(10575.98, 2800) * mm, "mid": v(10565.38, 2795.6) * mm, "end": v(10560.98, 2785) * mm});
            skSolve(sketch);
        }
        {
            var Q0;
            Q0 = qSketchRegion(id + "F10", true);
            var Q1;
            Q1=sQuery(id+"F5.wireOp",EDGE,"E2196");
            var Q2;
            Q2=sQuery(id+"F5.wireOp",EDGE,"E2197");
            var Q3;
            Q3=sQuery(id+"F5.wireOp",EDGE,"E2198");
            sweep(context, id + "F11", {"profiles" : qUnion([Q0]), "path" : qUnion([Q1, Q2, Q3])});
        }
        {
            var Q0;
            Q0=makeQuery(id+"F2.opExtrude","SWEPT_FACE",FACE,{"disambiguationData":[OSD([sQuery(id+"F1.wireOp",EDGE,"E2051.1")])]});
            cPlane(context, id + "F12", {"entities" : qUnion([Q0]), "cplaneType" : CPlaneType.OFFSET, "offset" : 1060 * mm, "oppositeDirection" : true, "width" : 150 * mm, "height" : 150 * mm});
        }
        {
            var Q0;
            Q0=qCreatedBy(id+"F12.planeOp",FACE);
            var sketch = newSketch(context, id + "F13", { "sketchPlane" : qUnion([Q0])});
            skLineSegment(sketch, "E2241.0", {"start": v(14511.13, 2800) * mm, "end": v(15171.13, 2800) * mm, "construction": true});
            skLineSegment(sketch, "E2242.bottom", {"start": v(14675.42, 2800) * mm, "end": v(14975.42, 2800) * mm});
            skLineSegment(sketch, "E2242.top", {"start": v(14675.42, 2700) * mm, "end": v(14975.42, 2700) * mm});
            skLineSegment(sketch, "E2242.left", {"start": v(14675.42, 2800) * mm, "end": v(14675.42, 2700) * mm});
            skLineSegment(sketch, "E2242.right", {"start": v(14975.42, 2800) * mm, "end": v(14975.42, 2700) * mm});
            skSolve(sketch);
        }
        {
            var Q0;
            Q0 = qSketchRegion(id + "F13", true);
            var Q1;
            Q1=sQuery(id+"F5.wireOp",EDGE,"E2126");
            var Q2;
            Q2=sQuery(id+"F5.wireOp",EDGE,"E2130");
            var Q3;
            Q3=sQuery(id+"F5.wireOp",EDGE,"E2131");
            var Q4;
            Q4=sQuery(id+"F5.wireOp",EDGE,"E2146");
            var Q5;
            Q5=sQuery(id+"F5.wireOp",EDGE,"E2145");
            var Q6;
            Q6=sQuery(id+"F5.wireOp",EDGE,"E2144");
            var Q7;
            Q7=sQuery(id+"F5.wireOp",EDGE,"E2147");
            var Q8;
            Q8=sQuery(id+"F5.wireOp",EDGE,"E2139");
            var Q9;
            Q9=sQuery(id+"F5.wireOp",EDGE,"E2129");
            sweep(context, id + "F14", {"profiles" : qUnion([Q0]), "path" : qUnion([Q1, Q2, Q3, Q4, Q5, Q6, Q7, Q8, Q9])});
        }
        {
            var Q0;
            Q0=qCreatedBy(id+"F12.planeOp",FACE);
            var sketch = newSketch(context, id + "F15", { "sketchPlane" : qUnion([Q0])});
            skLineSegment(sketch, "E2243.0", {"start": v(14021.13, 2800) * mm, "end": v(13934.06, 2800) * mm, "construction": true});
            skLineSegment(sketch, "E2244.bottom", {"start": v(13919.06, 2800) * mm, "end": v(14104.06, 2800) * mm});
            skLineSegment(sketch, "E2244.top", {"start": v(13934.06, 2740) * mm, "end": v(14104.06, 2740) * mm});
            skLineSegment(sketch, "E2244.left", {"start": v(13919.06, 2785) * mm, "end": v(13919.06, 2755) * mm});
            skLineSegment(sketch, "E2244.right", {"start": v(14119.06, 2785) * mm, "end": v(14119.06, 2755) * mm});
            skPoint(sketch, "E2245.newPointA", {"position": v(13919.06, 2800) * mm});
            skPoint(sketch, "E2245.newPointB", {"position": v(13703.7, 2800) * mm});
            skArc(sketch, "E2245.filletArc", {"start": v(13934.06, 2800) * mm, "mid": v(13923.46, 2795.6) * mm, "end": v(13919.06, 2785) * mm});
            skPoint(sketch, "E2246.visualSharp", {"position": v(14119.06, 2800) * mm});
            skArc(sketch, "E2246.filletArc", {"start": v(14119.06, 2785) * mm, "mid": v(14114.67, 2795.6) * mm, "end": v(14104.06, 2800) * mm});
            skPoint(sketch, "E2247.visualSharp", {"position": v(14119.06, 2740) * mm});
            skArc(sketch, "E2247.filletArc", {"start": v(14104.06, 2740) * mm, "mid": v(14114.67, 2744.4) * mm, "end": v(14119.06, 2755) * mm});
            skPoint(sketch, "E2248.visualSharp", {"position": v(13919.06, 2740) * mm});
            skArc(sketch, "E2248.filletArc", {"start": v(13919.06, 2755) * mm, "mid": v(13923.46, 2744.4) * mm, "end": v(13934.06, 2740) * mm});
            skSolve(sketch);
        }
        {
            var Q0;
            Q0 = qSketchRegion(id + "F15", true);
            var Q1;
            Q1=sQuery(id+"F5.wireOp",EDGE,"E2199");
            var Q2;
            Q2=sQuery(id+"F5.wireOp",EDGE,"E2200");
            var Q3;
            Q3=sQuery(id+"F5.wireOp",EDGE,"E2183");
            var Q4;
            Q4=sQuery(id+"F5.wireOp",EDGE,"E2184");
            var Q5;
            Q5=sQuery(id+"F5.wireOp",EDGE,"E2185");
            var Q6;
            Q6=sQuery(id+"F5.wireOp",EDGE,"E2182");
            sweep(context, id + "F16", {"profiles" : qUnion([Q0]), "path" : qUnion([Q1, Q2, Q3, Q4, Q5, Q6])});
        }
        {
            var Q0;
            Q0=makeQuery(id+"F4.boolean.opBoolean","MERGE",FACE,{"derivedFrom":[makeQuery(id+"F2.opExtrude","SWEPT_FACE",FACE,{"disambiguationData":[OSD([sQuery(id+"F1.wireOp",EDGE,"E2071")])]}),makeQuery(id+"F4.opExtrude","SWEPT_FACE",FACE,{"disambiguationData":[OSD([sQuery(id+"F3.wireOp",EDGE,"E2107.0")])]})]});
            var sketch = newSketch(context, id + "F17", { "sketchPlane" : qUnion([Q0])});
            skLineSegment(sketch, "E2249.0", {"start": v(-14996.6, 2800) * mm, "end": v(-15380.6, 2800) * mm, "construction": true});
            skLineSegment(sketch, "E2249.1", {"start": v(-18995.35, 2800) * mm, "end": v(-19379.35, 2800) * mm, "construction": true});
            skLineSegment(sketch, "E2250.bottom", {"start": v(-19311.49, 2710) * mm, "end": v(-19061.49, 2710) * mm});
            skLineSegment(sketch, "E2250.top", {"start": v(-19311.49, 2800) * mm, "end": v(-19061.49, 2800) * mm});
            skLineSegment(sketch, "E2250.left", {"start": v(-19311.49, 2710) * mm, "end": v(-19311.49, 2800) * mm});
            skLineSegment(sketch, "E2250.right", {"start": v(-19061.49, 2710) * mm, "end": v(-19061.49, 2800) * mm});
            skLineSegment(sketch, "E2251.bottom", {"start": v(-15314.96, 2710) * mm, "end": v(-15064.96, 2710) * mm});
            skLineSegment(sketch, "E2251.top", {"start": v(-15314.96, 2800) * mm, "end": v(-15064.96, 2800) * mm});
            skLineSegment(sketch, "E2251.left", {"start": v(-15314.96, 2710) * mm, "end": v(-15314.96, 2800) * mm});
            skLineSegment(sketch, "E2251.right", {"start": v(-15064.96, 2710) * mm, "end": v(-15064.96, 2800) * mm});
            skSolve(sketch);
        }
        {
            var Q0;
            Q0=makeQuery(id+"F17.imprint","IMPRINT",FACE,{"disambiguationData":[TD([[makeQuery(id+"F17.imprint","IMPRINT",EDGE,{"derivedFrom":sQuery(id+"F17.wireOp",EDGE,"E2251.bottom")}),1.0]])]});
            var Q1;
            Q1=sQuery(id+"F5.wireOp",EDGE,"E2123");
            var Q2;
            Q2=sQuery(id+"F5.wireOp",EDGE,"E2188");
            var Q3;
            Q3=sQuery(id+"F5.wireOp",EDGE,"E2189");
            var Q4;
            Q4=sQuery(id+"F5.wireOp",EDGE,"E2190");
            var Q5;
            Q5=sQuery(id+"F5.wireOp",EDGE,"E2206");
            var Q6;
            Q6=sQuery(id+"F5.wireOp",EDGE,"E2205");
            sweep(context, id + "F18", {"profiles" : qUnion([Q0]), "path" : qUnion([Q1, Q2, Q3, Q4, Q5, Q6])});
        }
        {
            var Q0;
            Q0=makeQuery(id+"F17.imprint","IMPRINT",FACE,{"disambiguationData":[TD([[makeQuery(id+"F17.imprint","IMPRINT",EDGE,{"derivedFrom":sQuery(id+"F17.wireOp",EDGE,"E2250.bottom")}),1.0]])]});
            var Q1;
            Q1=sQuery(id+"F5.wireOp",EDGE,"E2124");
            var Q2;
            Q2=sQuery(id+"F5.wireOp",EDGE,"E2186");
            var Q3;
            Q3=sQuery(id+"F5.wireOp",EDGE,"E2187");
            var Q4;
            Q4=sQuery(id+"F5.wireOp",EDGE,"E2203");
            var Q5;
            Q5=sQuery(id+"F5.wireOp",EDGE,"E2204");
            sweep(context, id + "F19", {"profiles" : qUnion([Q0]), "path" : qUnion([Q1, Q2, Q3, Q4, Q5])});
        }
        {
            var Q0;
            Q0=makeQuery(id+"F5.imprint","IMPRINT",FACE,{"disambiguationData":[TD([[makeQuery(id+"F5.imprint","IMPRINT",EDGE,{"derivedFrom":sQuery(id+"F5.wireOp",EDGE,"E2158.0")}),-1.0]])]});
            var Q1;
            Q1=makeQuery(id+"F5.imprint","IMPRINT",FACE,{"disambiguationData":[TD([[makeQuery(id+"F5.imprint","IMPRINT",EDGE,{"derivedFrom":sQuery(id+"F5.wireOp",EDGE,"E2152.0")}),-1.0]])]});
            var Q2;
            Q2=makeQuery(id+"F5.imprint","IMPRINT",FACE,{"disambiguationData":[TD([[makeQuery(id+"F5.imprint","IMPRINT",EDGE,{"derivedFrom":sQuery(id+"F5.wireOp",EDGE,"E2175.0")}),-1.0]])]});
            var Q3;
            Q3=makeQuery(id+"F5.imprint","IMPRINT",FACE,{"disambiguationData":[TD([[makeQuery(id+"F5.imprint","IMPRINT",EDGE,{"derivedFrom":sQuery(id+"F5.wireOp",EDGE,"E2161.0")}),-1.0]])]});
            var Q4;
            Q4=makeQuery(id+"F5.imprint","IMPRINT",FACE,{"disambiguationData":[TD([[makeQuery(id+"F5.imprint","IMPRINT",EDGE,{"derivedFrom":sQuery(id+"F5.wireOp",EDGE,"E2181.0")}),-1.0]])]});
            var Q5;
            Q5=makeQuery(id+"F5.imprint","IMPRINT",FACE,{"disambiguationData":[TD([[makeQuery(id+"F5.imprint","IMPRINT",EDGE,{"derivedFrom":sQuery(id+"F5.wireOp",EDGE,"E2138.0")}),-1.0]])]});
            extrude(context, id + "F20", {"entities" : qUnion([Q0, Q1, Q2, Q3, Q4, Q5]), "operationType" : NewBodyOperationType.ADD, "oppositeDirection" : true, "depth" : 100 * mm, "offsetDistance" : 25 * mm});
        }
        {
            var Q0;
            Q0=makeQuery(id+"F9.opSweep","SWEPT_FACE",FACE,{"disambiguationData":[OSD([sQuery(id+"F5.wireOp",EDGE,"E2193"),sQuery(id+"F8.wireOp",EDGE,"E2230.right")])]});
            var sketch = newSketch(context, id + "F21", { "sketchPlane" : qUnion([Q0])});
            skLineSegment(sketch, "E2252.0", {"start": v(9687.29, 2800) * mm, "end": v(9517.29, 2800) * mm, "construction": true});
            skLineSegment(sketch, "E2253.bottom", {"start": v(9517.29, 2740) * mm, "end": v(9687.29, 2740) * mm});
            skLineSegment(sketch, "E2253.top", {"start": v(10175.3, 2800) * mm, "end": v(10375.3, 2800) * mm});
            skLineSegment(sketch, "E2253.left", {"start": v(9502.29, 2755) * mm, "end": v(9502.29, 2785) * mm});
            skLineSegment(sketch, "E2253.right", {"start": v(9702.29, 2755) * mm, "end": v(9702.29, 2785) * mm});
            skPoint(sketch, "E2254.visualSharp", {"position": v(9702.29, 2740) * mm});
            skArc(sketch, "E2254.filletArc", {"start": v(9687.29, 2740) * mm, "mid": v(9697.9, 2744.4) * mm, "end": v(9702.29, 2755) * mm});
            skPoint(sketch, "E2255.visualSharp", {"position": v(9502.29, 2740) * mm});
            skArc(sketch, "E2255.filletArc", {"start": v(9502.29, 2755) * mm, "mid": v(9506.68, 2744.4) * mm, "end": v(9517.29, 2740) * mm});
            skPoint(sketch, "E2256.newPointA", {"position": v(9502.29, 2800) * mm});
            skPoint(sketch, "E2256.newPointB", {"position": v(10332.73, 2800) * mm});
            skArc(sketch, "E2256.filletArc", {"start": v(9517.29, 2800) * mm, "mid": v(9506.68, 2795.6) * mm, "end": v(9502.29, 2785) * mm});
            skPoint(sketch, "E2257.newPointB", {"position": v(14096.98, 2800) * mm});
            skArc(sketch, "E2257.filletArc", {"start": v(9702.29, 2785) * mm, "mid": v(9697.9, 2795.6) * mm, "end": v(9687.29, 2800) * mm});
            skLineSegment(sketch, "E2258", {"start": v(9687.29, 2800) * mm, "end": v(9517.29, 2800) * mm});
            skSolve(sketch);
        }
        {
            var Q0;
            Q0 = qSketchRegion(id + "F21", true);
            var Q1;
            Q1=sQuery(id+"F5.wireOp",EDGE,"E2217");
            var Q2;
            Q2=sQuery(id+"F5.wireOp",EDGE,"E2218");
            var Q3;
            Q3=sQuery(id+"F5.wireOp",EDGE,"E2209");
            var Q4;
            Q4=sQuery(id+"F5.wireOp",EDGE,"Ks87D9tQ-Ne92-4KQm-7S9P-jB7qfV4lIqtk");
            var Q5;
            Q5=sQuery(id+"F5.wireOp",EDGE,"E2214");
            var Q6;
            Q6=sQuery(id+"F5.wireOp",EDGE,"E2215");
            var Q7;
            Q7=sQuery(id+"F5.wireOp",EDGE,"E2216");
            sweep(context, id + "F22", {"profiles" : qUnion([Q0]), "path" : qUnion([Q1, Q2, Q3, Q4, Q5, Q6, Q7])});
        }
        {
            var Q0;
            Q0 = qSketchRegion(id + "F21", true);
            var Q1;
            Q1=sQuery(id+"F5.wireOp",EDGE,"E2217");
            var Q2;
            Q2=sQuery(id+"F5.wireOp",EDGE,"E2218");
            var Q3;
            Q3=sQuery(id+"F5.wireOp",EDGE,"E2209");
            var Q4;
            Q4=sQuery(id+"F5.wireOp",EDGE,"E2210");
            var Q5;
            Q5=sQuery(id+"F5.wireOp",EDGE,"E2211");
            var Q6;
            Q6=sQuery(id+"F5.wireOp",EDGE,"E2212");
            var Q7;
            Q7=sQuery(id+"F5.wireOp",EDGE,"E2213");
            sweep(context, id + "F23", {"operationType" : NewBodyOperationType.ADD, "profiles" : qUnion([Q0]), "path" : qUnion([Q1, Q2, Q3, Q4, Q5, Q6, Q7])});
        }
        {
            var Q0;
            Q0=makeQuery(id+"F2.opExtrude","SWEPT_FACE",FACE,{"disambiguationData":[OSD([sQuery(id+"F1.wireOp",EDGE,"E2053")])]});
            var sketch = newSketch(context, id + "F24", { "sketchPlane" : qUnion([Q0])});
            skArc(sketch, "E2259", {"start": v(14924.6, 2698.78) * mm, "mid": v(14889.3, 2783.92) * mm, "end": v(14853.09, 2699.16) * mm});
            skLineSegment(sketch, "E2260.bottom", {"start": v(14789.03, 2789.99) * mm, "end": v(14814.03, 2789.99) * mm});
            skLineSegment(sketch, "E2260.top", {"start": v(14789.03, 2639.99) * mm, "end": v(14989.03, 2639.99) * mm});
            skLineSegment(sketch, "E2260.left", {"start": v(14789.03, 2789.99) * mm, "end": v(14789.03, 2639.99) * mm});
            skLineSegment(sketch, "E2260.right", {"start": v(14989.03, 2789.99) * mm, "end": v(14989.03, 2639.99) * mm});
            skLineSegment(sketch, "E2261", {"start": v(14964.03, 2789.99) * mm, "end": v(14964.03, 2659.82) * mm});
            skLineSegment(sketch, "E2262", {"start": v(14964.03, 2659.82) * mm, "end": v(14924.6, 2698.78) * mm});
            skLineSegment(sketch, "E2263", {"start": v(14814.03, 2789.99) * mm, "end": v(14814.03, 2661.4) * mm});
            skLineSegment(sketch, "E2264", {"start": v(14814.03, 2661.4) * mm, "end": v(14853.09, 2699.16) * mm});
            skLineSegment(sketch, "E2265.trimOffspring", {"start": v(14964.03, 2789.99) * mm, "end": v(14989.03, 2789.99) * mm});
            skSolve(sketch);
        }
        {
            var Q0;
            Q0 = qSketchRegion(id + "F24", true);
            var Q1;
            Q1=sQuery(id+"F5.wireOp",EDGE,"E2219");
            var Q2;
            Q2=sQuery(id+"F5.wireOp",EDGE,"zMgNrqsh-CP1W-5yL1-aJHu-sJIVIoIWalZp");
            var Q3;
            Q3=sQuery(id+"F5.wireOp",EDGE,"E2220");
            var Q4;
            Q4=sQuery(id+"F5.wireOp",EDGE,"E2226");
            var Q5;
            Q5=sQuery(id+"F5.wireOp",EDGE,"E2224");
            var Q6;
            Q6=sQuery(id+"F5.wireOp",EDGE,"E2225");
            var Q7;
            Q7=sQuery(id+"F5.wireOp",EDGE,"E2222");
            var Q8;
            Q8=sQuery(id+"F5.wireOp",EDGE,"E2223");
            sweep(context, id + "F25", {"profiles" : qUnion([Q0]), "path" : qUnion([Q1, Q2, Q3, Q4, Q5, Q6, Q7, Q8])});
        }
    });
